FCSTD DOCUMENT  (FreeCAD 0.21R33771 (Git))
Label: pillerAssy5
License: All rights reserved
objects: Part::FeaturePython×74, Sketcher::SketchObject×61, Part::Extrusion×56, Part::Mirroring×33, App::Part×32, Part::Compound×27, Part::Cut×19, App::FeaturePython×17, Part::Feature×12, Spreadsheet::Sheet×9, Part::MultiFuse×9, Part::Revolution×7, Part::Cylinder×7, Part::Sweep×3, PartDesign::Pad×1, Part::Chamfer×1, Part::Loft×1
note: 297 computed .brp shape members not serialized (recipe doc carries the construction recipe); baked Part::Feature solids carry a one-line shape summary decoded from their .brp

FEATURE [Part::Feature] Part__Feature  label="終沈躯体右_1500 v16"
  shape: bbox 17720 x 9400 x 6410 mm, 67 faces (baked)
FEATURE [Part::Feature] Part__Feature001  label="終沈躯体右_1500 v017"
  shape: bbox 17720 x 8350 x 6410 mm, 38 faces (baked)
FEATURE [Part::Feature] Part__Feature004  label="Cut036"
  shape: bbox 1100 x 1100 x 50 mm, 4 faces (baked)
FEATURE [Part::Feature] Part__Feature005  label="water_level"
  shape: bbox 15500 x 7750 x 4910 mm, 13 faces (baked)
FEATURE [Part::FeaturePython] b_centerPost1_001_  label="5_centerPost1_001"  # a2plus imported part (geometry in sourceFile) (typed FeaturePython)
  a2p_Version = 0.4.60n
  fixedPosition = true
  objectType = a2pPart
  sourceFile = .\centerPost.step
  subassemblyImport = false
  timeLastImport = 1.70943e+09
  updateColors = true
FEATURE [Part::FeaturePython] b_inflowPipe1_001_  label="2_inflowPipe1_001"  # a2plus imported part (geometry in sourceFile) (typed FeaturePython)
  Placement = pos=(-2.02e-13,0,-4.896) rot=(0,0,1;0rad)
  a2p_Version = 0.4.60n
  fixedPosition = false
  objectType = a2pPart
  sourceFile = .\inflowPipe.step
  subassemblyImport = false
  timeLastImport = 1.70943e+09
  updateColors = true
FEATURE [Part::FeaturePython] Cut036_001  # a2plus imported part (geometry in sourceFile) (typed FeaturePython)
  a2p_Version = 0.4.60n
  fixedPosition = true
  localSourceObject = Part__Feature004
  objectType = a2pPart
  sourceFile = converted
  subassemblyImport = false
  timeLastImport = 1.70945e+09
  updateColors = true
FEATURE [Part::FeaturePython] b_sludgePipe1_001_  label="3_sludgePipe1_001"  # a2plus imported part (geometry in sourceFile) (typed FeaturePython)
  Placement = pos=(1.29983,0,7.73) rot=(0,0,1;3.14159rad)
  a2p_Version = 0.4.60n
  fixedPosition = false
  objectType = a2pPart
  sourceFile = .\sludgePipe.step
  subassemblyImport = false
  timeLastImport = 1.70943e+09
  updateColors = true
FEATURE [Part::FeaturePython] b_bufflePlate_001_  label="4_bufflePlate_001"  # a2plus imported part (geometry in sourceFile) (typed FeaturePython)
  Placement = pos=(0,0,4689.6) rot=(0,0,1;0rad)
  a2p_Version = 0.4.60n
  fixedPosition = false
  objectType = a2pPart
  sourceFile = .\bufflePlate.FCStd
  subassemblyImport = false
  timeLastImport = 1.70902e+09
  updateColors = true
FEATURE [Spreadsheet::Sheet] Spreadsheet
  cells = A2='cage width W0; B2(W0)=1800; A3='cageLength L0; B3(L0)=4500; A4='mainShape mShp; B4(mShp)='100x100x10; A5='mShp gage mg0; B5(mg0)=55; A6='mShp width mb0; B6(mb0)=100; A7='horizontalBeam hShp; B7(hShp)='150x75x9; A8='hShp gage hg; B8(hg)=75; A9='hb0; B9(hb0)=75; A10='lutticeBeam LShp; B10(LShp)='75x75x6; A11='luttice_widht Lb0; B11(Lb0)=75; A12='lutitice length ll; B12(ll)=2234.39029715043; A13='luttice angle sita; B13(sita)=40.6; A14='gusset Gta; B14(Gta)=300; A15='gussetThickness gt; B15(gt)=6; A16='lx; B16(lx)=-760.518050346879; A17='lz; B17(lz)=201.097312797114; A18='Divishon no; B18(n0)=3; A19='DivishonPitch p0; B19(p0)=1450; A20='rakeWidth  rw; B20(rw)=952; A22='Angle; D22='Channel; A23='40x40x5; B23=40; C23=17; D23='75x40x5; E23=75; F23=40; G23=17; A24='50x50x5; B24=50; C24=30; D24='100x50x5; E24=100; F24=50; G24=30; A25='65x65x6; B25=65; C25=35; D25='125x65x6; E25=125; F25=65; G25=35; A26='75x75x6; B26=75; C26=40; D26='150x75x9; E26=150; F26=75; G26=40; A27='90x90x7; B27=90; C27=50; D27='180x75x7; E27=180; F27=75; G27=40; A28='100x100x10; B28=100; C28=55; F28=75; G28=40; A29='130x130x12; B29=130
FEATURE [Part::FeaturePython] AngleSteel  label="mShp"  # WARN: FeaturePython — macro-defined, semantics opaque (R4)
  A = 100
  B = 100
  L = 4500
  Placement = pos=(-850,-850,0) rot=(0,0,1;1.5708rad)
  Solid = true
  g0 = 7.85
  mass = 67.1327
  size = 17
  standard = SS_Equal
  t = 7
  expr: .Placement.Base.x = -Spreadsheet.W0 / 2 + Spreadsheet.mb0 / 2
  expr: .Placement.Base.y = -Spreadsheet.W0 / 2 + Spreadsheet.mb0 / 2
  expr: L = Spreadsheet.L0
FEATURE [Part::FeaturePython] Array  # Draft array (typed FeaturePython)
  AlwaysSyncPlacement = false
  Angle = 360
  ArrayType = 1
  Axis = (0,0,1)
  Base = -> AngleSteel
  Center = (0,0,0)
  Count = 4
  ExpandArray = false
  Fuse = false
  IntervalAxis = (0,0,0)
  IntervalX = (50,0,0)
  IntervalY = (0,50,0)
  IntervalZ = (0,0,50)
  NumberCircles = 3
  NumberPolar = 4
  NumberX = 2
  NumberY = 2
  NumberZ = 1
  PlacementList = 4 placements: [(-850,-850,0),(850,-850,0),(850,850,0),(-850,850,0)]
  RadialDistance = 50
  ScaleList = (4) [(1,1,1),(1,1,1),(1,1,1),(1,1,1)]
  Symmetry = 1
  TangentialDistance = 25
FEATURE [Part::FeaturePython] ChannelSteel  label="hShp"  # WARN: FeaturePython — macro-defined, semantics opaque (R4)
  B = 75
  H = 150
  L = 1600
  Placement = pos=(-800,-862.5,75) rot=(0.57735,0.57735,0.57735;2.0944rad)
  Solid = true
  g0 = 7.85
  mass = 35.6065
  size = 4
  standard = SS
  t1 = 6
  t2 = 8
  expr: .Placement.Base.x = -Spreadsheet.W0 / 2 + Spreadsheet.mb0
  expr: .Placement.Base.y = -Spreadsheet.W0 / 2 + Spreadsheet.hb0 / 2
  expr: .Placement.Base.z = Spreadsheet.hg
  expr: L = Spreadsheet.W0 - Spreadsheet.mb0 * 2
FEATURE [Part::FeaturePython] Array001  label="hBeam"  # Draft array (typed FeaturePython)
  AlwaysSyncPlacement = false
  Angle = 360
  ArrayType = 0
  Axis = (0,0,1)
  Base = -> ChannelSteel
  Center = (0,0,0)
  Count = 4
  ExpandArray = false
  Fuse = false
  IntervalAxis = (0,0,0)
  IntervalX = (100,0,0)
  IntervalY = (0,100,0)
  IntervalZ = (0,0,1450)
  NumberCircles = 3
  NumberPolar = 5
  NumberX = 1
  NumberY = 1
  NumberZ = 4
  PlacementList = 4 placements: arithmetic series from (-800,-862.5,75) step (0,0,1450) to (-800,-862.5,4425)
  RadialDistance = 50
  ScaleList = (4) [(1,1,1),(1,1,1),(1,1,1),(1,1,1)]
  Symmetry = 1
  TangentialDistance = 25
  expr: .IntervalZ.z = Spreadsheet.p0
  expr: NumberZ = Spreadsheet.n0 + 1
FEATURE [Part::FeaturePython] AngleSteel001  label="LShp"  # WARN: FeaturePython — macro-defined, semantics opaque (R4)
  A = 75
  B = 75
  L = 1000
  Placement = pos=(0,0,0) rot=(-1,0,0;1.5708rad)
  Solid = false
  g0 = 7.85
  mass = 0
  size = 10
  standard = SS_Equal
  t = 6
FEATURE [Part::FeaturePython] ChannelSteel001  # WARN: FeaturePython — macro-defined, semantics opaque (R4)
  B = 75
  H = 150
  L = 680
  Placement = pos=(0,0,6e-15) rot=(0.57735,-0.57735,-0.57735;2.0944rad)
  Solid = true
  g0 = 7.85
  mass = 15.1328
  size = 4
  standard = SS
  t1 = 6
  t2 = 8
FEATURE [Sketcher::SketchObject] Sketch006
  ExternalGeometry = -> [ChannelSteel001]
  FullyConstrained = false
  MapMode = 5
  Placement = pos=(7.49e-14,-8.3e-15,75) rot=(0,0,1;1.5708rad)
  Support = -> [ChannelSteel001]
  sketch-geometry (3):
    g0: LineSegment StartX=37.5 StartY=0 StartZ=0 EndX=-38.6181 EndY=76.1181 EndZ=0
    g1: LineSegment StartX=-38.6181 StartY=0 StartZ=0 EndX=37.5 EndY=0 EndZ=0
    g2: LineSegment StartX=-38.6181 StartY=0 StartZ=0 EndX=-38.6181 EndY=76.1181 EndZ=0
  constraints (7):
    c: Coincident(g-3,g0)
    c: Coincident(g1,g0)
    c: Coincident(g2,g1)
    c: Coincident(g2,g0)
    c: Vertical(g2)
    c: Horizontal(g1)
    c: Angle(g0,g1) = 0.785398
FEATURE [Part::Extrusion] Extrude006
  Base = -> Sketch006
  Dir = (1e-15,-1e-16,1)
  DirMode = 2
  FaceMakerClass = Part::FaceMakerBullseye
  LengthFwd = 150
  LengthRev = 0
  Reversed = true
  Solid = true
  Symmetric = false
FEATURE [Part::Mirroring] Mirror005  label="Extrude006 (mirrored)"
  Base = (-500,32.5,62.5)
  Normal = (-1,9e-16,0)
  Placement = pos=(299.54,0,0) rot=(0,0,1;0rad)
  Source = -> Extrude006
FEATURE [Part::Compound] Compound003
  Links = -> [Mirror005,Extrude006]
FEATURE [Part::Cut] Cut
  Base = -> ChannelSteel001
  Placement = pos=(-363,-857,75) rot=(0,0,-1;0.785398rad)
  Tool = -> Compound003
  expr: .Placement.Base.x = -Spreadsheet.W0 / 2 + 537
  expr: .Placement.Base.y = -Spreadsheet.W0 / 2 + 43
FEATURE [Sketcher::SketchObject] Sketch007
  FullyConstrained = true
  MapMode = 5
  Placement = pos=(0,0,0) rot=(1,0,0;1.5708rad)
  expr: Constraints[10] = Spreadsheet.W0 / 2
  expr: Constraints[15] = Spreadsheet.hg
  expr: Constraints[9] = Spreadsheet.hg * 2
  sketch-geometry (7):
    g0: LineSegment StartX=900 StartY=1.42e-14 StartZ=0 EndX=900 EndY=150 EndZ=0
    g1: LineSegment StartX=900 StartY=150 StartZ=0 EndX=930 EndY=150 EndZ=0
    g2: LineSegment StartX=930 StartY=150 StartZ=0 EndX=999.298 EndY=104.199 EndZ=0
    g3: ArcOfCircle CenterX=980 CenterY=75 CenterZ=0 NormalX=0 NormalY=0 NormalZ=1 AngleXU=0 Radius=35 StartAngle=5.29641 EndAngle=7.26996
    g4: LineSegment StartX=999.298 StartY=45.8011 StartZ=0 EndX=930 EndY=1.42e-14 EndZ=0
    g5: LineSegment StartX=930 StartY=1.42e-14 StartZ=0 EndX=900 EndY=1.42e-14 EndZ=0
    g6: Circle CenterX=980 CenterY=75 CenterZ=0 NormalX=0 NormalY=0 NormalZ=1 AngleXU=0 Radius=15
  constraints (19):
    c: Vertical(g0)
    c: Coincident(g0,g1)
    c: Horizontal(g1)
    c: Coincident(g1,g2)
    c: Tangent(g2,g3) = 1.5708
    c: Coincident(g4,g5)
    c: Coincident(g5,g0)
    c: Horizontal(g5)
    c: Coincident(g6,g3)
    c: DistanceY(g0,g0) = 150
    c: DistanceX(g-1,g0) = 900
    c: PointOnObject(g0,g-1)
    c: Vertical(g4,g1)
    c: DistanceX(g0,g3) = 80
    c: Tangent(g3,g4) = 1.5708
    c: DistanceY(g3,g1) = 75
    c: Radius(g6) = 15
    c: Radius(g3) = 35
    c: DistanceX(g0,g4) = 30
FEATURE [PartDesign::Pad] Pad
  Direction = (0,-1,2e-16)
  Length = 48
  Length2 = 10
  Midplane = true
  Placement = pos=(0,0,0) rot=(1,0,0;1.5708rad)
  Profile = -> Sketch007
  ReferenceAxis = -> Sketch007 [N_Axis]
  Type = 0
FEATURE [Sketcher::SketchObject] Sketch008
  ExternalGeometry = -> [Pad]
  FullyConstrained = true
  MapMode = 5
  Placement = pos=(0,0,8.9e-14) rot=(1,0,0;3.14159rad)
  sketch-geometry (4):
    g0: LineSegment StartX=900 StartY=-8 StartZ=0 EndX=1050 EndY=-8 EndZ=0
    g1: LineSegment StartX=1050 StartY=-8 StartZ=0 EndX=1050 EndY=8 EndZ=0
    g2: LineSegment StartX=1050 StartY=8 StartZ=0 EndX=900 EndY=8 EndZ=0
    g3: LineSegment StartX=900 StartY=8 StartZ=0 EndX=900 EndY=-8 EndZ=0
  constraints (12):
    c: Coincident(g0,g1)
    c: Coincident(g1,g2)
    c: Coincident(g2,g3)
    c: Coincident(g3,g0)
    c: Horizontal(g0)
    c: Horizontal(g2)
    c: Vertical(g1)
    c: Vertical(g3)
    c: Distance(g1) = 16
    c: PointOnObject(g2,g-4)
    c: DistanceY(g2,g-4) = 16
    c: DistanceX(g2,g2) = 150
FEATURE [Part::Extrusion] Extrude007
  Base = -> Sketch008
  Dir = (0,0,-1)
  DirMode = 2
  FaceMakerClass = Part::FaceMakerBullseye
  LengthFwd = 150
  LengthRev = 0
  Reversed = true
  Solid = true
  Symmetric = false
FEATURE [Part::Cut] Cut001
  Base = -> Pad
  Placement = pos=(0,-492,0) rot=(0,0,1;0rad)
  Tool = -> Extrude007
  expr: .Placement.Base.y = -Spreadsheet.rw / 2 - 16
FEATURE [Part::Mirroring] Mirror006  label="Cut001 (mirrored)"
  Base = (0,0,400)
  Normal = (0,-1,0)
  Source = -> Cut001
FEATURE [Part::Compound] Compound004
  Links = -> [Mirror006,Cut001]
FEATURE [Part::FeaturePython] AngleSteel002  label="LShp001"  # WARN: FeaturePython — macro-defined, semantics opaque (R4)
  A = 75
  B = 75
  L = 2234.39
  Placement = pos=(-850,-932.5,1525) rot=(0,1,0;2.2794rad)
  Solid = true
  g0 = 7.85
  mass = 15.306
  size = 10
  standard = SS_Equal
  t = 6
  expr: .Placement.Base.x = -Spreadsheet.W0 / 2 + Spreadsheet.mb0 / 2
  expr: .Placement.Base.y = -Spreadsheet.W0 / 2 - 32.5
  expr: .Placement.Base.z = Spreadsheet.p0 + Spreadsheet.hg
  expr: .Placement.Rotation.Angle = Spreadsheet.sita + 90
  expr: L = Spreadsheet.ll
FEATURE [Part::FeaturePython] Array008  # Draft array (typed FeaturePython)
  AlwaysSyncPlacement = false
  Angle = 360
  ArrayType = 0
  Axis = (0,0,1)
  Base = -> AngleSteel002
  Center = (0,0,0)
  Count = 3
  ExpandArray = false
  Fuse = false
  IntervalAxis = (0,0,0)
  IntervalX = (100,0,0)
  IntervalY = (0,100,0)
  IntervalZ = (0,0,1450)
  NumberCircles = 3
  NumberPolar = 5
  NumberX = 1
  NumberY = 1
  NumberZ = 3
  PlacementList = 3 placements: arithmetic series from (-850,-932.5,1525) step (0,0,1450) to (-850,-932.5,4425)
  RadialDistance = 50
  ScaleList = (3) [(1,1,1),(1,1,1),(1,1,1)]
  Symmetry = 1
  TangentialDistance = 25
  expr: .IntervalZ.z = Spreadsheet.p0
  expr: NumberZ = Spreadsheet.n0
FEATURE [Sketcher::SketchObject] Sketch009
  ExternalGeometry = -> [Compound004]
  FullyConstrained = true
  Placement = pos=(0,0,0) rot=(1,0,0;1.5708rad)
  expr: Constraints[17] = Spreadsheet.p0
  sketch-geometry (7):
    g0: LineSegment StartX=900 StartY=1462.5 StartZ=0 EndX=900 EndY=1587.5 EndZ=0
    g1: LineSegment StartX=900 StartY=1587.5 StartZ=0 EndX=930 EndY=1587.5 EndZ=0
    g2: LineSegment StartX=930 StartY=1587.5 StartZ=0 EndX=995.018 EndY=1556.61 EndZ=0
    g3: ArcOfCircle CenterX=980 CenterY=1525 CenterZ=0 NormalX=0 NormalY=0 NormalZ=1 AngleXU=0 Radius=35 StartAngle=5.15587 EndAngle=7.41051
    g4: LineSegment StartX=995.018 StartY=1493.39 StartZ=0 EndX=930 EndY=1462.5 EndZ=0
    g5: LineSegment StartX=930 StartY=1462.5 StartZ=0 EndX=900 EndY=1462.5 EndZ=0
    g6: Circle CenterX=980 CenterY=1525 CenterZ=0 NormalX=0 NormalY=0 NormalZ=1 AngleXU=0 Radius=15
  constraints (19):
    c: Vertical(g0)
    c: Coincident(g0,g1)
    c: Horizontal(g1)
    c: Coincident(g1,g2)
    c: Tangent(g2,g3) = 1.5708
    c: Coincident(g4,g5)
    c: Coincident(g5,g0)
    c: Horizontal(g5)
    c: Coincident(g6,g3)
    c: Radius(g6) = 15
    c: Radius(g3) = 35
    c: DistanceX(g1,g1) = 30
    c: Distance(g3,g0) = 80
    c: Tangent(g3,g4) = 1.5708
    c: Equal(g5,g1)
    c: Equal(g4,g2)
    c: Distance(g0) = 125
    c: DistanceY(g-3,g3) = 1450
    c: Vertical(g-3,g3)
FEATURE [Part::Extrusion] Extrude
  Base = -> Sketch009
  Dir = (0,-1,2e-16)
  DirMode = 2
  FaceMakerClass = Part::FaceMakerBullseye
  LengthFwd = 16
  LengthRev = 0
  Placement = pos=(0,-492,0) rot=(0,0,1;0rad)
  Solid = true
  Symmetric = true
  expr: .Placement.Base.y = -Spreadsheet.rw / 2 - 16
FEATURE [Part::Mirroring] Mirror  label="Extrude (mirrored)"
  Base = (0,0,1500)
  Normal = (0,1,0)
  Source = -> Extrude
FEATURE [Part::Compound] Compound005
  Links = -> [Mirror,Extrude]
FEATURE [Part::Compound] Compound006
  Links = -> [Compound005,Compound004]
FEATURE [Part::Mirroring] Mirror007  label="Compound006 (mirrored)"
  Base = (0,0,-1000)
  Normal = (1,0,0)
  Source = -> Compound006
FEATURE [Part::FeaturePython] ChannelSteel002  # WARN: FeaturePython — macro-defined, semantics opaque (R4)
  B = 75
  H = 150
  L = 1200
  Placement = pos=(500,0,4350) rot=(0,0,1;0rad)
  Solid = false
  g0 = 7.85
  mass = 0
  size = 4
  standard = SS
  t1 = 9
  t2 = 12.5
  expr: .Placement.Base.z = Spreadsheet.L0 - 150
FEATURE [Part::Extrusion] Extrude008
  Base = -> ChannelSteel002
  Dir = (0,1,0)
  DirMode = 2
  FaceMakerClass = Part::FaceMakerBullseye
  LengthFwd = 1334
  LengthRev = 0
  Solid = false
  Symmetric = true
FEATURE [Sketcher::SketchObject] Sketch010
  ExternalGeometry = -> [Extrude008]
  FullyConstrained = true
  MapMode = 5
  Placement = pos=(0,0,4500) rot=(0,0,1;0rad)
  Support = -> [Extrude008]
  sketch-geometry (3):
    g0: LineSegment StartX=500 StartY=667 StartZ=0 EndX=575 EndY=592 EndZ=0
    g1: LineSegment StartX=575 StartY=592 StartZ=0 EndX=575 EndY=667 EndZ=0
    g2: LineSegment StartX=575 StartY=667 StartZ=0 EndX=500 EndY=667 EndZ=0
  constraints (7):
    c: Coincident(g0,g1)
    c: Coincident(g1,g2)
    c: Coincident(g2,g0)
    c: Coincident(g1,g-3)
    c: PointOnObject(g0,g-4)
    c: Coincident(g0,g-3)
    c: Angle(g1,g0) = 0.785398
FEATURE [Part::Extrusion] Extrude009
  Base = -> Sketch010
  Dir = (0,0,1)
  DirMode = 2
  FaceMakerClass = Part::FaceMakerBullseye
  LengthFwd = 150
  LengthRev = 0
  Reversed = true
  Solid = true
  Symmetric = false
FEATURE [Part::Mirroring] Mirror008  label="Extrude009 (mirrored)"
  Base = (300,0,0)
  Normal = (0,1,0)
  Source = -> Extrude009
FEATURE [Part::Compound] Compound008
  Links = -> [Mirror008,Extrude009]
FEATURE [Part::Cut] Cut002
  Base = -> Extrude008
  Tool = -> Compound008
FEATURE [Part::FeaturePython] Array010  # Draft array (typed FeaturePython)
  AlwaysSyncPlacement = false
  Angle = 360
  ArrayType = 1
  Axis = (0,0,1)
  Base = -> Cut
  Center = (0,0,0)
  Count = 4
  ExpandArray = false
  Fuse = false
  IntervalAxis = (0,0,0)
  IntervalX = (50,0,0)
  IntervalY = (0,50,0)
  IntervalZ = (0,0,50)
  NumberCircles = 3
  NumberPolar = 4
  NumberX = 2
  NumberY = 2
  NumberZ = 1
  PlacementList = 4 placements: [(-363,-857,75),(857,-363,75),(363,857,75),(-857,363,75)]
  RadialDistance = 50
  ScaleList = (4) [(1,1,1),(1,1,1),(1,1,1),(1,1,1)]
  Symmetry = 1
  TangentialDistance = 25
FEATURE [Part::Mirroring] Mirror009  label="Cut002 (mirrored)"
  Base = (0,-600,0)
  Normal = (1,0,0)
  Source = -> Cut002
FEATURE [Part::FeaturePython] ChannelSteel003  # WARN: FeaturePython — macro-defined, semantics opaque (R4)
  B = 75
  H = 150
  L = 1000
  Placement = pos=(-500,538,4425) rot=(0.57735,0.57735,0.57735;2.0944rad)
  Solid = true
  g0 = 7.85
  mass = 22.2541
  size = 4
  standard = SS
  t1 = 9
  t2 = 12.5
FEATURE [Part::FeaturePython] Array011  # Draft array (typed FeaturePython)
  AlwaysSyncPlacement = false
  Angle = 360
  ArrayType = 0
  Axis = (0,0,1)
  Base = -> Array010
  Center = (0,0,0)
  Count = 4
  ExpandArray = false
  Fuse = false
  IntervalAxis = (0,0,0)
  IntervalX = (100,0,0)
  IntervalY = (0,100,0)
  IntervalZ = (0,0,1450)
  NumberCircles = 3
  NumberPolar = 5
  NumberX = 1
  NumberY = 1
  NumberZ = 4
  PlacementList = 4 placements: arithmetic series from (0,0,0) step (0,0,1450) to (0,0,4350)
  RadialDistance = 50
  ScaleList = (4) [(1,1,1),(1,1,1),(1,1,1),(1,1,1)]
  Symmetry = 1
  TangentialDistance = 25
  expr: .IntervalZ.z = Spreadsheet.p0
FEATURE [Part::Mirroring] Mirror010  label="ChannelSteel003 (mirrored)"
  Base = (-300,0,0)
  Normal = (0,-1,0)
  Source = -> ChannelSteel003
FEATURE [Part::Feature] Part__Feature006  label="reducer"
  Placement = pos=(0,0,4357.64) rot=(0,0,1;0rad)
  shape: bbox 1029 x 1029 x 150 mm, 111 faces (baked)
FEATURE [Part::Feature] Part__Feature008  label="Compound017"
  shape: bbox 785.2 x 75 x 709.2 mm, 36 faces (baked)
FEATURE [Part::Feature] Part__Feature009  label="Compound018"
  shape: bbox 75 x 75 x 380 mm, 11 faces (baked)
FEATURE [App::Part] Compound017  label="brade"
  Group = -> [Part__Feature008,Part__Feature009]
  Origin = -> Origin005
  Placement = pos=(23,0,-1177.59) rot=(0,0,1;0rad)
FEATURE [Part::FeaturePython] Array012  # Draft array (typed FeaturePython)
  AlwaysSyncPlacement = false
  Angle = 360
  ArrayType = 1
  Axis = (0,0,1)
  Base = -> Compound017
  Center = (0,0,0)
  Count = 2
  ExpandArray = false
  Fuse = false
  IntervalAxis = (0,0,0)
  IntervalX = (50,0,0)
  IntervalY = (0,50,0)
  IntervalZ = (0,0,50)
  NumberCircles = 3
  NumberPolar = 2
  NumberX = 2
  NumberY = 2
  NumberZ = 1
  Placement = pos=(0,0,50) rot=(0,0,1;0rad)
  PlacementList = 2 placements: [(23,0,-1177.59),(-23,2.81669e-15,-1177.59)]
  RadialDistance = 50
  ScaleList = (2) [(1,1,1),(1,1,1)]
  Symmetry = 1
  TangentialDistance = 25
FEATURE [Part::Compound] Compound
  Links = -> [Array008,Array001]
FEATURE [Part::FeaturePython] Array013  # Draft array (typed FeaturePython)
  AlwaysSyncPlacement = false
  Angle = 360
  ArrayType = 1
  Axis = (0,0,1)
  Base = -> Compound
  Center = (0,0,0)
  Count = 4
  ExpandArray = false
  Fuse = false
  IntervalAxis = (0,0,0)
  IntervalX = (50,0,0)
  IntervalY = (0,50,0)
  IntervalZ = (0,0,50)
  NumberCircles = 3
  NumberPolar = 4
  NumberX = 2
  NumberY = 2
  NumberZ = 1
  PlacementList = 4 placements: [(0,0,0),(0,0,0),(0,0,0),(0,0,0)]
  RadialDistance = 50
  ScaleList = (4) [(1,1,1),(1,1,1),(1,1,1),(1,1,1)]
  Symmetry = 1
  TangentialDistance = 25
FEATURE [Part::FeaturePython] b_trunBackle_001_  label="trunBackle_001"  # a2plus imported part (geometry in sourceFile) (typed FeaturePython)
  Placement = pos=(980,492.973,2505.44) rot=(0,1,0;3.33869rad)
  a2p_Version = 0.4.60n
  fixedPosition = false
  objectType = a2pPart
  sourceFile = .\trunBackle.FCStd
  subassemblyImport = false
  timeLastImport = 1.70945e+09
  updateColors = true
FEATURE [Part::Compound] Compound019  label="Compound020"
  Links = -> [Mirror007,Compound006]
FEATURE [App::Part] Part  label="centerCage"
  Group = -> [Spreadsheet,ChannelSteel,Array001,AngleSteel,Array,AngleSteel001,ChannelSteel001,Compound003,Sketch006,Mirror005,Extrude006,Cut,Sketch007,Pad,Sketch008,Extrude007,Cut001,Mirror006,Compound004,AngleSteel002,Array008,Sketch009,Extrude,Mirror,Compound005,Compound006,Mirror007,Compound008,Extrude008,Extrude009,ChannelSteel002,Mirror008,Sketch010,Cut002,Mirror009,ChannelSteel003,Array010,Array011,+7 more]
  Origin = -> Origin002
FEATURE [Part::Compound] Compound018  label="centerCage002"
  Links = -> [Part]
FEATURE [App::Part] Part002  label="centerCage003"
  Group = -> [Part,Compound018]
  Origin = -> Origin007
FEATURE [Part::FeaturePython] b_RakeArm_001_  label="RakeArm_001"  # a2plus imported part (geometry in sourceFile) (typed FeaturePython)
  Placement = pos=(980,-493.6,1055.44) rot=(0,0,1;0rad)
  a2p_Version = 0.4.60n
  fixedPosition = false
  objectType = a2pPart
  sourceFile = .\RakeArm.FCStd
  subassemblyImport = false
  timeLastImport = 1.70944e+09
  updateColors = true
FEATURE [Part::FeaturePython] centerCage002_001  # a2plus imported part (geometry in sourceFile) (typed FeaturePython)
  Placement = pos=(0,0,980.44) rot=(0,0,1;0rad)
  a2p_Version = 0.4.60n
  fixedPosition = true
  localSourceObject = Compound018
  objectType = a2pPart
  sourceFile = converted
  subassemblyImport = false
  timeLastImport = 1.70945e+09
  updateColors = true
FEATURE [Part::FeaturePython] b_brade_001_  label="brade_001"  # a2plus imported part (geometry in sourceFile) (typed FeaturePython)
  Placement = pos=(3000,-0.310648,1746.81) rot=(0,0,-1;0.785398rad)
  a2p_Version = 0.4.60n
  fixedPosition = false
  objectType = a2pPart
  sourceFile = .\brade.FCStd
  subassemblyImport = false
  timeLastImport = 1.70876e+09
  updateColors = true
FEATURE [App::Part] Part003  label="rake"
  Origin = -> Origin008
  Placement = pos=(0,-6,0) rot=(0,1,0;-0.099484rad)
FEATURE [Part::FeaturePython] Array014  # Draft array (typed FeaturePython)
  AlwaysSyncPlacement = false
  Angle = 360
  ArrayType = 0
  Axis = (0,0,1)
  Base = -> b_brade_001_
  Center = (0,0,0)
  Count = 6
  ExpandArray = false
  Fuse = false
  IntervalAxis = (0,0,0)
  IntervalX = (1020,0,0)
  IntervalY = (0,100,0)
  IntervalZ = (0,0,100)
  NumberCircles = 3
  NumberPolar = 5
  NumberX = 6
  NumberY = 1
  NumberZ = 1
  Placement = pos=(-1000,0.000107765,-790) rot=(0,0,1;0rad)
  PlacementList = 6 placements: arithmetic series from (3000,-0.310648,1746.81) step (1020,0,0) to (8100,-0.310648,1746.81)
  RadialDistance = 50
  ScaleList = (6) [(1,1,1),(1,1,1),(1,1,1),(1,1,1),(1,1,1),(1,1,1)]
  Symmetry = 1
  TangentialDistance = 25
FEATURE [Part::Compound] Compound020  label="rake001"
  Links = -> [Part003]
  Placement = pos=(113.646,-0.25,-95.1183) rot=(-1e-06,1,-2e-06;0.099484rad)
FEATURE [Part::FeaturePython] Clone  label="trunBackle_002"  # Draft clone (typed FeaturePython)
  AttacherType = Attacher::AttachEngine3D
  Fuse = false
  Objects = -> [b_trunBackle_001_]
  Placement = pos=(980,-492.16,2505.44) rot=(0,1,0;3.33869rad)
  Scale = (1,1,1)
FEATURE [Part::Compound] Compound022  label="rake002"
  Links = -> [b_RakeArm_001_,Array014]
  Placement = pos=(113.646,-6.52,-95.1183) rot=(0,-1,0;0.102943rad)
FEATURE [App::FeaturePython] axisCoincident_001  label="axisCoincident_001__Compound022"  # a2plus constraint (typed FeaturePython)
  Object1 = centerCage002_001
  Object2 = Compound022
  SubElement1 = Edge54
  SubElement2 = Edge93
  Suppressed = false
  Type = axial
  directionConstraint = 0
  lockRotation = false
FEATURE [App::FeaturePython] axisCoincident_002  label="axisCoincident_002__Compound022"  # a2plus constraint (typed FeaturePython)
  Object1 = b_trunBackle_001_
  Object2 = Compound022
  SubElement1 = Face69
  SubElement2 = Face1
  Suppressed = false
  Type = axial
  directionConstraint = 0
  lockRotation = false
FEATURE [App::FeaturePython] axisCoincident_003  label="axisCoincident_003__centerCage002_001"  # a2plus constraint (typed FeaturePython)
  Object1 = b_trunBackle_001_
  Object2 = centerCage002_001
  ParentTreeObject = -> b_trunBackle_001_
  SubElement1 = Edge101
  SubElement2 = Edge2376
  Suppressed = false
  Type = axial
  directionConstraint = 0
  lockRotation = false
FEATURE [App::FeaturePython] axisCoincident_003_mirror  label="axisCoincident_003__trunBackle_001"  # a2plus constraint (typed FeaturePython)
  Object1 = b_trunBackle_001_
  Object2 = centerCage002_001
  ParentTreeObject = -> centerCage002_001
  SubElement1 = Edge101
  SubElement2 = Edge2376
  Suppressed = false
  Type = axial
  directionConstraint = 0
  lockRotation = false
FEATURE [Part::Compound] Compound023  label="rake003"
  Links = -> [b_trunBackle_001_,Clone,Compound022]
FEATURE [Part::FeaturePython] Array015  # Draft array (typed FeaturePython)
  AlwaysSyncPlacement = false
  Angle = 360
  ArrayType = 1
  Axis = (0,0,1)
  Base = -> Compound023
  Center = (0,0,980.44)
  Count = 2
  ExpandArray = false
  Fuse = false
  IntervalAxis = (0,0,0)
  IntervalX = (50,0,0)
  IntervalY = (0,50,0)
  IntervalZ = (0,0,50)
  NumberCircles = 3
  NumberPolar = 2
  NumberX = 2
  NumberY = 2
  NumberZ = 1
  PlacementList = 2 placements: [(0,0,0),(0,0,0)]
  RadialDistance = 50
  ScaleList = (2) [(1,1,1),(1,1,1)]
  Symmetry = 1
  TangentialDistance = 25
FEATURE [Sketcher::SketchObject] Sketch
  FullyConstrained = true
  Placement = pos=(0,0,0) rot=(1,0,0;1.5708rad)
  expr: Constraints[11] = Spreadsheet001.dia / 2
  expr: Constraints[9] = Spreadsheet001.h0
  sketch-geometry (4):
    g0: LineSegment StartX=1545 StartY=0 StartZ=0 EndX=1550 EndY=0 EndZ=0
    g1: LineSegment StartX=1550 StartY=0 StartZ=0 EndX=1550 EndY=2100 EndZ=0
    g2: LineSegment StartX=1550 StartY=2100 StartZ=0 EndX=1545 EndY=2100 EndZ=0
    g3: LineSegment StartX=1545 StartY=2100 StartZ=0 EndX=1545 EndY=0 EndZ=0
  constraints (12):
    c: Coincident(g0,g1)
    c: Coincident(g1,g2)
    c: Coincident(g2,g3)
    c: Coincident(g3,g0)
    c: Horizontal(g0)
    c: Horizontal(g2)
    c: Vertical(g1)
    c: Vertical(g3)
    c: DistanceX(g2,g2) = 5
    c: DistanceY(g1,g1) = 2100
    c: PointOnObject(g0,g-1)
    c: DistanceX(g-1,g0) = 1550
FEATURE [Part::Revolution] Revolve
  Angle = 360
  Axis = (0,0,1)
  Base = (0,0,0)
  FaceMakerClass = Part::FaceMakerBullseye
  Solid = true
  Source = -> Sketch
  Symmetric = false
FEATURE [Part::FeaturePython] AngleSteel003  label="AngleSteel"  # WARN: FeaturePython — macro-defined, semantics opaque (R4)
  A = 75
  B = 75
  L = 1000
  Placement = pos=(1550,0,0) rot=(0,0,1;0rad)
  Solid = false
  g0 = 7.85
  mass = 0
  size = 10
  standard = SS_Equal
  t = 6
  expr: .Placement.Base.x = Spreadsheet001.dia / 2
FEATURE [Part::Revolution] Revolve001
  Angle = 360
  Axis = (0,0,1)
  Base = (0,0,0)
  FaceMakerClass = Part::FaceMakerBullseye
  Solid = false
  Source = -> AngleSteel003
  Symmetric = false
FEATURE [Part::FeaturePython] AngleSteel004  label="AngleSteel001"  # WARN: FeaturePython — macro-defined, semantics opaque (R4)
  A = 75
  B = 75
  L = 1000
  Placement = pos=(1550,0,2100) rot=(0,1,0;1.5708rad)
  Solid = false
  g0 = 7.85
  mass = 0
  size = 10
  standard = SS_Equal
  t = 6
  expr: .Placement.Base.x = Spreadsheet001.dia / 2
  expr: .Placement.Base.z = Spreadsheet001.h0
FEATURE [Part::Revolution] Revolve002
  Angle = 360
  Axis = (0,0,1)
  Base = (0,0,0)
  FaceMakerClass = Part::FaceMakerBullseye
  Solid = false
  Source = -> AngleSteel004
  Symmetric = false
FEATURE [Sketcher::SketchObject] Sketch001
  ExternalGeometry = -> [Revolve002]
  FullyConstrained = true
  Placement = pos=(0,0,0) rot=(1,0,0;1.5708rad)
  sketch-geometry (4):
    g0: LineSegment StartX=-275 StartY=1580 StartZ=0 EndX=275 EndY=1580 EndZ=0
    g1: LineSegment StartX=275 StartY=1580 StartZ=0 EndX=275 EndY=2100 EndZ=0
    g2: LineSegment StartX=275 StartY=2100 StartZ=0 EndX=-275 EndY=2100 EndZ=0
    g3: LineSegment StartX=-275 StartY=2100 StartZ=0 EndX=-275 EndY=1580 EndZ=0
  constraints (12):
    c: Coincident(g0,g1)
    c: Coincident(g1,g2)
    c: Coincident(g2,g3)
    c: Coincident(g3,g0)
    c: Horizontal(g0)
    c: Horizontal(g2)
    c: Vertical(g1)
    c: Vertical(g3)
    c: DistanceX(g0,g0) = 550
    c: DistanceY(g1,g1) = 520
    c: PointOnObject(g1,g-3)
    c: DistanceX(g-1,g0) = 275
FEATURE [Part::Extrusion] Extrude010
  Base = -> Sketch001
  Dir = (0,-1,2e-16)
  DirMode = 2
  FaceMakerClass = Part::FaceMakerBullseye
  LengthFwd = 1700
  LengthRev = 0
  Solid = true
  Symmetric = false
FEATURE [Part::MultiFuse] Fusion
  Shapes = -> [Revolve,Revolve001,Revolve002]
FEATURE [Part::Cut] Cut003
  Base = -> Fusion
  Tool = -> Extrude010
FEATURE [Sketcher::SketchObject] Sketch002
  ExternalGeometry = -> [Cut003]
  FullyConstrained = false
  MapMode = 5
  Placement = pos=(0,3.476e-13,1580) rot=(0,0,1;0rad)
  Support = -> [Cut003]
  sketch-geometry (4):
    g0: LineSegment StartX=-275 StartY=-1515.41 StartZ=0 EndX=-275 EndY=-1545.41 EndZ=0
    g1: LineSegment StartX=-275 StartY=-1515.41 StartZ=0 EndX=275 EndY=-1515.41 EndZ=0
    g2: LineSegment StartX=275 StartY=-1515.41 StartZ=0 EndX=275 EndY=-1545.41 EndZ=0
    g3: ArcOfCircle CenterX=3.103e-13 CenterY=-44.7314 CenterZ=0 NormalX=0 NormalY=0 NormalZ=1 AngleXU=0 Radius=1525.67 StartAngle=4.53115 EndAngle=4.89363
  constraints (12):
    c: Vertical(g0)
    c: Coincident(g0,g1)
    c: Horizontal(g1)
    c: Coincident(g1,g2)
    c: Vertical(g2)
    c: Coincident(g3,g0)
    c: Coincident(g3,g2)
    c: PointOnObject(g-3,g0)
    c: PointOnObject(g-4,g2)
    c: DistanceY(g-3,g0) = 10
    c: DistanceY(g0,g0) = 30
    c: Equal(g0,g2)
FEATURE [Part::Extrusion] Extrude001
  Base = -> Sketch002
  Dir = (0,2e-16,1)
  DirMode = 2
  FaceMakerClass = Part::FaceMakerBullseye
  LengthFwd = 5
  LengthRev = 0
  Solid = true
  Symmetric = false
FEATURE [Sketcher::SketchObject] Sketch003
  ExternalGeometry = -> [Extrude001]
  FullyConstrained = true
  MapMode = 5
  Placement = pos=(0,7.3227e-12,1585) rot=(0,0,1;0rad)
  Support = -> [Extrude001]
  sketch-geometry (4):
    g0: LineSegment StartX=-275 StartY=-1530.41 StartZ=0 EndX=275 EndY=-1530.41 EndZ=0
    g1: LineSegment StartX=275 StartY=-1530.41 StartZ=0 EndX=275 EndY=-1520.41 EndZ=0
    g2: LineSegment StartX=275 StartY=-1520.41 StartZ=0 EndX=-275 EndY=-1520.41 EndZ=0
    g3: LineSegment StartX=-275 StartY=-1520.41 StartZ=0 EndX=-275 EndY=-1530.41 EndZ=0
  constraints (12):
    c: Coincident(g0,g1)
    c: Coincident(g1,g2)
    c: Coincident(g2,g3)
    c: Coincident(g3,g0)
    c: Horizontal(g0)
    c: Horizontal(g2)
    c: Vertical(g1)
    c: Vertical(g3)
    c: DistanceY(g1,g-3) = 5
    c: DistanceY(g1,g1) = 10
    c: PointOnObject(g1,g-4)
    c: PointOnObject(g2,g-5)
FEATURE [Part::Extrusion] Extrude002
  Base = -> Sketch003
  Dir = (0,4.6e-15,1)
  DirMode = 2
  FaceMakerClass = Part::FaceMakerBullseye
  LengthFwd = 515
  LengthRev = 0
  Solid = true
  Symmetric = false
FEATURE [Sketcher::SketchObject] Sketch004
  ExternalGeometry = -> [Extrude002]
  FullyConstrained = true
  MapMode = 5
  Placement = pos=(0,-1530.41,7.0705e-12) rot=(1,0,0;1.5708rad)
  Support = -> [Extrude002]
  sketch-geometry (4):
    g0: LineSegment StartX=-170 StartY=2100 StartZ=0 EndX=-170 EndY=1860 EndZ=0
    g1: ArcOfCircle CenterX=0 CenterY=1860 CenterZ=0 NormalX=0 NormalY=0 NormalZ=1 AngleXU=0 Radius=170 StartAngle=3.14159 EndAngle=6.28319
    g2: LineSegment StartX=170 StartY=1860 StartZ=0 EndX=170 EndY=2100 EndZ=0
    g3: LineSegment StartX=170 StartY=2100 StartZ=0 EndX=-170 EndY=2100 EndZ=0
  constraints (12):
    c: Vertical(g0)
    c: Tangent(g0,g1) = -1.5708
    c: Coincident(g1,g2)
    c: Vertical(g2)
    c: Coincident(g2,g3)
    c: Coincident(g3,g0)
    c: Horizontal(g3)
    c: Radius(g1) = 170
    c: DistanceX(g-2,g1) = 170
    c: PointOnObject(g2,g-3)
    c: Distance(g1,g3) = 240
    c: PointOnObject(g1,g-2)
FEATURE [Part::Extrusion] Extrude003
  Base = -> Sketch004
  Dir = (0,-1,4.5e-15)
  DirMode = 2
  FaceMakerClass = Part::FaceMakerBullseye
  LengthFwd = 10
  LengthRev = 0
  Reversed = true
  Solid = true
  Symmetric = false
FEATURE [Part::Cut] Cut004
  Base = -> Extrude002
  Tool = -> Extrude003
FEATURE [Sketcher::SketchObject] Sketch005
  ExternalGeometry = -> [Cut004,Cut003]
  FullyConstrained = false
  MapMode = 5
  Placement = pos=(0,-1530.41,7.0705e-12) rot=(1,0,0;1.5708rad)
  Support = -> [Cut004]
  sketch-geometry (11):
    g0: Circle CenterX=-200 CenterY=1910 CenterZ=0 NormalX=0 NormalY=0 NormalZ=1 AngleXU=0 Radius=6
    g1: Circle CenterX=-200 CenterY=2050 CenterZ=0 NormalX=0 NormalY=0 NormalZ=1 AngleXU=0 Radius=6
    g2: Circle CenterX=200 CenterY=2050.06 CenterZ=0 NormalX=0 NormalY=0 NormalZ=1 AngleXU=0 Radius=6
    g3: Circle CenterX=200 CenterY=1910.17 CenterZ=0 NormalX=0 NormalY=0 NormalZ=1 AngleXU=0 Radius=6
    g4: LineSegment StartX=-200 StartY=2050 StartZ=0 EndX=200 EndY=2050.06 EndZ=0
    g5: Circle CenterX=-200 CenterY=1810 CenterZ=0 NormalX=0 NormalY=0 NormalZ=1 AngleXU=0 Radius=6
    g6: Circle CenterX=-200 CenterY=1640 CenterZ=0 NormalX=0 NormalY=0 NormalZ=1 AngleXU=0 Radius=6
    g7: Circle CenterX=200 CenterY=1809.81 CenterZ=0 NormalX=0 NormalY=0 NormalZ=1 AngleXU=0 Radius=6
    g8: Circle CenterX=200 CenterY=1639.81 CenterZ=0 NormalX=0 NormalY=0 NormalZ=1 AngleXU=0 Radius=6
    g9: LineSegment StartX=-200 StartY=1810 StartZ=0 EndX=200 EndY=1809.81 EndZ=0
    g10: Circle CenterX=0 CenterY=1640 CenterZ=0 NormalX=0 NormalY=0 NormalZ=1 AngleXU=0 Radius=6
  constraints (30):
    c: Radius(g0) = 6
    c: DistanceY(g-3,g0) = 50
    c: DistanceX(g0,g-3) = 200
    c: Radius(g1) = 6
    c: Vertical(g0,g1)
    c: Distance(g1,g-4) = 50
    c: Equal(g0,g3) = 6
    c: Equal(g1,g2) = 6
    c: Vertical(g3,g2)
    c: Coincident(g1,g4)
    c: Coincident(g2,g4)
    c: Distance(g4) = 400
    c: Angle(g4) = 0.000157168
    c: Radius(g5) = 6
    c: Equal(g5,g6) = 6
    c: DistanceY(g6,g5) = 170
    c: Vertical(g6,g5)
    c: Equal(g5,g7) = 6
    c: Equal(g7,g8) = 6
    c: DistanceY(g8,g7) = 170
    c: Vertical(g8,g7)
    c: Coincident(g5,g9)
    c: Coincident(g7,g9)
    c: Distance(g9) = 400
    c: Angle(g9) = -0.000466913
    c: DistanceX(g5,g-3) = 200
    c: PointOnObject(g10,g-2)
    c: Radius(g10) = 6
    c: Horizontal(g10,g6)
    c: DistanceY(g5,g-3) = 50
FEATURE [Part::Extrusion] Extrude004
  Base = -> Sketch005
  Dir = (0,-1,4.5e-15)
  DirMode = 2
  FaceMakerClass = Part::FaceMakerBullseye
  LengthFwd = 10
  LengthRev = 0
  Reversed = true
  Solid = true
  Symmetric = false
FEATURE [Part::Cut] Cut005
  Base = -> Cut004
  Tool = -> Extrude004
FEATURE [Spreadsheet::Sheet] Spreadsheet001  label="Spreadsheet_feedWell"
  cells = A2='tankDia   D0; B2(D0)=15500; A3='depth of water  hw; B3(hw)=3500; A4='feedWell dia  dia; B4(dia)==D0 * 0.2; A5='feedWell hight  h0; B5(h0)==hw * 0.6; A6='bracket hight h1; B6(h1)=1200
FEATURE [Sketcher::SketchObject] Sketch011
  FullyConstrained = false
  Placement = pos=(0,0,0) rot=(1,0,0;1.5708rad)
  sketch-geometry (23):
    g0: LineSegment StartX=-235 StartY=2.04e-14 StartZ=0 EndX=-166.5 EndY=2.04e-14 EndZ=0
    g1: LineSegment StartX=235 StartY=0 StartZ=0 EndX=235 EndY=240 EndZ=0
    g2: LineSegment StartX=235 StartY=240 StartZ=0 EndX=-235 EndY=240 EndZ=0
    g3: LineSegment StartX=-235 StartY=240 StartZ=0 EndX=-235 EndY=2.84e-14 EndZ=0
    g4: ArcOfCircle CenterX=0 CenterY=0 CenterZ=0 NormalX=0 NormalY=0 NormalZ=1 AngleXU=0 Radius=166.5 StartAngle=0 EndAngle=3.14159
    g5: ArcOfCircle CenterX=200 CenterY=200 CenterZ=0 NormalX=0 NormalY=0 NormalZ=1 AngleXU=0 Radius=7 StartAngle=-9e-16 EndAngle=3.14159
    g6: ArcOfCircle CenterX=200 CenterY=180 CenterZ=0 NormalX=0 NormalY=0 NormalZ=1 AngleXU=0 Radius=7 StartAngle=3.14159 EndAngle=6.28319
    g7: LineSegment StartX=193 StartY=200 StartZ=0 EndX=193 EndY=180 EndZ=0
    g8: LineSegment StartX=207 StartY=180 StartZ=0 EndX=207 EndY=200 EndZ=0
    g9: ArcOfCircle CenterX=200 CenterY=60 CenterZ=0 NormalX=0 NormalY=0 NormalZ=1 AngleXU=0 Radius=7 StartAngle=0 EndAngle=3.14159
    g10: ArcOfCircle CenterX=200 CenterY=40 CenterZ=0 NormalX=0 NormalY=0 NormalZ=1 AngleXU=0 Radius=7 StartAngle=3.14159 EndAngle=6.28319
    g11: LineSegment StartX=193 StartY=60 StartZ=0 EndX=193 EndY=40 EndZ=0
    g12: LineSegment StartX=207 StartY=40 StartZ=0 EndX=207 EndY=60 EndZ=0
    g13: ArcOfCircle CenterX=-200 CenterY=200.393 CenterZ=0 NormalX=0 NormalY=0 NormalZ=1 AngleXU=0 Radius=7 StartAngle=3e-16 EndAngle=3.14159
    g14: ArcOfCircle CenterX=-200 CenterY=180.393 CenterZ=0 NormalX=0 NormalY=0 NormalZ=1 AngleXU=0 Radius=7 StartAngle=3.14159 EndAngle=6.28319
    g15: LineSegment StartX=-207 StartY=200.393 StartZ=0 EndX=-207 EndY=180.393 EndZ=0
    g16: LineSegment StartX=-193 StartY=180.393 StartZ=0 EndX=-193 EndY=200.393 EndZ=0
    g17: ArcOfCircle CenterX=-200 CenterY=60.3929 CenterZ=0 NormalX=0 NormalY=0 NormalZ=1 AngleXU=0 Radius=7 StartAngle=0 EndAngle=3.14159
    g18: ArcOfCircle CenterX=-200 CenterY=40.3929 CenterZ=0 NormalX=0 NormalY=0 NormalZ=1 AngleXU=0 Radius=7 StartAngle=3.14159 EndAngle=6.28319
    g19: LineSegment StartX=-207 StartY=60.3929 StartZ=0 EndX=-207 EndY=40.3929 EndZ=0
    g20: LineSegment StartX=-193 StartY=40.3929 StartZ=0 EndX=-193 EndY=60.3929 EndZ=0
    g21: LineSegment StartX=207.004 StartY=200.734 StartZ=0 EndX=-193 EndY=200.393 EndZ=0
    g22: LineSegment StartX=166.5 StartY=0 StartZ=0 EndX=235 EndY=0 EndZ=0
  constraints (58):
    c: Coincident(g22,g1)
    c: Coincident(g1,g2)
    c: Coincident(g2,g3)
    c: Coincident(g3,g0)
    c: Horizontal(g0)
    c: Vertical(g1)
    c: Vertical(g3)
    c: PointOnObject(g0,g-1)
    c: Coincident(g4,g-1)
    c: Radius(g4) = 166.5
    c: DistanceX(g2,g2) = 470
    c: Symmetric(g1,g2,g-2)
    c: DistanceY(g1,g1) = 240
    c: DistanceX(g5,g5) = 14
    c: DistanceY(g7,g7) = 20
    c: DistanceY(g5,g1) = 40
    c: DistanceX(g4,g5) = 200
    c: Tangent(g9,g11) = -1.5708
    c: Tangent(g11,g10) = -1.5708
    c: Tangent(g10,g12) = -1.5708
    c: Tangent(g12,g9) = -1.5708
    c: Equal(g9,g10)
    c: Vertical(g11)
    c: Equal(g5,g9) = 14
    c: Equal(g7,g11) = 20
    c: Vertical(g9,g6)
    c: DistanceY(g9,g5) = 140
    c: Equal(g5,g13) = 14
    c: Equal(g7,g15) = 20
    c: Tangent(g17,g19) = -1.5708
    c: Tangent(g19,g18) = -1.5708
    c: Tangent(g18,g20) = -1.5708
    c: Tangent(g20,g17) = -1.5708
    c: Equal(g17,g18)
    c: Vertical(g19)
    c: Equal(g13,g17) = 14
    c: Equal(g15,g19) = 20
    c: Vertical(g17,g14)
    c: DistanceY(g17,g13) = 140
    c: Angle(g21) = -3.14074
    c: Coincident(g0,g4)
    c: Coincident(g22,g4)
    c: Horizontal(g22)
    c: PointOnObject(g1,g-1)
    c: Vertical(g16)
    c: Vertical(g15)
    c: Coincident(g13,g21)
    c: Tangent(g5,g8) = -1.5708
    c: Tangent(g16,g13) = -1.5708
    c: Tangent(g15,g14) = -1.5708
    c: Tangent(g16,g14) = -1.5708
    c: Tangent(g15,g13) = -1.5708
    c: DistanceX(g13,g4) = 200
    c: Vertical(g8)
    c: Vertical(g7)
    c: Tangent(g5,g7) = -1.5708
    c: Tangent(g7,g6) = -1.5708
    c: Tangent(g8,g6) = -1.5708
FEATURE [Part::Extrusion] Extrude005
  Base = -> Sketch011
  Dir = (0,-1,2e-16)
  DirMode = 2
  FaceMakerClass = Part::FaceMakerBullseye
  LengthFwd = 10
  LengthRev = 0
  Solid = true
  Symmetric = false
FEATURE [Sketcher::SketchObject] Sketch012
  ExternalGeometry = -> [Extrude005]
  FullyConstrained = false
  Placement = pos=(0,0,0) rot=(1,0,0;1.5708rad)
  sketch-geometry (26):
    g0: LineSegment StartX=-235 StartY=0 StartZ=0 EndX=-166.5 EndY=-4.08e-14 EndZ=0
    g1: LineSegment StartX=235 StartY=0 StartZ=0 EndX=235 EndY=-267.623 EndZ=0
    g2: LineSegment StartX=235 StartY=-267.623 StartZ=0 EndX=-235 EndY=-267.623 EndZ=0
    g3: LineSegment StartX=-235 StartY=-267.623 StartZ=0 EndX=-235 EndY=0 EndZ=0
    g4: ArcOfCircle CenterX=0 CenterY=-4.08e-14 CenterZ=0 NormalX=0 NormalY=0 NormalZ=1 AngleXU=0 Radius=166.5 StartAngle=3.14159 EndAngle=6.28319
    g5: ArcOfCircle CenterX=200 CenterY=-40 CenterZ=0 NormalX=0 NormalY=0 NormalZ=1 AngleXU=0 Radius=7 StartAngle=3e-16 EndAngle=3.14159
    g6: ArcOfCircle CenterX=200 CenterY=-60 CenterZ=0 NormalX=0 NormalY=0 NormalZ=1 AngleXU=0 Radius=7 StartAngle=3.14159 EndAngle=6.28319
    g7: LineSegment StartX=193 StartY=-40 StartZ=0 EndX=193 EndY=-60 EndZ=0
    g8: LineSegment StartX=207 StartY=-60 StartZ=0 EndX=207 EndY=-40 EndZ=0
    g9: ArcOfCircle CenterX=200 CenterY=-210 CenterZ=0 NormalX=0 NormalY=0 NormalZ=1 AngleXU=0 Radius=7 StartAngle=0 EndAngle=3.14159
    g10: ArcOfCircle CenterX=200 CenterY=-230 CenterZ=0 NormalX=0 NormalY=0 NormalZ=1 AngleXU=0 Radius=7 StartAngle=3.14159 EndAngle=6.28319
    g11: LineSegment StartX=193 StartY=-210 StartZ=0 EndX=193 EndY=-230 EndZ=0
    g12: LineSegment StartX=207 StartY=-230 StartZ=0 EndX=207 EndY=-210 EndZ=0
    g13: ArcOfCircle CenterX=-200 CenterY=-40 CenterZ=0 NormalX=0 NormalY=0 NormalZ=1 AngleXU=0 Radius=7 StartAngle=0 EndAngle=3.14159
    g14: ArcOfCircle CenterX=-200 CenterY=-60 CenterZ=0 NormalX=0 NormalY=0 NormalZ=1 AngleXU=0 Radius=7 StartAngle=3.14159 EndAngle=6.28319
    g15: LineSegment StartX=-207 StartY=-40 StartZ=0 EndX=-207 EndY=-60 EndZ=0
    g16: LineSegment StartX=-193 StartY=-60 StartZ=0 EndX=-193 EndY=-40 EndZ=0
    g17: ArcOfCircle CenterX=-200 CenterY=-210 CenterZ=0 NormalX=0 NormalY=0 NormalZ=1 AngleXU=0 Radius=7 StartAngle=1.4e-15 EndAngle=3.14159
    g18: ArcOfCircle CenterX=-200 CenterY=-230 CenterZ=0 NormalX=0 NormalY=0 NormalZ=1 AngleXU=0 Radius=7 StartAngle=3.14159 EndAngle=6.28319
    g19: LineSegment StartX=-207 StartY=-210 StartZ=0 EndX=-207 EndY=-230 EndZ=0
    g20: LineSegment StartX=-193 StartY=-230 StartZ=0 EndX=-193 EndY=-210 EndZ=0
    g21: LineSegment StartX=166.5 StartY=-4.08e-14 StartZ=0 EndX=235 EndY=0 EndZ=0
    g22: ArcOfCircle CenterX=0 CenterY=-210 CenterZ=0 NormalX=0 NormalY=0 NormalZ=1 AngleXU=0 Radius=7 StartAngle=-9e-16 EndAngle=3.14159
    g23: ArcOfCircle CenterX=0 CenterY=-230 CenterZ=0 NormalX=0 NormalY=0 NormalZ=1 AngleXU=0 Radius=7 StartAngle=3.14159 EndAngle=6.28319
    g24: LineSegment StartX=-7 StartY=-210 StartZ=0 EndX=-7 EndY=-230 EndZ=0
    g25: LineSegment StartX=7 StartY=-230 StartZ=0 EndX=7 EndY=-210 EndZ=0
  constraints (65):
    c: Coincident(g21,g1)
    c: Coincident(g1,g2)
    c: Coincident(g2,g3)
    c: Coincident(g3,g0)
    c: Horizontal(g2)
    c: Vertical(g1)
    c: Vertical(g3)
    c: Coincident(g21,g-3)
    c: Coincident(g0,g-4)
    c: Coincident(g4,g-1)
    c: Horizontal(g4,g4)
    c: Horizontal(g4,g4)
    c: Tangent(g5,g7) = -1.5708
    c: Tangent(g7,g6) = -1.5708
    c: Tangent(g6,g8) = -1.5708
    c: Tangent(g8,g5) = -1.5708
    c: Equal(g5,g6)
    c: Vertical(g7)
    c: DistanceY(g8,g8) = 20
    c: DistanceX(g5,g5) = 14
    c: Vertical(g5,g-5)
    c: DistanceY(g5,g4) = 40
    c: Tangent(g9,g11) = -1.5708
    c: Tangent(g11,g10) = -1.5708
    c: Tangent(g10,g12) = -1.5708
    c: Tangent(g12,g9) = -1.5708
    c: Equal(g9,g10)
    c: Vertical(g11)
    c: Equal(g8,g12) = 20
    c: Equal(g5,g9) = 14
    c: Vertical(g6,g9)
    c: Tangent(g13,g15) = -1.5708
    c: Tangent(g15,g14) = -1.5708
    c: Tangent(g14,g16) = -1.5708
    c: Tangent(g16,g13) = -1.5708
    c: Equal(g13,g14)
    c: Vertical(g15)
    c: Equal(g8,g16) = 20
    c: Equal(g5,g13) = 14
    c: Tangent(g17,g19) = -1.5708
    c: Tangent(g19,g18) = -1.5708
    c: Tangent(g18,g20) = -1.5708
    c: Tangent(g20,g17) = -1.5708
    c: Equal(g17,g18)
    c: Vertical(g19)
    c: Equal(g16,g20) = 20
    c: Equal(g13,g17) = 14
    c: Vertical(g14,g17)
    c: Tangent(g22,g24) = -1.5708
    c: Tangent(g24,g23) = -1.5708
    c: Tangent(g23,g25) = -1.5708
    c: Tangent(g25,g22) = -1.5708
    c: Equal(g22,g23)
    c: Vertical(g24)
    c: DistanceX(g22,g22) = 14
    c: DistanceY(g24,g24) = 20
    c: PointOnObject(g22,g-2)
    c: Horizontal(g9,g22)
    c: DistanceY(g9,g5) = 170
    c: DistanceY(g17,g13) = 170
    c: DistanceX(g14,g6) = 400
    c: DistanceY(g13,g0) = 40
    c: Coincident(g0,g4)
    c: Coincident(g4,g21)
    c: Radius(g4) = 166.5
FEATURE [Part::Extrusion] Extrude011
  Base = -> Sketch012
  Dir = (0,-1,2e-16)
  DirMode = 2
  FaceMakerClass = Part::FaceMakerBullseye
  LengthFwd = 10
  LengthRev = 0
  Solid = true
  Symmetric = false
FEATURE [App::Part] Part004  label="pipeBrg"
  Group = -> [Sketch011,Sketch012,Extrude005,Extrude011]
  Origin = -> Origin009
  Placement = pos=(0,-1538.75,1787.43) rot=(0,0,1;0rad)
FEATURE [Part::Compound] Compound024  label="Brg"
  Links = -> [Part004]
  Placement = pos=(-8.34222,5.69e-13,72.567) rot=(0,0,1;1.5708rad)
FEATURE [Part::Compound] Compound001  label="centerWell"
  Links = -> [Cut003,Extrude001,Cut005]
FEATURE [Sketcher::SketchObject] Sketch013
  ExternalGeometry = -> [Compound001]
  FullyConstrained = false
  sketch-geometry (4):
    g0: LineSegment StartX=1549.19 StartY=50 StartZ=0 EndX=1757.19 EndY=50 EndZ=0
    g1: LineSegment StartX=1757.19 StartY=50 StartZ=0 EndX=1757.19 EndY=-50 EndZ=0
    g2: LineSegment StartX=1757.19 StartY=-50 StartZ=0 EndX=1549.19 EndY=-50 EndZ=0
    g3: ArcOfCircle CenterX=-0.000694137 CenterY=-2.8392e-12 CenterZ=0 NormalX=0 NormalY=0 NormalZ=1 AngleXU=0 Radius=1550 StartAngle=6.25092 EndAngle=6.31545
  constraints (12):
    c: Horizontal(g0)
    c: Coincident(g0,g1)
    c: Vertical(g1)
    c: Coincident(g1,g2)
    c: Horizontal(g2)
    c: DistanceY(g-1,g0) = 50
    c: DistanceY(g1,g1) = 100
    c: Coincident(g3,g2)
    c: Coincident(g3,g0)
    c: PointOnObject(g0,g-5)
    c: PointOnObject(g2,g-6)
    c: DistanceX(g0,g0) = 208
FEATURE [Part::Extrusion] Extrude012
  Base = -> Sketch013
  Dir = (0,0,1)
  DirMode = 2
  FaceMakerClass = Part::FaceMakerBullseye
  LengthFwd = 10
  LengthRev = 0
  Solid = true
  Symmetric = false
FEATURE [Sketcher::SketchObject] Sketch014
  ExternalGeometry = -> [Extrude012,Compound001]
  FullyConstrained = true
  MapMode = 5
  Placement = pos=(0,0,10) rot=(0,0,1;0rad)
  Support = -> [Extrude012]
  sketch-geometry (8):
    g0: LineSegment StartX=1549.19 StartY=50 StartZ=0 EndX=1757.19 EndY=50 EndZ=0
    g1: LineSegment StartX=1757.19 StartY=50 StartZ=0 EndX=1757.19 EndY=45 EndZ=0
    g2: LineSegment StartX=1757.19 StartY=45 StartZ=0 EndX=1549.19 EndY=45 EndZ=0
    g3: LineSegment StartX=1549.19 StartY=45 StartZ=0 EndX=1549.19 EndY=50 EndZ=0
    g4: LineSegment StartX=1549.19 StartY=-50 StartZ=0 EndX=1757.19 EndY=-50 EndZ=0
    g5: LineSegment StartX=1757.19 StartY=-50 StartZ=0 EndX=1757.19 EndY=-45 EndZ=0
    g6: LineSegment StartX=1757.19 StartY=-45 StartZ=0 EndX=1549.19 EndY=-45 EndZ=0
    g7: LineSegment StartX=1549.19 StartY=-45 StartZ=0 EndX=1549.19 EndY=-50 EndZ=0
  constraints (22):
    c: Coincident(g0,g1)
    c: Coincident(g1,g2)
    c: Coincident(g2,g3)
    c: Coincident(g3,g0)
    c: Horizontal(g0)
    c: Horizontal(g2)
    c: Vertical(g1)
    c: Vertical(g3)
    c: Coincident(g4,g5)
    c: Coincident(g5,g6)
    c: Coincident(g6,g7)
    c: Coincident(g7,g4)
    c: Horizontal(g4)
    c: Horizontal(g6)
    c: Vertical(g5)
    c: Vertical(g7)
    c: Coincident(g0,g-3)
    c: DistanceY(g1,g1) = 5
    c: DistanceY(g5,g5) = 5
    c: Coincident(g4,g-3)
    c: Vertical(g2,g6)
    c: PointOnObject(g4,g-4)
FEATURE [Part::Extrusion] Extrude013
  Base = -> Sketch014
  Dir = (0,0,1)
  DirMode = 2
  FaceMakerClass = Part::FaceMakerBullseye
  LengthFwd = 200
  LengthRev = 0
  Solid = true
  Symmetric = false
FEATURE [Part::Chamfer] Chamfer
  Base = -> Extrude013
  Edges = 2 edges: [Edge7 r1=130 r2=70,Edge19 r1=130 r2=70]
FEATURE [Part::Compound] Compound002  label="gusset"
  Links = -> [Extrude012,Chamfer]
FEATURE [Sketcher::SketchObject] Sketch015
  ExternalGeometry = -> [Compound002]
  FullyConstrained = true
  MapMode = 5
  Placement = pos=(0,0,10) rot=(0,0,1;0rad)
  Support = -> [Compound002]
  sketch-geometry (1):
    g0: Circle CenterX=1732.19 CenterY=0 CenterZ=0 NormalX=0 NormalY=0 NormalZ=1 AngleXU=0 Radius=7
  constraints (3):
    c: Diameter(g0) = 14
    c: PointOnObject(g0,g-1)
    c: Distance(g0,g-3) = 25
FEATURE [Part::Extrusion] Extrude014
  Base = -> Sketch015
  Dir = (0,0,1)
  DirMode = 2
  FaceMakerClass = Part::FaceMakerBullseye
  LengthFwd = 10
  LengthRev = 0
  Reversed = true
  Solid = true
  Symmetric = false
FEATURE [Part::Cut] Cut006
  Base = -> Compound002
  Placement = pos=(0,0,1200) rot=(0,0,1;0rad)
  Tool = -> Extrude014
  expr: .Placement.Base.z = Spreadsheet001.h1
FEATURE [Spreadsheet::Sheet] Spreadsheet002  label="Spreadsheet_support"
  cells = A1='tankDia   D; B1(D0)=15500; A2='梁成H0; B2(H0)=600; A3='梁長L0; B3(L0)==D0 - 500; A4='玄材shp; B4(shp)='50x50x6; A5='玄材ゲージラインGL0; B5(GL0)=30; A6='ラチス材Lshp; B6(Lshp)='6x38; A7='ラチス材幅Lb0; B7(Lb0)=38; A8='ラチス材厚Lt0; B8(Gt0)=6; A9='ガセットプレート幅Gb0; B9(Gb0)=120; A10='ラチスピッチrp0; B10(rp0)==(L0 - 2 * Gb0) / rn0; A11='ラチス配列数rn0; B11(rn0)==D0 / H0; B16='t; C16='A; D16='GLine; A17='40x40x3; B17=3; C17=40; D17=22; A18='40x40x5; B18=5; C18=40; D18=22; A19='50x50x4; B19=4; C19=50; D19=30; A20='50x50x6; B20=6; C20=50; D20=30; A21='65x65x6; B21=6; C21=65; D21=35; A22='65x65x8; B22=8; C22=65; D22=35; A23='75x75x6; B23=6; C23=75; D23=40; A24='75x75x9; B24=9; C24=75; D24=40; A25='75x75x12; B25=12; C25=75; D25=40; A26='90x90x7; B26=7; C26=90; D26=50; A27='90x90x10; B27=10; C27=90; D27=50; A28='90x90x13; B28=13; C28=90; D28=50; A29='100x100x7; B29=7; C29=100; D29=55; A30='100x100x10; B30=10; C30=100; D30=55; A31='100x100x13; B31=13; C31=100; D31=55; A34='6x38; B34=6; C34=38; A35='9x38; B35=9; C35=38; A36='6x44; B36=6; C36=44; A37='9x44; B37=9; C37=44; A38='4.5x50; B38=4.5; C38=50; A39='6x50; B39=6; C39=50; A40='9x50; B40=9; C40=50; A41='6x65; B41=6; C41=65; A42='9x65; B42=9; C42=65; A43='6x75; B43=6; C43=75; A44='9x75; B44=9; C44=75; A45='6x90; B45=6; C45=90; A46='9x90; B46=9; C46=90
FEATURE [Part::FeaturePython] AngleSteel005  label="AngleSteel002"  # WARN: FeaturePython — macro-defined, semantics opaque (R4)
  A = 50
  B = 50
  L = 1000
  Placement = pos=(0,28.8,14.4) rot=(0,0,1;1.5708rad)
  Solid = false
  g0 = 7.85
  mass = 0
  size = 7
  standard = SS_Equal
  t = 8
FEATURE [Part::Mirroring] Mirror011  label="AngleSteel (mirrored)"
  Base = (-2.54e-14,114.396,14.3963)
  Normal = (0,0,-1)
  Placement = pos=(0,0,600) rot=(0,0,1;0rad)
  Source = -> AngleSteel005
  expr: .Placement.Base.z = Spreadsheet002.H0
FEATURE [Part::Extrusion] Extrude017
  Base = -> AngleSteel005
  Dir = (-1,2e-16,0)
  DirMode = 2
  FaceMakerClass = Part::FaceMakerBullseye
  LengthFwd = 15000
  LengthRev = 0
  Reversed = true
  Solid = false
  Symmetric = false
  expr: LengthFwd = Spreadsheet002.L0
FEATURE [Part::Extrusion] Extrude018
  Base = -> Mirror011
  Dir = (-1,2e-16,0)
  DirMode = 2
  FaceMakerClass = Part::FaceMakerBullseye
  LengthFwd = 15000
  LengthRev = 0
  Reversed = true
  Solid = false
  Symmetric = false
  expr: LengthFwd = Spreadsheet002.L0
FEATURE [Sketcher::SketchObject] Sketch016
  ExternalGeometry = -> [Extrude018,Extrude017]
  FullyConstrained = false
  Placement = pos=(0,0,0) rot=(1,0,0;1.5708rad)
  expr: Constraints[2] = Spreadsheet002.Gb0
  expr: Constraints[5] = Spreadsheet002.rp0
  expr: Constraints[8] = Spreadsheet002.H0 - 60
  sketch-geometry (3):
    g0: LineSegment StartX=120 StartY=44.4 StartZ=0 EndX=405.677 EndY=584.4 EndZ=0
    g1: LineSegment StartX=405.677 StartY=584.4 StartZ=0 EndX=691.355 EndY=44.4 EndZ=0
    g2: LineSegment StartX=405.677 StartY=584.4 StartZ=0 EndX=405.677 EndY=511.834 EndZ=0
  constraints (9):
    c: Coincident(g0,g1)
    c: Horizontal(g0,g1)
    c: DistanceX(g-1,g0) = 120
    c: Coincident(g2,g0)
    c: Symmetric(g1,g0,g2)
    c: DistanceX(g0,g1) = 571.355
    c: DistanceY(g-1,g-4) = 14.4
    c: DistanceY(g-4,g0) = 30
    c: DistanceY(g0,g0) = 540
FEATURE [Sketcher::SketchObject] Sketch017
  ExternalGeometry = -> [Sketch016,Extrude017]
  FullyConstrained = true
  Placement = pos=(0,0,14.4) rot=(1,0,0;1.5708rad)
  expr: Constraints[23] = Spreadsheet002.Lb0
  expr: Constraints[24] = Spreadsheet002.H0 - 20
  expr: Constraints[25] = Spreadsheet002.Lb0 / 2
  sketch-geometry (9):
    g0: LineSegment StartX=120 StartY=70.6308 StartZ=0 EndX=394.763 EndY=590 EndZ=0
    g1: LineSegment StartX=405.677 StartY=529.369 StartZ=0 EndX=130.914 EndY=10 EndZ=0
    g2: LineSegment StartX=405.677 StartY=529.369 StartZ=0 EndX=680.44 EndY=10 EndZ=0
    g3: LineSegment StartX=691.355 StartY=70.6308 StartZ=0 EndX=416.592 EndY=590 EndZ=0
    g4: LineSegment StartX=394.763 StartY=590 StartZ=0 EndX=416.592 EndY=590 EndZ=0
    g5: LineSegment StartX=680.44 StartY=10 StartZ=0 EndX=691.355 EndY=10 EndZ=0
    g6: LineSegment StartX=691.355 StartY=10 StartZ=0 EndX=691.355 EndY=70.6308 EndZ=0
    g7: LineSegment StartX=130.914 StartY=10 StartZ=0 EndX=120 EndY=10 EndZ=0
    g8: LineSegment StartX=120 StartY=10 StartZ=0 EndX=120 EndY=70.6308 EndZ=0
  constraints (27):
    c: Coincident(g7,g8)
    c: Coincident(g0,g8)
    c: Coincident(g1,g7)
    c: Coincident(g0,g4)
    c: Coincident(g1,g2)
    c: Coincident(g3,g4)
    c: Coincident(g2,g5)
    c: Coincident(g5,g6)
    c: Coincident(g3,g6)
    c: Horizontal(g7)
    c: Horizontal(g4)
    c: Vertical(g8)
    c: Vertical(g7,g-4)
    c: Horizontal(g0,g3)
    c: Horizontal(g5)
    c: Horizontal(g1,g2)
    c: Vertical(g6)
    c: PointOnObject(g-3,g6)
    c: Parallel(g1,g-4)
    c: Parallel(g1,g0)
    c: Parallel(g2,g-3)
    c: Parallel(g-3,g3)
    c: Vertical(g1,g-4)
    c: Distance(g1,g0) = 38
    c: DistanceY(g2,g3) = 580
    c: Distance(g1,g-4) = 19
    c: DistanceY(g-5,g7) = 10
FEATURE [Part::Extrusion] Extrude015
  Base = -> Sketch017
  Dir = (0,-1,2e-16)
  DirMode = 2
  FaceMakerClass = Part::FaceMakerBullseye
  LengthFwd = 6
  LengthRev = 0
  Placement = pos=(0,28.8,0) rot=(0,0,1;0rad)
  Solid = true
  Symmetric = false
FEATURE [Part::FeaturePython] Array016  label="Array001"  # Draft array (typed FeaturePython)
  AlwaysSyncPlacement = false
  Angle = 360
  ArrayType = 0
  Axis = (0,0,1)
  Base = -> Extrude015
  Center = (0,0,0)
  Count = 26
  ExpandArray = false
  Fuse = false
  IntervalAxis = (0,0,0)
  IntervalX = (571.355,0,0)
  IntervalY = (0,100,0)
  IntervalZ = (0,0,100)
  NumberCircles = 3
  NumberPolar = 5
  NumberX = 26
  NumberY = 1
  NumberZ = 1
  PlacementList = 26 placements: arithmetic series from (0,28.8,0) step (571.355,0,0) to (14283.9,28.8,0)
  RadialDistance = 50
  ScaleList = (26) [(1,1,1),(1,1,1),(1,1,1),(1,1,1),(1,1,1),(1,1,1),(1,1,1),(1,1,1),(1,1,1),(1,1,1),(1,1,1),(1,1,1),(1,1,1),(1,1,1),(1,1,1),(1,1,1),(1,1,1),(1,1,1),+8 more]
  Symmetry = 1
  TangentialDistance = 25
  expr: .IntervalX.x = Spreadsheet002.rp0
  expr: NumberX = Spreadsheet002.rn0
FEATURE [Sketcher::SketchObject] Sketch018
  ExternalGeometry = -> [Extrude015]
  FullyConstrained = true
  Placement = pos=(0,0,14.4) rot=(1,0,0;1.5708rad)
  expr: Constraints[22] = Spreadsheet002.L0
  sketch-geometry (8):
    g0: LineSegment StartX=0 StartY=10 StartZ=0 EndX=120 EndY=10 EndZ=0
    g1: LineSegment StartX=120 StartY=10 StartZ=0 EndX=120 EndY=590 EndZ=0
    g2: LineSegment StartX=120 StartY=590 StartZ=0 EndX=0 EndY=590 EndZ=0
    g3: LineSegment StartX=0 StartY=590 StartZ=0 EndX=0 EndY=10 EndZ=0
    g4: LineSegment StartX=15000 StartY=590 StartZ=0 EndX=14880 EndY=590 EndZ=0
    g5: LineSegment StartX=14880 StartY=590 StartZ=0 EndX=14880 EndY=10 EndZ=0
    g6: LineSegment StartX=14880 StartY=10 StartZ=0 EndX=15000 EndY=10 EndZ=0
    g7: LineSegment StartX=15000 StartY=10 StartZ=0 EndX=15000 EndY=590 EndZ=0
  constraints (23):
    c: Coincident(g0,g1)
    c: Coincident(g1,g2)
    c: Coincident(g2,g3)
    c: Coincident(g3,g0)
    c: Horizontal(g0)
    c: Horizontal(g2)
    c: Vertical(g1)
    c: Vertical(g3)
    c: Vertical(g-1,g0)
    c: Coincident(g0,g-3)
    c: Horizontal(g1,g-4)
    c: Coincident(g4,g5)
    c: Coincident(g5,g6)
    c: Coincident(g6,g7)
    c: Coincident(g7,g4)
    c: Horizontal(g4)
    c: Horizontal(g6)
    c: Vertical(g5)
    c: Vertical(g7)
    c: Equal(g0,g6)
    c: Horizontal(g6,g0)
    c: Horizontal(g1,g4)
    c: DistanceX(g0,g6) = 15000
FEATURE [Part::Extrusion] Extrude016
  Base = -> Sketch018
  Dir = (0,-1,2e-16)
  DirMode = 2
  FaceMakerClass = Part::FaceMakerBullseye
  LengthFwd = 6
  LengthRev = 0
  Placement = pos=(0,28.8,0) rot=(0,0,1;0rad)
  Solid = true
  Symmetric = false
  expr: LengthFwd = Spreadsheet002.Gt0
FEATURE [Part::MultiFuse] Fusion001
  Shapes = -> [Extrude018,Extrude017]
FEATURE [Part::Mirroring] Mirror001  label="Fusion (mirrored)"
  Base = (-3.2e-15,28.7963,514.396)
  Normal = (0,-1,0)
  Placement = pos=(0,-6,0) rot=(0,0,1;0rad)
  Source = -> Fusion001
  expr: .Placement.Base.y = -Spreadsheet002.Gt0
FEATURE [Sketcher::SketchObject] Sketch019
  FullyConstrained = true
  Placement = pos=(0,0,0) rot=(1,0,0;1.5708rad)
  sketch-geometry (4):
    g0: LineSegment StartX=0 StartY=0 StartZ=0 EndX=150 EndY=0 EndZ=0
    g1: LineSegment StartX=150 StartY=0 StartZ=0 EndX=150 EndY=300 EndZ=0
    g2: LineSegment StartX=150 StartY=300 StartZ=0 EndX=0 EndY=300 EndZ=0
    g3: LineSegment StartX=0 StartY=300 StartZ=0 EndX=0 EndY=0 EndZ=0
  constraints (11):
    c: Coincident(g0,g1)
    c: Coincident(g1,g2)
    c: Coincident(g2,g3)
    c: Coincident(g3,g0)
    c: Horizontal(g0)
    c: Horizontal(g2)
    c: Vertical(g1)
    c: Vertical(g3)
    c: Coincident(g0,g-1)
    c: DistanceX(g2,g2) = 150
    c: DistanceY(g1,g1) = 300
FEATURE [Part::Extrusion] Extrude019
  Base = -> Sketch019
  Dir = (0,-1,-3e-16)
  DirMode = 2
  FaceMakerClass = Part::FaceMakerBullseye
  LengthFwd = 6
  LengthRev = 0
  Solid = true
  Symmetric = true
FEATURE [Part::FeaturePython] AngleSteel006  label="AngleSteel003"  # WARN: FeaturePython — macro-defined, semantics opaque (R4)
  A = 75
  B = 75
  L = 300
  Placement = pos=(117.5,40.5,0) rot=(0,0,1;3.14159rad)
  Solid = true
  g0 = 7.85
  mass = 2.05506
  size = 10
  standard = SS_Equal
  t = 6
FEATURE [Part::Mirroring] Mirror004  label="AngleSteel003 (mirrored)"
  Base = (200,0,0)
  Normal = (0,1,0)
  Source = -> AngleSteel006
FEATURE [Part::Compound] Compound025  label="gusset001"
  Links = -> [Extrude019,Mirror004,AngleSteel006]
  Placement = pos=(7450,-1710,750) rot=(0,0,1;0rad)
  expr: .Placement.Base.x = Spreadsheet001.D0 / 2 - 300
  expr: .Placement.Base.y = -<<Spreadsheet_feedWell>>.dia / 2 - 160
  expr: .Placement.Base.z = Spreadsheet001.h1 - 450
FEATURE [Part::Compound] Compound026
  Links = -> [Mirror001,Fusion001]
FEATURE [App::Part] Part007  label="latticeBeam"
  Group = -> [Sketch016,Sketch018,Sketch017,Fusion001,Mirror011,Mirror001,Extrude015,Extrude016,Extrude018,Extrude017,Array016,AngleSteel005,Compound026]
  Origin = -> Origin003
  Placement = pos=(-7500,-1730,785) rot=(0,0,1;0rad)
  expr: .Placement.Base.x = -Spreadsheet002.L0 / 2
  expr: .Placement.Base.y = -Spreadsheet001.dia / 2 - 180
  expr: .Placement.Base.z = Spreadsheet001.h1 - 415
FEATURE [Part::Mirroring] Mirror012  label="latticeBeam (mirrored)"
  Base = (-1000,0,0)
  Normal = (0,1,0)
  Source = -> Part007
FEATURE [App::Part] Part006  label="support"
  Group = -> [Part007,Mirror012]
  Origin = -> Origin011
  Placement = pos=(0,0,-200) rot=(0,0,1;0rad)
FEATURE [Part::FeaturePython] Array017  # Draft array (typed FeaturePython)
  AlwaysSyncPlacement = false
  Angle = 360
  ArrayType = 1
  Axis = (0,0,1)
  Base = -> Cut006
  Center = (0,0,0)
  Count = 4
  ExpandArray = false
  Fuse = false
  IntervalAxis = (0,0,0)
  IntervalX = (50,0,0)
  IntervalY = (0,50,0)
  IntervalZ = (0,0,50)
  NumberCircles = 3
  NumberPolar = 4
  NumberX = 2
  NumberY = 2
  NumberZ = 1
  PlacementList = 4 placements: [(0,0,1200),(0,0,1200),(0,0,1200),(0,0,1200)]
  RadialDistance = 50
  ScaleList = (4) [(1,1,1),(1,1,1),(1,1,1),(1,1,1)]
  Symmetry = 1
  TangentialDistance = 25
FEATURE [App::Part] Part005  label="centerWell001"
  Group = -> [Chamfer,Sketch005,Sketch015,Sketch014,Sketch013,Compound001,Compound002,Revolve,Revolve001,Revolve002,Extrude001,Extrude013,Extrude004,Extrude003,Extrude010,Extrude002,Extrude012,Extrude014,Sketch001,Sketch003,Sketch,Sketch002,Sketch004,AngleSteel003,AngleSteel004,Cut006,Fusion,Cut004,Cut003,Cut005,Array017]
  Origin = -> Origin010
  Placement = pos=(0,0,0) rot=(0,0,1;1.5708rad)
FEATURE [Part::Mirroring] Mirror013  label="gusset001 (mirrored)"
  Base = (0,0,0)
  Normal = (1,0,0)
  Source = -> Compound025
FEATURE [Part::Mirroring] Mirror014  label="gusset001 (mirrored) (mirrored)"
  Base = (0,0,0)
  Normal = (0,1,0)
  Source = -> Mirror013
FEATURE [Part::Mirroring] Mirror015  label="gusset001 (mirrored)001"
  Base = (0,0,0)
  Normal = (0,1,0)
  Source = -> Compound025
FEATURE [Part::FeaturePython] ChannelSteel004  label="ChannelSteel"  # WARN: FeaturePython — macro-defined, semantics opaque (R4)
  B = 65
  H = 125
  L = 3400
  Placement = pos=(1720,-1701.5,3.61e-13) rot=(-1,0,0;1.5708rad)
  Solid = true
  g0 = 7.85
  mass = 41.0702
  size = 2
  standard = SS
  t1 = 6
  t2 = 8
  expr: .Placement.Base.x = Spreadsheet001.dia / 2 + 170
  expr: .Placement.Base.y = -Spreadsheet001.dia / 2 - 101.5 - 50
  expr: L = Spreadsheet001.dia + 300
FEATURE [Part::FeaturePython] Array002  # Draft array (typed FeaturePython)
  AlwaysSyncPlacement = false
  Angle = 360
  ArrayType = 0
  Axis = (0,0,1)
  Base = -> ChannelSteel004
  Center = (0,0,0)
  Count = 2
  ExpandArray = false
  Fuse = false
  IntervalAxis = (0,0,0)
  IntervalX = (2975,0,0)
  IntervalY = (0,100,0)
  IntervalZ = (0,0,100)
  NumberCircles = 3
  NumberPolar = 5
  NumberX = 2
  NumberY = 1
  NumberZ = 1
  Placement = pos=(0,-0.000129987,1135.41) rot=(0,0,1;0rad)
  PlacementList = 2 placements: [(1720,-1701.5,3.61e-13),(4695,-1701.5,3.61e-13)]
  RadialDistance = 50
  ScaleList = (2) [(1,1,1),(1,1,1)]
  Symmetry = 1
  TangentialDistance = 25
  expr: .IntervalX.x = (<<Spreadsheet_support>>.L0 / 2 - <<Spreadsheet_feedWell>>.dia / 2) / 2
FEATURE [Part::Mirroring] Mirror016  label="Array002 (mirrored)"
  Base = (0,0,0)
  Normal = (1,0,0)
  Source = -> Array002
FEATURE [Sketcher::SketchObject] Sketch020
  FullyConstrained = true
  expr: Constraints[10] = Spreadsheet003.l0
  expr: Constraints[9] = Spreadsheet003.w0
  sketch-geometry (5):
    g0: LineSegment StartX=0 StartY=0 StartZ=0 EndX=2870 EndY=0 EndZ=0
    g1: LineSegment StartX=2870 StartY=0 StartZ=0 EndX=2870 EndY=3350 EndZ=0
    g2: LineSegment StartX=2870 StartY=3350 StartZ=0 EndX=0 EndY=3350 EndZ=0
    g3: LineSegment StartX=0 StartY=3350 StartZ=0 EndX=0 EndY=0 EndZ=0
    g4: LineSegment StartX=0 StartY=0 StartZ=0 EndX=2870 EndY=3350 EndZ=0
  constraints (14):
    c: Coincident(g0,g1)
    c: Coincident(g1,g2)
    c: Coincident(g2,g3)
    c: Coincident(g3,g0)
    c: Horizontal(g0)
    c: Horizontal(g2)
    c: Vertical(g1)
    c: Vertical(g3)
    c: Coincident(g0,g-1)
    c: Distance(g2) = 2870
    c: Distance(g1) = 3350
    c: Coincident(g4,g0)
    c: Coincident(g4,g1)
    c: Angle(g0,g4) = 0.862416
FEATURE [Spreadsheet::Sheet] Spreadsheet003  label="Spreadsheet001"
  cells = A2='rodDia dia; B2(dia)=12; C2='thickness; D2(t0)=6; E2='w0; F2(w0)=2870; G2='sita; H2(sita)==atan(l0 / w0); A3='length L0; B3(L0)==(w0 ^ 2 + l0 ^ 2) ^ 0.5; C3='l1; D3(l1)==L0 - (dia * 5 + 500); E3='l0; F3(l0)=3350; B4='l; C4='l1; D4='a; E4='b; F4='c; G4='e; H4='f; I4='g; J4='h; K4='i; L4='r; A5='forkEndR; B5=80; D5=25; E5=10; F5=14; G5=16; H5=13; I5=40; J5=5; K5=13; L5=15; A6='turnBackle; B6=100; C6=20; D6=30; E6=16; F6=22; A7='forkEndL; B7=60; D7=25; E7=10; F7=13; G7=16; H7=13; I7=20; L7=15; A8=1; B8=2; C8=3; D8=4; E8=5; F8=6; G8=7; H8=8; I8=9; J8=10; K8=11; L8=12; A9='turnBackle; A10='d; B10='l; C10='l1; D10='a; E10='b; F10='c; G10='t0; A11=10; B11=75; C11=15; D11=24; E11=13; F11=17; G11=6; A12=12; B12=100; C12=20; D12=30; E12=16; F12=22; G12=6; A13=16; B13=125; C13=24; D13=36; E13=20; F13=27; G13=9; A14=20; B14=150; C14=28; D14=42; E14=23; F14=33; G14=9; A15=22; B15=175; C15=33; D15=48; E15=27; F15=37; G15=9; A16=24; B16=200; C16=38; D16=54; E16=30; F16=42; G16=12; A17=30; B17=250; C17=47; D17=66; E17=37; F17=52; G17=12; A18='forkEnd_L; A19='d; B19='l; C19='a; D19='b; E19='c; F19='e; G19='f; H19='g; I19='r; A20=10; B20=50; C20=20; D20=7; E20=10; F20=12; G20=10; H20=15; I20=12; A21=12; B21=60; C21=25; D21=10; E21=13; F21=16; G21=13; H21=20; I21=15; A22=16; B22=75; C22=30; D22=13; E22=16; F22=20; G22=16; H22=25; I22=19; A23=20; B23=90; C23=40; D23=16; E23=20; F23=24; G23=20; H23=30; I23=23; A24=22; B24=100; C24=45; D24=20; E24=23; F24=28; G24=23; H24=35; I24=27; A25=24; B25=115; C25=50; D25=23; E25=26; F25=32; G25=26; H25=40; I25=30; A26=30; B26=140; C26=65; D26=30; E26=33; F26=40; G26=33; H26=50; I26=38; A27='forkEnd_R; A28='d; B28='l; C28='a; D28='b; E28='c; F28='r; +82 more cells
FEATURE [Sketcher::SketchObject] Sketch021
  FullyConstrained = true
  Placement = pos=(0,0,0) rot=(1,0,0;1.5708rad)
  expr: Constraints[11] = Spreadsheet003.I5 + Spreadsheet003.dia * 2
  expr: Constraints[1] = Spreadsheet003.F5 / 2
  expr: Constraints[3] = Spreadsheet003.L5
  sketch-geometry (5):
    g0: Circle CenterX=0 CenterY=0 CenterZ=0 NormalX=0 NormalY=0 NormalZ=1 AngleXU=0 Radius=7
    g1: ArcOfCircle CenterX=0 CenterY=0 CenterZ=0 NormalX=0 NormalY=0 NormalZ=1 AngleXU=0 Radius=15 StartAngle=4.71239 EndAngle=7.85398
    g2: LineSegment StartX=-4.87e-14 StartY=15 StartZ=0 EndX=-64 EndY=15 EndZ=0
    g3: LineSegment StartX=-64 StartY=15 StartZ=0 EndX=-64 EndY=-15 EndZ=0
    g4: LineSegment StartX=-64 StartY=-15 StartZ=0 EndX=0 EndY=-15 EndZ=0
  constraints (12):
    c: Coincident(g0,g-1)
    c: Radius(g0) = 7
    c: Coincident(g1,g0)
    c: Radius(g1) = 15
    c: Horizontal(g2)
    c: Coincident(g2,g3)
    c: Vertical(g3)
    c: Coincident(g3,g4)
    c: Horizontal(g4)
    c: Tangent(g1,g2) = -1.5708
    c: Tangent(g1,g4) = -1.5708
    c: Distance(g2) = 64
FEATURE [Part::Cylinder] Cylinder002  label="円柱001"
  Angle = 360
  AttacherType = Attacher::AttachEngine3D
  FirstAngle = 0
  Height = 500
  Placement = pos=(-24,0,0) rot=(0,-1,0;1.5708rad)
  Radius = 6
  SecondAngle = 0
  expr: .Placement.Base.x = -Spreadsheet003.dia * 2
  expr: Radius = Spreadsheet003.dia / 2
FEATURE [Sketcher::SketchObject] Sketch022
  FullyConstrained = true
  Placement = pos=(0,0,0) rot=(1,0,0;1.5708rad)
  expr: Constraints[10] = Spreadsheet003.C6
  expr: Constraints[11] = Spreadsheet003.B6
  expr: Constraints[12] = Spreadsheet003.D6 / 2
  expr: Constraints[13] = Spreadsheet003.F6 / 2
  expr: Constraints[14] = Spreadsheet003.B6 / 2
  expr: Constraints[17] = Spreadsheet003.C6
  sketch-geometry (6):
    g0: LineSegment StartX=-50 StartY=0 StartZ=0 EndX=-50 EndY=11 EndZ=0
    g1: LineSegment StartX=-50 StartY=11 StartZ=0 EndX=-30 EndY=15 EndZ=0
    g2: LineSegment StartX=-30 StartY=15 StartZ=0 EndX=30 EndY=15 EndZ=0
    g3: LineSegment StartX=30 StartY=15 StartZ=0 EndX=50 EndY=11 EndZ=0
    g4: LineSegment StartX=50 StartY=11 StartZ=0 EndX=50 EndY=0 EndZ=0
    g5: LineSegment StartX=50 StartY=0 StartZ=0 EndX=-50 EndY=0 EndZ=0
  constraints (18):
    c: PointOnObject(g0,g-1)
    c: Vertical(g0)
    c: Coincident(g0,g1)
    c: Coincident(g1,g2)
    c: Horizontal(g2)
    c: Coincident(g2,g3)
    c: Coincident(g3,g4)
    c: PointOnObject(g4,g-1)
    c: Vertical(g4)
    c: Coincident(g4,g5)
    c: DistanceX(g2,g3) = 20
    c: DistanceX(g0,g3) = 100
    c: Distance(g1,g5) = 15
    c: Distance(g4) = 11
    c: DistanceX(g-1,g4) = 50
    c: Horizontal(g0,g3)
    c: Coincident(g5,g0)
    c: DistanceX(g0,g1) = 20
FEATURE [Part::Revolution] Revolve003
  Angle = 360
  Axis = (-1,0,0)
  AxisLink = -> Sketch022 [Edge6]
  Base = (-50,0,0)
  FaceMakerClass = Part::FaceMakerBullseye
  Solid = true
  Source = -> Sketch022
  Symmetric = false
FEATURE [Sketcher::SketchObject] Sketch023
  FullyConstrained = false
  Placement = pos=(0,0,0) rot=(0.57735,0.57735,0.57735;2.0944rad)
  expr: Constraints[16] = Spreadsheet003.F6
  expr: Constraints[17] = Spreadsheet003.F6 / 2
  sketch-geometry (8):
    g0: LineSegment StartX=-11 StartY=39.685 StartZ=0 EndX=-26 EndY=39.685 EndZ=0
    g1: LineSegment StartX=-26 StartY=39.685 StartZ=0 EndX=-26 EndY=-39.3666 EndZ=0
    g2: LineSegment StartX=-26 StartY=-39.3666 StartZ=0 EndX=-11 EndY=-39.3666 EndZ=0
    g3: LineSegment StartX=-11 StartY=-39.3666 StartZ=0 EndX=-11 EndY=39.685 EndZ=0
    g4: LineSegment StartX=11 StartY=39.685 StartZ=0 EndX=26 EndY=39.685 EndZ=0
    g5: LineSegment StartX=26 StartY=39.685 StartZ=0 EndX=26 EndY=-40.315 EndZ=0
    g6: LineSegment StartX=26 StartY=-40.315 StartZ=0 EndX=11 EndY=-40.315 EndZ=0
    g7: LineSegment StartX=11 StartY=-40.315 StartZ=0 EndX=11 EndY=39.685 EndZ=0
  constraints (22):
    c: Coincident(g0,g1)
    c: Coincident(g1,g2)
    c: Coincident(g2,g3)
    c: Coincident(g3,g0)
    c: Horizontal(g0)
    c: Horizontal(g2)
    c: Vertical(g1)
    c: Vertical(g3)
    c: Coincident(g4,g5)
    c: Coincident(g5,g6)
    c: Coincident(g6,g7)
    c: Coincident(g7,g4)
    c: Horizontal(g4)
    c: Horizontal(g6)
    c: Vertical(g5)
    c: Vertical(g7)
    c: DistanceX(g0,g4) = 22
    c: Distance(g-1,g7) = 11
    c: Distance(g5) = 80
    c: Distance(g4) = 15
    c: Distance(g0) = 15
    c: Horizontal(g0,g4)
FEATURE [Part::Extrusion] Extrude020
  Base = -> Sketch023
  Dir = (1,0,0)
  DirMode = 2
  FaceMakerClass = Part::FaceMakerBullseye
  LengthFwd = 300
  LengthRev = 0
  Solid = true
  Symmetric = true
FEATURE [Part::Cut] Cut009
  Base = -> Revolve003
  Tool = -> Extrude020
FEATURE [Sketcher::SketchObject] Sketch024
  FullyConstrained = true
  Placement = pos=(0,0,0) rot=(1,0,0;1.5708rad)
  expr: Constraints[17] = Spreadsheet003.E6
  expr: Constraints[18] = Spreadsheet003.B6 - 2 * Spreadsheet003.C6
  expr: Constraints[19] = (Spreadsheet003.B6 - 2 * Spreadsheet003.C6) / 2
  expr: Constraints[20] = Spreadsheet003.E6 / 2
  sketch-geometry (9):
    g0: LineSegment StartX=30 StartY=3 StartZ=0 EndX=30 EndY=-3 EndZ=0
    g1: LineSegment StartX=25 StartY=-8 StartZ=0 EndX=-25 EndY=-8 EndZ=0
    g2: LineSegment StartX=-30 StartY=-3 StartZ=0 EndX=-30 EndY=3 EndZ=0
    g3: LineSegment StartX=-25 StartY=8 StartZ=0 EndX=25 EndY=8 EndZ=0
    g4: GeomPoint X=0 Y=0 Z=0
    g5: ArcOfCircle CenterX=-25 CenterY=3 CenterZ=0 NormalX=0 NormalY=0 NormalZ=1 AngleXU=0 Radius=5 StartAngle=1.5708 EndAngle=3.14159
    g6: ArcOfCircle CenterX=-25 CenterY=-3 CenterZ=0 NormalX=0 NormalY=0 NormalZ=1 AngleXU=0 Radius=5 StartAngle=3.14159 EndAngle=4.71239
    g7: ArcOfCircle CenterX=25 CenterY=-3 CenterZ=0 NormalX=0 NormalY=0 NormalZ=1 AngleXU=0 Radius=5 StartAngle=4.71239 EndAngle=6.28319
    g8: ArcOfCircle CenterX=25 CenterY=3 CenterZ=0 NormalX=0 NormalY=0 NormalZ=1 AngleXU=0 Radius=5 StartAngle=-4.09e-14 EndAngle=1.5708
  constraints (21):
    c: Horizontal(g1)
    c: Horizontal(g3)
    c: Vertical(g0)
    c: Vertical(g2)
    c: Coincident(g4,g-1)
    c: Tangent(g3,g5) = 1.5708
    c: Tangent(g2,g5) = 1.5708
    c: Tangent(g1,g6) = 1.5708
    c: Tangent(g2,g6) = 1.5708
    c: Tangent(g1,g7) = 1.5708
    c: Tangent(g0,g7) = 1.5708
    c: Tangent(g0,g8) = 1.5708
    c: Tangent(g3,g8) = 1.5708
    c: Radius(g8) = 5
    c: Equal(g8,g7)
    c: Equal(g7,g6)
    c: Equal(g6,g5)
    c: DistanceY(g1,g3) = 16
    c: DistanceX(g2,g0) = 60
    c: Distance(g4,g2) = 30
    c: Distance(g4,g1) = 8
FEATURE [Part::Extrusion] Extrude021
  Base = -> Sketch024
  Dir = (0,-1,2e-16)
  DirMode = 2
  FaceMakerClass = Part::FaceMakerBullseye
  LengthFwd = 60
  LengthRev = 0
  Solid = true
  Symmetric = true
FEATURE [Part::Cut] Cut010
  Base = -> Cut009
  Tool = -> Extrude021
FEATURE [Sketcher::SketchObject] Sketch025
  FullyConstrained = true
  Placement = pos=(0,0,0) rot=(0.57735,0.57735,0.57735;2.0944rad)
  expr: Constraints[1] = Spreadsheet003.dia / 2
  sketch-geometry (1):
    g0: Circle CenterX=0 CenterY=0 CenterZ=0 NormalX=0 NormalY=0 NormalZ=1 AngleXU=0 Radius=6
  constraints (2):
    c: Coincident(g0,g-1)
    c: Radius(g0) = 6
FEATURE [Part::Extrusion] Extrude022
  Base = -> Sketch025
  Dir = (1,0,0)
  DirMode = 2
  FaceMakerClass = Part::FaceMakerBullseye
  LengthFwd = 300
  LengthRev = 0
  Solid = true
  Symmetric = true
FEATURE [Part::Cut] Cut011  label="turnBackle001"
  Base = -> Cut010
  Placement = pos=(-530,0,0) rot=(0,0,1;0rad)
  Tool = -> Extrude022
  expr: .Placement.Base.x = -(Spreadsheet003.dia * 2.5 + 500)
FEATURE [Part::Cylinder] Cylinder003  label="rod001"
  Angle = 360
  AttacherType = Attacher::AttachEngine3D
  FirstAngle = 0
  Height = 3851.28
  Placement = pos=(-536,0,-1.37e-13) rot=(0,-1,0;1.5708rad)
  Radius = 6
  SecondAngle = 0
  expr: .Placement.Base.x = -(Spreadsheet003.dia * 3 + 500)
  expr: Height = Spreadsheet003.l1
  expr: Radius = Spreadsheet003.dia / 2
FEATURE [Part::Extrusion] Extrude023
  Base = -> Sketch021
  Dir = (0,-1,2e-16)
  DirMode = 2
  FaceMakerClass = Part::FaceMakerBullseye
  LengthFwd = 6
  LengthRev = 0
  Placement = pos=(0,9,0) rot=(0,0,1;0rad)
  Solid = true
  Symmetric = true
  expr: .Placement.Base.y = Spreadsheet003.dia / 2 + Spreadsheet003.t0 / 2
  expr: LengthFwd = Spreadsheet003.t0
FEATURE [Part::FeaturePython] Clone001  label="Extrude024"  # Draft clone (typed FeaturePython)
  AttacherType = Attacher::AttachEngine3D
  Fuse = false
  Objects = -> [Extrude023]
  Placement = pos=(-4411.28,9,0) rot=(0,1,0;3.14159rad)
  Scale = (1,1,1)
  expr: .Placement.Base.x = -Spreadsheet003.L0
  expr: .Placement.Base.y = Spreadsheet003.t0 / 2 + Spreadsheet003.dia / 2
FEATURE [Part::Compound] Compound027
  Links = -> [Cylinder002,Extrude023,Cut011,Cylinder003,Clone001]
  Placement = pos=(0,0,0) rot=(1,0,0;1.5708rad)
FEATURE [App::Part] Part010  label="Part"
  Group = -> [Extrude020,Extrude021,Clone001,Cylinder002,Revolve003,Sketch021,Sketch022,Sketch023,Cut010,Cut011,Cut009,Sketch024,Sketch025,Extrude022,Extrude023,Cylinder003,Compound027]
  Origin = -> Origin013
  Placement = pos=(0,0,0) rot=(0,0,1;4.00401rad)
  expr: .Placement.Rotation.Angle = 180 ° + Spreadsheet003.sita
FEATURE [Part::Mirroring] Mirror017  label="Part (mirrored)"
  Base = (-100,0,0)
  Normal = (0,0,1)
  Placement = pos=(0,3350,30) rot=(0,0,-1;1.72483rad)
  Source = -> Part010
  expr: .Placement.Base.y = Spreadsheet003.l0
  expr: .Placement.Base.z = Spreadsheet003.t0 * 2 + Spreadsheet003.dia + 6
  expr: .Placement.Rotation.Angle = Spreadsheet003.sita * 2
FEATURE [Sketcher::SketchObject] Sketch026
  FullyConstrained = true
  expr: Constraints[10] = Spreadsheet004.l0
  expr: Constraints[9] = Spreadsheet004.w0
  sketch-geometry (5):
    g0: LineSegment StartX=0 StartY=0 StartZ=0 EndX=2600 EndY=0 EndZ=0
    g1: LineSegment StartX=2600 StartY=0 StartZ=0 EndX=2600 EndY=3350 EndZ=0
    g2: LineSegment StartX=2600 StartY=3350 StartZ=0 EndX=0 EndY=3350 EndZ=0
    g3: LineSegment StartX=0 StartY=3350 StartZ=0 EndX=0 EndY=0 EndZ=0
    g4: LineSegment StartX=0 StartY=0 StartZ=0 EndX=2600 EndY=3350 EndZ=0
  constraints (14):
    c: Coincident(g0,g1)
    c: Coincident(g1,g2)
    c: Coincident(g2,g3)
    c: Coincident(g3,g0)
    c: Horizontal(g0)
    c: Horizontal(g2)
    c: Vertical(g1)
    c: Vertical(g3)
    c: Coincident(g0,g-1)
    c: Distance(g2) = 2600
    c: Distance(g1) = 3350
    c: Coincident(g4,g0)
    c: Coincident(g4,g1)
    c: Angle(g0,g4) = 0.910787
FEATURE [Spreadsheet::Sheet] Spreadsheet004  label="Spreadsheet003"
  cells = A2='rodDia dia; B2(dia)=12; C2='thickness; D2(t0)=6; E2='w0; F2(w0)=2600; G2='sita; H2(sita)==atan(l0 / w0); A3='length L0; B3(L0)==(w0 ^ 2 + l0 ^ 2) ^ 0.5; C3='l1; D3(l1)==L0 - (dia * 5 + 500); E3='l0; F3(l0)=3350; B4='l; C4='l1; D4='a; E4='b; F4='c; G4='e; H4='f; I4='g; J4='h; K4='i; L4='r; A5='forkEndR; B5=80; D5=25; E5=10; F5=14; G5=16; H5=13; I5=40; J5=5; K5=13; L5=15; A6='turnBackle; B6=100; C6=20; D6=30; E6=16; F6=22; A7='forkEndL; B7=60; D7=25; E7=10; F7=13; G7=16; H7=13; I7=20; L7=15; A8=1; B8=2; C8=3; D8=4; E8=5; F8=6; G8=7; H8=8; I8=9; J8=10; K8=11; L8=12; A9='turnBackle; A10='d; B10='l; C10='l1; D10='a; E10='b; F10='c; G10='t0; A11=10; B11=75; C11=15; D11=24; E11=13; F11=17; G11=6; A12=12; B12=100; C12=20; D12=30; E12=16; F12=22; G12=6; A13=16; B13=125; C13=24; D13=36; E13=20; F13=27; G13=9; A14=20; B14=150; C14=28; D14=42; E14=23; F14=33; G14=9; A15=22; B15=175; C15=33; D15=48; E15=27; F15=37; G15=9; A16=24; B16=200; C16=38; D16=54; E16=30; F16=42; G16=12; A17=30; B17=250; C17=47; D17=66; E17=37; F17=52; G17=12; A18='forkEnd_L; A19='d; B19='l; C19='a; D19='b; E19='c; F19='e; G19='f; H19='g; I19='r; A20=10; B20=50; C20=20; D20=7; E20=10; F20=12; G20=10; H20=15; I20=12; A21=12; B21=60; C21=25; D21=10; E21=13; F21=16; G21=13; H21=20; I21=15; A22=16; B22=75; C22=30; D22=13; E22=16; F22=20; G22=16; H22=25; I22=19; A23=20; B23=90; C23=40; D23=16; E23=20; F23=24; G23=20; H23=30; I23=23; A24=22; B24=100; C24=45; D24=20; E24=23; F24=28; G24=23; H24=35; I24=27; A25=24; B25=115; C25=50; D25=23; E25=26; F25=32; G25=26; H25=40; I25=30; A26=30; B26=140; C26=65; D26=30; E26=33; F26=40; G26=33; H26=50; I26=38; A27='forkEnd_R; A28='d; B28='l; C28='a; D28='b; E28='c; F28='r; +82 more cells
FEATURE [Sketcher::SketchObject] Sketch027
  FullyConstrained = true
  Placement = pos=(0,0,0) rot=(1,0,0;1.5708rad)
  expr: Constraints[11] = Spreadsheet004.I5 + Spreadsheet004.dia * 2
  expr: Constraints[1] = Spreadsheet004.F5 / 2
  expr: Constraints[3] = Spreadsheet004.L5
  sketch-geometry (5):
    g0: Circle CenterX=0 CenterY=0 CenterZ=0 NormalX=0 NormalY=0 NormalZ=1 AngleXU=0 Radius=7
    g1: ArcOfCircle CenterX=0 CenterY=0 CenterZ=0 NormalX=0 NormalY=0 NormalZ=1 AngleXU=0 Radius=15 StartAngle=4.71239 EndAngle=7.85398
    g2: LineSegment StartX=-4.87e-14 StartY=15 StartZ=0 EndX=-64 EndY=15 EndZ=0
    g3: LineSegment StartX=-64 StartY=15 StartZ=0 EndX=-64 EndY=-15 EndZ=0
    g4: LineSegment StartX=-64 StartY=-15 StartZ=0 EndX=0 EndY=-15 EndZ=0
  constraints (12):
    c: Coincident(g0,g-1)
    c: Radius(g0) = 7
    c: Coincident(g1,g0)
    c: Radius(g1) = 15
    c: Horizontal(g2)
    c: Coincident(g2,g3)
    c: Vertical(g3)
    c: Coincident(g3,g4)
    c: Horizontal(g4)
    c: Tangent(g1,g2) = -1.5708
    c: Tangent(g1,g4) = -1.5708
    c: Distance(g2) = 64
FEATURE [Part::Cylinder] Cylinder004  label="円柱002"
  Angle = 360
  AttacherType = Attacher::AttachEngine3D
  FirstAngle = 0
  Height = 500
  Placement = pos=(-24,0,0) rot=(0,-1,0;1.5708rad)
  Radius = 6
  SecondAngle = 0
  expr: .Placement.Base.x = -Spreadsheet004.dia * 2
  expr: Radius = Spreadsheet004.dia / 2
FEATURE [Sketcher::SketchObject] Sketch028
  FullyConstrained = true
  Placement = pos=(0,0,0) rot=(1,0,0;1.5708rad)
  expr: Constraints[10] = Spreadsheet004.C6
  expr: Constraints[11] = Spreadsheet004.B6
  expr: Constraints[12] = Spreadsheet004.D6 / 2
  expr: Constraints[13] = Spreadsheet004.F6 / 2
  expr: Constraints[14] = Spreadsheet004.B6 / 2
  expr: Constraints[17] = Spreadsheet004.C6
  sketch-geometry (6):
    g0: LineSegment StartX=-50 StartY=0 StartZ=0 EndX=-50 EndY=11 EndZ=0
    g1: LineSegment StartX=-50 StartY=11 StartZ=0 EndX=-30 EndY=15 EndZ=0
    g2: LineSegment StartX=-30 StartY=15 StartZ=0 EndX=30 EndY=15 EndZ=0
    g3: LineSegment StartX=30 StartY=15 StartZ=0 EndX=50 EndY=11 EndZ=0
    g4: LineSegment StartX=50 StartY=11 StartZ=0 EndX=50 EndY=0 EndZ=0
    g5: LineSegment StartX=50 StartY=0 StartZ=0 EndX=-50 EndY=0 EndZ=0
  constraints (18):
    c: PointOnObject(g0,g-1)
    c: Vertical(g0)
    c: Coincident(g0,g1)
    c: Coincident(g1,g2)
    c: Horizontal(g2)
    c: Coincident(g2,g3)
    c: Coincident(g3,g4)
    c: PointOnObject(g4,g-1)
    c: Vertical(g4)
    c: Coincident(g4,g5)
    c: DistanceX(g2,g3) = 20
    c: DistanceX(g0,g3) = 100
    c: Distance(g1,g5) = 15
    c: Distance(g4) = 11
    c: DistanceX(g-1,g4) = 50
    c: Horizontal(g0,g3)
    c: Coincident(g5,g0)
    c: DistanceX(g0,g1) = 20
FEATURE [Part::Revolution] Revolve004
  Angle = 360
  Axis = (-1,0,0)
  AxisLink = -> Sketch028 [Edge6]
  Base = (-50,0,0)
  FaceMakerClass = Part::FaceMakerBullseye
  Solid = true
  Source = -> Sketch028
  Symmetric = false
FEATURE [Sketcher::SketchObject] Sketch029
  FullyConstrained = false
  Placement = pos=(0,0,0) rot=(0.57735,0.57735,0.57735;2.0944rad)
  expr: Constraints[16] = Spreadsheet004.F6
  expr: Constraints[17] = Spreadsheet004.F6 / 2
  sketch-geometry (8):
    g0: LineSegment StartX=-11 StartY=39.685 StartZ=0 EndX=-26 EndY=39.685 EndZ=0
    g1: LineSegment StartX=-26 StartY=39.685 StartZ=0 EndX=-26 EndY=-39.3666 EndZ=0
    g2: LineSegment StartX=-26 StartY=-39.3666 StartZ=0 EndX=-11 EndY=-39.3666 EndZ=0
    g3: LineSegment StartX=-11 StartY=-39.3666 StartZ=0 EndX=-11 EndY=39.685 EndZ=0
    g4: LineSegment StartX=11 StartY=39.685 StartZ=0 EndX=26 EndY=39.685 EndZ=0
    g5: LineSegment StartX=26 StartY=39.685 StartZ=0 EndX=26 EndY=-40.315 EndZ=0
    g6: LineSegment StartX=26 StartY=-40.315 StartZ=0 EndX=11 EndY=-40.315 EndZ=0
    g7: LineSegment StartX=11 StartY=-40.315 StartZ=0 EndX=11 EndY=39.685 EndZ=0
  constraints (22):
    c: Coincident(g0,g1)
    c: Coincident(g1,g2)
    c: Coincident(g2,g3)
    c: Coincident(g3,g0)
    c: Horizontal(g0)
    c: Horizontal(g2)
    c: Vertical(g1)
    c: Vertical(g3)
    c: Coincident(g4,g5)
    c: Coincident(g5,g6)
    c: Coincident(g6,g7)
    c: Coincident(g7,g4)
    c: Horizontal(g4)
    c: Horizontal(g6)
    c: Vertical(g5)
    c: Vertical(g7)
    c: DistanceX(g0,g4) = 22
    c: Distance(g-1,g7) = 11
    c: Distance(g5) = 80
    c: Distance(g4) = 15
    c: Distance(g0) = 15
    c: Horizontal(g0,g4)
FEATURE [Part::Extrusion] Extrude024  label="Extrude025"
  Base = -> Sketch029
  Dir = (1,0,0)
  DirMode = 2
  FaceMakerClass = Part::FaceMakerBullseye
  LengthFwd = 300
  LengthRev = 0
  Solid = true
  Symmetric = true
FEATURE [Part::Cut] Cut012
  Base = -> Revolve004
  Tool = -> Extrude024
FEATURE [Sketcher::SketchObject] Sketch030
  FullyConstrained = true
  Placement = pos=(0,0,0) rot=(1,0,0;1.5708rad)
  expr: Constraints[17] = Spreadsheet004.E6
  expr: Constraints[18] = Spreadsheet004.B6 - 2 * Spreadsheet004.C6
  expr: Constraints[19] = (Spreadsheet004.B6 - 2 * Spreadsheet004.C6) / 2
  expr: Constraints[20] = Spreadsheet004.E6 / 2
  sketch-geometry (9):
    g0: LineSegment StartX=30 StartY=3 StartZ=0 EndX=30 EndY=-3 EndZ=0
    g1: LineSegment StartX=25 StartY=-8 StartZ=0 EndX=-25 EndY=-8 EndZ=0
    g2: LineSegment StartX=-30 StartY=-3 StartZ=0 EndX=-30 EndY=3 EndZ=0
    g3: LineSegment StartX=-25 StartY=8 StartZ=0 EndX=25 EndY=8 EndZ=0
    g4: GeomPoint X=0 Y=0 Z=0
    g5: ArcOfCircle CenterX=-25 CenterY=3 CenterZ=0 NormalX=0 NormalY=0 NormalZ=1 AngleXU=0 Radius=5 StartAngle=1.5708 EndAngle=3.14159
    g6: ArcOfCircle CenterX=-25 CenterY=-3 CenterZ=0 NormalX=0 NormalY=0 NormalZ=1 AngleXU=0 Radius=5 StartAngle=3.14159 EndAngle=4.71239
    g7: ArcOfCircle CenterX=25 CenterY=-3 CenterZ=0 NormalX=0 NormalY=0 NormalZ=1 AngleXU=0 Radius=5 StartAngle=4.71239 EndAngle=6.28319
    g8: ArcOfCircle CenterX=25 CenterY=3 CenterZ=0 NormalX=0 NormalY=0 NormalZ=1 AngleXU=0 Radius=5 StartAngle=-4.09e-14 EndAngle=1.5708
  constraints (21):
    c: Horizontal(g1)
    c: Horizontal(g3)
    c: Vertical(g0)
    c: Vertical(g2)
    c: Coincident(g4,g-1)
    c: Tangent(g3,g5) = 1.5708
    c: Tangent(g2,g5) = 1.5708
    c: Tangent(g1,g6) = 1.5708
    c: Tangent(g2,g6) = 1.5708
    c: Tangent(g1,g7) = 1.5708
    c: Tangent(g0,g7) = 1.5708
    c: Tangent(g0,g8) = 1.5708
    c: Tangent(g3,g8) = 1.5708
    c: Radius(g8) = 5
    c: Equal(g8,g7)
    c: Equal(g7,g6)
    c: Equal(g6,g5)
    c: DistanceY(g1,g3) = 16
    c: DistanceX(g2,g0) = 60
    c: Distance(g4,g2) = 30
    c: Distance(g4,g1) = 8
FEATURE [Part::Extrusion] Extrude025  label="Extrude026"
  Base = -> Sketch030
  Dir = (0,-1,2e-16)
  DirMode = 2
  FaceMakerClass = Part::FaceMakerBullseye
  LengthFwd = 60
  LengthRev = 0
  Solid = true
  Symmetric = true
FEATURE [Part::Cut] Cut013
  Base = -> Cut012
  Tool = -> Extrude025
FEATURE [Sketcher::SketchObject] Sketch031
  FullyConstrained = true
  Placement = pos=(0,0,0) rot=(0.57735,0.57735,0.57735;2.0944rad)
  expr: Constraints[1] = Spreadsheet004.dia / 2
  sketch-geometry (1):
    g0: Circle CenterX=0 CenterY=0 CenterZ=0 NormalX=0 NormalY=0 NormalZ=1 AngleXU=0 Radius=6
  constraints (2):
    c: Coincident(g0,g-1)
    c: Radius(g0) = 6
FEATURE [Part::Extrusion] Extrude026  label="Extrude027"
  Base = -> Sketch031
  Dir = (1,0,0)
  DirMode = 2
  FaceMakerClass = Part::FaceMakerBullseye
  LengthFwd = 300
  LengthRev = 0
  Solid = true
  Symmetric = true
FEATURE [Part::Cut] Cut014  label="turnBackle002"
  Base = -> Cut013
  Placement = pos=(-530,0,0) rot=(0,0,1;0rad)
  Tool = -> Extrude026
  expr: .Placement.Base.x = -(Spreadsheet004.dia * 2.5 + 500)
FEATURE [Part::Cylinder] Cylinder005  label="rod002"
  Angle = 360
  AttacherType = Attacher::AttachEngine3D
  FirstAngle = 0
  Height = 3680.58
  Placement = pos=(-536,0,-1.37e-13) rot=(0,-1,0;1.5708rad)
  Radius = 6
  SecondAngle = 0
  expr: .Placement.Base.x = -(Spreadsheet004.dia * 3 + 500)
  expr: Height = Spreadsheet004.l1
  expr: Radius = Spreadsheet004.dia / 2
FEATURE [Part::Extrusion] Extrude027  label="Extrude028"
  Base = -> Sketch027
  Dir = (0,-1,2e-16)
  DirMode = 2
  FaceMakerClass = Part::FaceMakerBullseye
  LengthFwd = 6
  LengthRev = 0
  Placement = pos=(0,9,0) rot=(0,0,1;0rad)
  Solid = true
  Symmetric = true
  expr: .Placement.Base.y = Spreadsheet004.dia / 2 + Spreadsheet004.t0 / 2
  expr: LengthFwd = Spreadsheet004.t0
FEATURE [Part::FeaturePython] Clone002  label="Extrude029"  # Draft clone (typed FeaturePython)
  AttacherType = Attacher::AttachEngine3D
  Fuse = false
  Objects = -> [Extrude027]
  Placement = pos=(-4240.58,9,0) rot=(0,1,0;3.14159rad)
  Scale = (1,1,1)
  expr: .Placement.Base.x = -Spreadsheet004.L0
  expr: .Placement.Base.y = Spreadsheet004.t0 / 2 + Spreadsheet004.dia / 2
FEATURE [Part::Compound] Compound009
  Links = -> [Cylinder004,Extrude027,Cut014,Cylinder005,Clone002]
  Placement = pos=(0,0,0) rot=(1,0,0;1.5708rad)
FEATURE [App::Part] Part012  label="Part008"
  Group = -> [Extrude024,Extrude025,Clone002,Cylinder004,Revolve004,Sketch027,Sketch028,Sketch029,Cut013,Cut014,Cut012,Sketch030,Sketch031,Extrude026,Extrude027,Cylinder005,Compound009]
  Origin = -> Origin015
  Placement = pos=(0,0,0) rot=(0,0,1;4.05238rad)
  expr: .Placement.Rotation.Angle = 180 ° + Spreadsheet004.sita
FEATURE [Part::Mirroring] Mirror018  label="Part (mirrored)001"
  Base = (-100,0,0)
  Normal = (0,0,1)
  Placement = pos=(0,3350,30) rot=(0,0,-1;1.82157rad)
  Source = -> Part012
  expr: .Placement.Base.y = Spreadsheet004.l0
  expr: .Placement.Base.z = Spreadsheet004.t0 * 2 + Spreadsheet004.dia + 6
  expr: .Placement.Rotation.Angle = Spreadsheet004.sita * 2
FEATURE [Part::Compound] Compound010
  Links = -> [Mirror017,Part010]
FEATURE [App::Part] Part009  label="TurnBackleC"
  Group = -> [Spreadsheet003,Sketch020,Part010,Mirror017,Compound010]
  Origin = -> Origin012
  Placement = pos=(1768.77,-1672.49,1181.14) rot=(0,0,1;0rad)
FEATURE [Part::Compound] Compound011
  Links = -> [Mirror018,Part012]
FEATURE [App::Part] Part011  label="TurnBackleC001"
  Group = -> [Spreadsheet004,Sketch026,Part012,Mirror018,Compound011]
  Origin = -> Origin014
  Placement = pos=(4756.67,-1672.28,1180.95) rot=(0,0,1;0rad)
FEATURE [Part::Mirroring] Mirror019  label="TurnBackleC (mirrored)"
  Base = (0,0,0)
  Normal = (1,0,0)
  Source = -> Part009
FEATURE [Part::Mirroring] Mirror020  label="TurnBackleC001 (mirrored)"
  Base = (0,0,0)
  Normal = (1,0,0)
  Source = -> Part011
FEATURE [Part::FeaturePython] Flange  # WARN: FeaturePython — macro-defined, semantics opaque (R4)
  Placement = pos=(7820.41,7.94e-13,1860) rot=(0.57735,0.57735,0.57735;2.0944rad)
  dia = 6
  fittings = 00_Flange
  material = 0
  standard = 1
FEATURE [Part::FeaturePython] Ring  # WARN: FeaturePython — macro-defined, semantics opaque (R4)
  D = 360
  Placement = pos=(0,0,0) rot=(0,1,0;1.5708rad)
  d = 315
  sface = 0
FEATURE [Part::Extrusion] Extrude028  label="Extrude030"
  Base = -> Ring
  Dir = (1,0,2e-16)
  DirMode = 2
  FaceMakerClass = Part::FaceMakerBullseye
  LengthFwd = 400
  LengthRev = 0
  Placement = pos=(7830.41,7.94e-13,1860) rot=(0,0,1;0rad)
  Reversed = true
  Solid = true
  Symmetric = false
FEATURE [App::Part] Part013  label="brg01"
  Origin = -> Origin016
  Placement = pos=(6100,-1.1983e-12,0) rot=(0,0,1;0rad)
  expr: .Placement.Base.x = Spreadsheet005.L0 - Spreadsheet005.l1
FEATURE [Part::FeaturePython] Straight_tube  # WARN: FeaturePython — macro-defined, semantics opaque (R4)
  L = 6280
  Placement = pos=(-180,0,0) rot=(0,0,1;0rad)
  dia = 16
  fittings = 05_Straight pipe
  material = 1
  standard = 1
  expr: .Placement.Base.x = -Spreadsheet005.l1
  expr: L = Spreadsheet005.L0
FEATURE [Sketcher::SketchObject] Sketch032
  FullyConstrained = true
  Placement = pos=(0,0,0) rot=(1,0,0;1.5708rad)
  sketch-geometry (12):
    g0: LineSegment StartX=5580 StartY=159.25 StartZ=0 EndX=5600 EndY=159.25 EndZ=0
    g1: LineSegment StartX=5600 StartY=159.25 StartZ=0 EndX=5600 EndY=164.25 EndZ=0
    g2: LineSegment StartX=5600 StartY=164.25 StartZ=0 EndX=5580 EndY=164.25 EndZ=0
    g3: LineSegment StartX=5580 StartY=164.25 StartZ=0 EndX=5580 EndY=159.25 EndZ=0
    g4: LineSegment StartX=0 StartY=159.25 StartZ=0 EndX=0 EndY=169.25 EndZ=0
    g5: LineSegment StartX=0 StartY=169.25 StartZ=0 EndX=19 EndY=169.25 EndZ=0
    g6: LineSegment StartX=19 StartY=169.25 StartZ=0 EndX=19 EndY=164.25 EndZ=0
    g7: LineSegment StartX=19 StartY=164.25 StartZ=0 EndX=31 EndY=164.25 EndZ=0
    g8: LineSegment StartX=31 StartY=164.25 StartZ=0 EndX=31 EndY=169.25 EndZ=0
    g9: LineSegment StartX=31 StartY=169.25 StartZ=0 EndX=50 EndY=169.25 EndZ=0
    g10: LineSegment StartX=50 StartY=169.25 StartZ=0 EndX=50 EndY=159.25 EndZ=0
    g11: LineSegment StartX=50 StartY=159.25 StartZ=0 EndX=0 EndY=159.25 EndZ=0
  constraints (36):
    c: Coincident(g0,g1)
    c: Coincident(g1,g2)
    c: Coincident(g2,g3)
    c: Coincident(g3,g0)
    c: Horizontal(g0)
    c: Horizontal(g2)
    c: Vertical(g1)
    c: Vertical(g3)
    c: DistanceY(g-1,g0) = 159.25
    c: DistanceY(g1,g1) = 5
    c: DistanceX(g2,g2) = 20
    c: Vertical(g4)
    c: Coincident(g4,g5)
    c: Horizontal(g5)
    c: Coincident(g5,g6)
    c: Vertical(g6)
    c: Coincident(g6,g7)
    c: Coincident(g7,g8)
    c: Coincident(g8,g9)
    c: Coincident(g9,g10)
    c: Coincident(g10,g11)
    c: Coincident(g11,g4)
    c: Horizontal(g11)
    c: Vertical(g10)
    c: Horizontal(g7)
    c: Horizontal(g9)
    c: Vertical(g8)
    c: DistanceY(g10,g10) = 10
    c: DistanceY(g7,g8) = 5
    c: Horizontal(g8,g5)
    c: DistanceX(g11,g11) = 50
    c: DistanceX(g7,g7) = 12
    c: DistanceX(g5,g5) = 19
    c: DistanceY(g-1,g4) = 159.25
    c: Vertical(g-1,g4)
    c: DistanceX(g-1,g0) = 5600
FEATURE [Part::Revolution] Revolve005
  Angle = 360
  Axis = (1,0,0)
  Base = (0,0,0)
  FaceMakerClass = Part::FaceMakerBullseye
  Placement = pos=(88,0,0) rot=(0,0,1;0rad)
  Solid = true
  Source = -> Sketch032
  Symmetric = false
FEATURE [Spreadsheet::Sheet] Spreadsheet005  label="Spreadsheet_pipeSkimmer"
  cells = A2='tankDia  D0; B2(D0)=15500; A3='fullLength L0; B3(L0)=6280; A4='length       l1; B4(l1)=180; A5='n0; B5(n0)=5; A6='l3; B6(l3)=1134; A7='開閉台  h2; B7(h2)=1500
FEATURE [App::Part] Part015  label="pipeSkimmer"
  Group = -> [Part013,Spreadsheet005]
  Origin = -> Origin018
  Placement = pos=(2172.35,0,0) rot=(0,0,1;0rad)
FEATURE [Sketcher::SketchObject] Sketch033
  FullyConstrained = false
  Placement = pos=(0,0,0) rot=(0.57735,0.57735,0.57735;2.0944rad)
  sketch-geometry (3):
    g0: LineSegment StartX=0 StartY=0 StartZ=0 EndX=114.659 EndY=220.257 EndZ=0
    g1: LineSegment StartX=0 StartY=0 StartZ=0 EndX=-114.659 EndY=220.257 EndZ=0
    g2: ArcOfCircle CenterX=0 CenterY=0 CenterZ=0 NormalX=0 NormalY=0 NormalZ=1 AngleXU=0 Radius=248.314 StartAngle=1.09083 EndAngle=2.05076
  constraints (7):
    c: Coincident(g-1,g0)
    c: Coincident(g1,g0)
    c: Coincident(g2,g0)
    c: Coincident(g2,g1)
    c: Coincident(g2,g0)
    c: Angle(g0,g-2) = 0.479966
    c: Angle(g0,g1) = 0.959931
FEATURE [Part::Extrusion] Extrude029  label="Extrude031"
  Base = -> Sketch033
  Dir = (1,0,0)
  DirMode = 2
  FaceMakerClass = Part::FaceMakerBullseye
  LengthFwd = 1000
  LengthRev = 0
  Placement = pos=(100,0,0) rot=(0,0,1;0rad)
  Solid = true
  Symmetric = false
FEATURE [Part::FeaturePython] Array003  # Draft array (typed FeaturePython)
  AlwaysSyncPlacement = false
  Angle = 360
  ArrayType = 0
  Axis = (0,0,1)
  Base = -> Extrude029
  Center = (0,0,0)
  Count = 5
  ExpandArray = false
  Fuse = false
  IntervalAxis = (0,0,0)
  IntervalX = (1100,0,0)
  IntervalY = (0,100,0)
  IntervalZ = (0,0,100)
  NumberCircles = 3
  NumberPolar = 5
  NumberX = 5
  NumberY = 1
  NumberZ = 1
  PlacementList = 5 placements: arithmetic series from (100,0,0) step (1100,0,0) to (4500,0,0)
  RadialDistance = 50
  ScaleList = (5) [(1,1,1),(1,1,1),(1,1,1),(1,1,1),(1,1,1)]
  Symmetry = 1
  TangentialDistance = 25
FEATURE [Part::Cut] Cut015
  Base = -> Straight_tube
  Tool = -> Array003
FEATURE [Sketcher::SketchObject] Sketch034
  FullyConstrained = false
  Placement = pos=(0,0,0) rot=(0.57735,0.57735,0.57735;2.0944rad)
  sketch-geometry (3):
    g0: LineSegment StartX=0 StartY=0 StartZ=0 EndX=-124.513 EndY=239.188 EndZ=0
    g1: LineSegment StartX=0 StartY=0 StartZ=0 EndX=124.513 EndY=239.188 EndZ=0
    g2: ArcOfCircle CenterX=0 CenterY=0 CenterZ=0 NormalX=0 NormalY=0 NormalZ=1 AngleXU=0 Radius=269.656 StartAngle=1.09083 EndAngle=2.05076
  constraints (7):
    c: Coincident(g0,g-1)
    c: Coincident(g1,g0)
    c: Coincident(g2,g1)
    c: Coincident(g2,g0)
    c: Coincident(g2,g0)
    c: Angle(g1,g0) = 0.959931
    c: Angle(g1,g-2) = 0.479966
FEATURE [Part::Extrusion] Extrude030  label="Extrude032"
  Base = -> Sketch034
  Dir = (1,0,0)
  DirMode = 2
  FaceMakerClass = Part::FaceMakerBullseye
  LengthFwd = 130
  LengthRev = 0
  Placement = pos=(-25,0,0) rot=(0,0,1;0rad)
  Reversed = true
  Solid = true
  Symmetric = false
  expr: LengthFwd = Spreadsheet005.l1 - 50
FEATURE [Part::Cut] Cut016
  Base = -> Cut015
  Tool = -> Extrude030
FEATURE [Sketcher::SketchObject] Sketch035
  FullyConstrained = true
  Placement = pos=(0,0,0) rot=(0.57735,0.57735,0.57735;2.0944rad)
  sketch-geometry (6):
    g0: LineSegment StartX=0 StartY=0 StartZ=0 EndX=247.487 EndY=247.487 EndZ=0
    g1: Circle CenterX=247.487 CenterY=247.487 CenterZ=0 NormalX=0 NormalY=0 NormalZ=1 AngleXU=0 Radius=7.5
    g2: ArcOfCircle CenterX=247.487 CenterY=247.487 CenterZ=0 NormalX=0 NormalY=0 NormalZ=1 AngleXU=0 Radius=20 StartAngle=5.62869 EndAngle=8.50848
    g3: LineSegment StartX=235.312 StartY=263.354 StartZ=0 EndX=74.8903 EndY=140.258 EndZ=0
    g4: LineSegment StartX=263.354 StartY=235.312 StartZ=0 EndX=140.258 EndY=74.8903 EndZ=0
    g5: ArcOfCircle CenterX=0 CenterY=0 CenterZ=0 NormalX=0 NormalY=0 NormalZ=1 AngleXU=0 Radius=159 StartAngle=0.490434 EndAngle=1.08036
  constraints (15):
    c: Coincident(g0,g-1)
    c: Angle(g-1,g0) = 0.785398
    c: Coincident(g1,g0)
    c: Radius(g1) = 7.5
    c: Coincident(g2,g1)
    c: Coincident(g5,g3)
    c: Coincident(g5,g4)
    c: Coincident(g5,g0)
    c: Tangent(g2,g3) = -1.5708
    c: Tangent(g2,g4) = 1.5708
    c: Equal(g4,g3)
    c: Radius(g5) = 159
    c: Angle(g3,g4) = 0.261799
    c: Distance(g5,g1) = 350
    c: Radius(g2) = 20
FEATURE [Part::Extrusion] Extrude031  label="Extrude033"
  Base = -> Sketch035
  Dir = (1,0,0)
  DirMode = 2
  FaceMakerClass = Part::FaceMakerBullseye
  LengthFwd = 6
  LengthRev = 0
  Placement = pos=(-150,0,0) rot=(0,0,1;0rad)
  Solid = true
  Symmetric = true
FEATURE [App::Part] Part016  label="arm"
  Group = -> [Sketch035,Extrude031]
  Origin = -> Origin019
  Placement = pos=(5780,0,0) rot=(1,0,0;1.8326rad)
  expr: .Placement.Base.x = Spreadsheet005.L0 - 500
FEATURE [Sketcher::SketchObject] Sketch036
  ExternalGeometry = -> [Cut016]
  FullyConstrained = false
  MapMode = 5
  Placement = pos=(-180,0,0) rot=(0.57735,-0.57735,-0.57735;2.0944rad)
  Support = -> [Cut016]
  sketch-geometry (1):
    g0: Circle CenterX=0 CenterY=0 CenterZ=0 NormalX=0 NormalY=0 NormalZ=1 AngleXU=0 Radius=159.25
  constraints (1):
    c: Coincident(g0,g-1)
FEATURE [Part::Extrusion] Extrude032  label="Extrude034"
  Base = -> Sketch036
  Dir = (-1,0,0)
  DirMode = 2
  FaceMakerClass = Part::FaceMakerBullseye
  LengthFwd = 6
  LengthRev = 0
  Solid = true
  Symmetric = false
FEATURE [Part::Feature] Part__Feature010  label="電動トップハンドル_LTKD-01 v5"
  Placement = pos=(0,-389.711,-5.7e-14) rot=(1,0,0;1.5708rad)
  shape: bbox 555.2 x 557.2 x 1150 mm, 73 faces (baked)
FEATURE [App::Part] Part017  label="開閉台"
  Group = -> [Part__Feature010]
  Origin = -> Origin020
  Placement = pos=(0,-400,1500) rot=(0,0,1;3.14159rad)
FEATURE [Sketcher::SketchObject] Sketch037
  FullyConstrained = false
  Placement = pos=(0,0,0) rot=(0.57735,0.57735,0.57735;2.0944rad)
  sketch-geometry (5):
    g0: Circle CenterX=0 CenterY=0 CenterZ=0 NormalX=0 NormalY=0 NormalZ=1 AngleXU=0 Radius=7.5
    g1: ArcOfCircle CenterX=0 CenterY=0 CenterZ=0 NormalX=0 NormalY=0 NormalZ=1 AngleXU=0 Radius=20 StartAngle=3.14159 EndAngle=6.28319
    g2: LineSegment StartX=-20 StartY=9.32106e-06 StartZ=0 EndX=-20 EndY=80 EndZ=0
    g3: LineSegment StartX=-20 StartY=80 StartZ=0 EndX=20 EndY=80 EndZ=0
    g4: LineSegment StartX=20 StartY=80 StartZ=0 EndX=20 EndY=3.56439e-05 EndZ=0
  constraints (13):
    c: Coincident(g0,g-1)
    c: Coincident(g1,g0)
    c: Radius(g1) = 20
    c: Radius(g0) = 7.5
    c: Vertical(g2)
    c: Coincident(g2,g3)
    c: Horizontal(g3)
    c: Coincident(g3,g4)
    c: Vertical(g4)
    c: Coincident(g1,g4)
    c: Coincident(g1,g2)
    c: DistanceY(g-1,g3) = 80
    c: DistanceX(g3,g3) = 40
FEATURE [Part::Extrusion] Extrude033  label="Extrude035"
  Base = -> Sketch037
  Dir = (1,0,0)
  DirMode = 2
  FaceMakerClass = Part::FaceMakerBullseye
  LengthFwd = 40
  LengthRev = 0
  Solid = true
  Symmetric = true
FEATURE [Sketcher::SketchObject] Sketch038
  ExternalGeometry = -> [Extrude033]
  FullyConstrained = false
  MapMode = 5
  Placement = pos=(0,-20,0) rot=(1,0,0;1.5708rad)
  Support = -> [Extrude033]
  sketch-geometry (4):
    g0: LineSegment StartX=-5 StartY=-25.0355 StartZ=0 EndX=5 EndY=-25.0355 EndZ=0
    g1: LineSegment StartX=5 StartY=-25.0355 StartZ=0 EndX=5 EndY=60 EndZ=0
    g2: LineSegment StartX=5 StartY=60 StartZ=0 EndX=-5 EndY=60 EndZ=0
    g3: LineSegment StartX=-5 StartY=60 StartZ=0 EndX=-5 EndY=-25.0355 EndZ=0
  constraints (11):
    c: Coincident(g0,g1)
    c: Coincident(g1,g2)
    c: Coincident(g2,g3)
    c: Coincident(g3,g0)
    c: Horizontal(g0)
    c: Horizontal(g2)
    c: Vertical(g1)
    c: Vertical(g3)
    c: Distance(g1,g-3) = 20
    c: DistanceX(g0,g0) = 10
    c: DistanceX(g0,g-1) = 5
FEATURE [Part::Extrusion] Extrude034  label="Extrude036"
  Base = -> Sketch038
  Dir = (0,-1,2e-16)
  DirMode = 2
  FaceMakerClass = Part::FaceMakerBullseye
  LengthFwd = 50
  LengthRev = 0
  Reversed = true
  Solid = true
  Symmetric = false
FEATURE [Part::Cut] Cut017
  Base = -> Extrude033
  Tool = -> Extrude034
FEATURE [Sketcher::SketchObject] Sketch039
  FullyConstrained = true
  MapMode = 5
  Placement = pos=(0,0,80) rot=(0,0,1;0rad)
  Support = -> [Cut017]
  sketch-geometry (1):
    g0: Circle CenterX=0 CenterY=0 CenterZ=0 NormalX=0 NormalY=0 NormalZ=1 AngleXU=0 Radius=15
  constraints (2):
    c: Coincident(g0,g-1)
    c: Radius(g0) = 15
FEATURE [Part::Extrusion] Extrude035  label="Extrude037"
  Base = -> Sketch039
  Dir = (0,0,1)
  DirMode = 2
  FaceMakerClass = Part::FaceMakerBullseye
  LengthFwd = 400
  LengthRev = 0
  Solid = true
  Symmetric = false
FEATURE [Part::FeaturePython] Clone003  label="Cut018"  # Draft clone (typed FeaturePython)
  AttacherType = Attacher::AttachEngine3D
  Fuse = false
  Objects = -> [Cut017]
  Placement = pos=(-1.83e-13,0,560) rot=(0,1,0;3.14159rad)
  Scale = (1,1,1)
FEATURE [App::Part] Part018  label="rod"
  Group = -> [Cut017,Clone003,Sketch038,Sketch037,Sketch039,Extrude033,Extrude034,Extrude035]
  Origin = -> Origin021
  Placement = pos=(7140.01,-302.95,2038.03) rot=(0,0,1;0rad)
FEATURE [Sketcher::SketchObject] Sketch040
  FullyConstrained = false
  Placement = pos=(0,0,0) rot=(0.57735,0.57735,0.57735;2.0944rad)
  sketch-geometry (5):
    g0: Circle CenterX=0 CenterY=0 CenterZ=0 NormalX=0 NormalY=0 NormalZ=1 AngleXU=0 Radius=7.5
    g1: ArcOfCircle CenterX=0 CenterY=0 CenterZ=0 NormalX=0 NormalY=0 NormalZ=1 AngleXU=0 Radius=20 StartAngle=3.14864 EndAngle=6.2925
    g2: LineSegment StartX=-19.9995 StartY=-0.141043 StartZ=0 EndX=-19.9995 EndY=80 EndZ=0
    g3: LineSegment StartX=-19.9995 StartY=80 StartZ=0 EndX=19.9991 EndY=80 EndZ=0
    g4: LineSegment StartX=19.9991 StartY=80 StartZ=0 EndX=19.9991 EndY=0.186233 EndZ=0
  constraints (12):
    c: Coincident(g0,g-1)
    c: Coincident(g1,g0)
    c: Vertical(g2)
    c: Coincident(g2,g3)
    c: Horizontal(g3)
    c: Coincident(g3,g4)
    c: Vertical(g4)
    c: Coincident(g1,g4)
    c: Coincident(g1,g2)
    c: Radius(g0) = 7.5
    c: Radius(g1) = 20
    c: DistanceY(g-1,g3) = 80
FEATURE [Part::Extrusion] Extrude036  label="Extrude038"
  Base = -> Sketch040
  Dir = (1,0,0)
  DirMode = 2
  FaceMakerClass = Part::FaceMakerBullseye
  LengthFwd = 9
  LengthRev = 0
  Solid = true
  Symmetric = true
FEATURE [Part::Cylinder] Cylinder  label="円柱"
  Angle = 360
  AttacherType = Attacher::AttachEngine3D
  FirstAngle = 0
  Height = 1000
  Placement = pos=(0,0,30) rot=(0,0,1;0rad)
  Radius = 15
  SecondAngle = 0
FEATURE [App::Part] Part019  label="rod003"
  Group = -> [Sketch040,Cylinder,Extrude036]
  Origin = -> Origin022
FEATURE [Part::Compound] Compound013  label="rod004"
  Links = -> [Part019]
  Placement = pos=(7140,-303.29,2598.57) rot=(0.999848,0.015695,0.007617;2e-06rad)
FEATURE [Part::Compound] Compound028  label="開閉台001"
  Links = -> [Part017]
  Placement = pos=(7139.5,-295.998,1288.27) rot=(0.999877,0.015695,0;2e-06rad)
FEATURE [Part::FeaturePython] Brg_001  # a2plus imported part (geometry in sourceFile) (typed FeaturePython)
  Placement = pos=(0,5.69e-13,0) rot=(0,0,1;0rad)
  a2p_Version = 0.4.60n
  fixedPosition = true
  localSourceObject = Compound
  objectType = a2pPart
  sourceFile = converted
  subassemblyImport = false
  timeLastImport = 1.70945e+09
  updateColors = true
FEATURE [App::FeaturePython] circularEdge_001_mirror001  label="circularEdge_001__pipe001"  # a2plus constraint (typed FeaturePython)
  Object1 = Compound012
  Object2 = Brg_001
  ParentTreeObject = -> Brg_001
  SubElement1 = Edge107
  SubElement2 = Edge17
  Suppressed = false
  Type = circularEdge
  directionConstraint = 0
  lockRotation = false
  offset = 0
FEATURE [App::FeaturePython] axisCoincident_001_mirror001  label="axisCoincident_001__Compound014"  # a2plus constraint (typed FeaturePython)
  Object1 = Compound014
  Object2 = Compound012
  SubElement1 = Edge29
  SubElement2 = Edge150
  Suppressed = false
  Type = axial
  directionConstraint = 0
  lockRotation = false
FEATURE [App::FeaturePython] circularEdge_005  label="circularEdge_004__Compound014"  # a2plus constraint (typed FeaturePython)
  Object1 = Compound013
  Object2 = Compound014
  ParentTreeObject = -> Compound013
  SubElement1 = Edge18
  SubElement2 = Edge56
  Suppressed = false
  Type = circularEdge
  directionConstraint = 0
  lockRotation = false
  offset = 0
FEATURE [App::FeaturePython] circularEdge_004_mirror  label="circularEdge_004__rod004"  # a2plus constraint (typed FeaturePython)
  Object1 = Compound013
  Object2 = Compound014
  SubElement1 = Edge18
  SubElement2 = Edge56
  Suppressed = false
  Type = circularEdge
  directionConstraint = 0
  lockRotation = false
  offset = 0
FEATURE [App::FeaturePython] axisCoincident_002_mirror001  label="axisCoincident_002__開閉台001"  # a2plus constraint (typed FeaturePython)
  Object1 = Compound003
  Object2 = Compound013
  ParentTreeObject = -> Compound013
  SubElement1 = Face69
  SubElement2 = Face1
  Suppressed = false
  Type = axial
  directionConstraint = 0
  lockRotation = false
FEATURE [Part::Compound] Compound029  label="brg"
  Links = -> [Extrude028,Flange]
  Placement = pos=(-1741.5,0,-1859.57) rot=(0,0,1;0rad)
FEATURE [App::Part] Part014  label="pipe"
  Group = -> [Sketch032,Revolve005,Cut015,Cut016,Sketch034,Sketch033,Straight_tube,Array003,Extrude030,Extrude029,Sketch036,Extrude032,Part016,Extrude028,Flange,Ring,Compound029]
  Origin = -> Origin017
  Placement = pos=(1510.09,0,1862.5) rot=(0,0,1;0rad)
FEATURE [App::Part] Part008  label="feedWell"
  Group = -> [Part006,Part005,Part004,Compound024,Spreadsheet001,Spreadsheet002,Mirror013,Mirror004,Mirror015,AngleSteel006,Compound025,Extrude019,Sketch019,Mirror014,ChannelSteel004,Array002,Mirror016,Part009,Part011,Mirror019,Mirror020,Part015,Brg_001,Part014,Part018,axisCoincident_001_mirror001,Part019,Compound013,circularEdge_005,circularEdge_004_mirror,Compound028,Part017,axisCoincident_002_mirror001]
  Origin = -> Origin004
  Placement = pos=(0,0,2972) rot=(0,0,1;0rad)
FEATURE [Part::FeaturePython] Single_Flange_Length_Tube  # WARN: FeaturePython — macro-defined, semantics opaque (R4)
  Fittings = 01_Single Flange Length Tube
  L0 = 550
  Placement = pos=(7610.16,0.06,4833.69) rot=(0,0,1;0rad)
  dia = 5
  mass = 62.1325
FEATURE [App::Part] body_15_5m  label="1_body_15.5m"
  Group = -> [Part__Feature,Part__Feature001,Part__Feature004,Part__Feature005,Single_Flange_Length_Tube]
  Origin = -> Origin001
FEATURE [Sketcher::SketchObject] Sketch041
  FullyConstrained = true
  sketch-geometry (5):
    g0: LineSegment StartX=-680 StartY=-750 StartZ=0 EndX=-680 EndY=750 EndZ=0
    g1: LineSegment StartX=-680 StartY=750 StartZ=0 EndX=680 EndY=750 EndZ=0
    g2: LineSegment StartX=680 StartY=750 StartZ=0 EndX=680 EndY=-750 EndZ=0
    g3: LineSegment StartX=680 StartY=-750 StartZ=0 EndX=-680 EndY=-750 EndZ=0
    g4: GeomPoint X=0 Y=0 Z=0
  constraints (12):
    c: Coincident(g0,g1)
    c: Coincident(g1,g2)
    c: Coincident(g2,g3)
    c: Coincident(g3,g0)
    c: Horizontal(g1)
    c: Horizontal(g3)
    c: Vertical(g0)
    c: Vertical(g2)
    c: Symmetric(g1,g0,g4)
    c: Coincident(g4,g-1)
    c: DistanceY(g2,g2) = 1500
    c: DistanceX(g1,g1) = 1360
FEATURE [Part::FeaturePython] HShapeSteel  # WARN: FeaturePython — macro-defined, semantics opaque (R4)
  B = 150
  H = 150
  L = 1000
  Placement = pos=(530,0,-150) rot=(0,0,1;0rad)
  Solid = false
  g0 = 7.85
  mass = 0
  size = 2
  standard = SS_Wide
  t1 = 7
  t2 = 10
FEATURE [Part::Sweep] Sweep
  Frenet = true
  Sections = -> [HShapeSteel]
  Solid = true
  Spine = -> Sketch041 [Edge3,Edge2,Edge1,Edge4]
  Transition = 1
FEATURE [Part::FeaturePython] HShapeSteel001  # WARN: FeaturePython — macro-defined, semantics opaque (R4)
  B = 150
  H = 150
  L = 1000
  Placement = pos=(607.98,425,-75) rot=(0.57735,0.57735,0.57735;2.0944rad)
  Solid = true
  g0 = 7.85
  mass = 31.5089
  size = 2
  standard = SS_Wide
  t1 = 7
  t2 = 10
FEATURE [Part::FeaturePython] Clone004  label="HShapeSteel002"  # Draft clone (typed FeaturePython)
  AttacherType = Attacher::AttachEngine3D
  Fuse = false
  Objects = -> [HShapeSteel001]
  Placement = pos=(607.98,-425,-75) rot=(0.57735,0.57735,0.57735;2.0944rad)
  Scale = (1,1,1)
FEATURE [Part::FeaturePython] HShapeSteel002  label="HShapeSteel003"  # WARN: FeaturePython — macro-defined, semantics opaque (R4)
  B = 150
  H = 150
  L = 1000
  Placement = pos=(1607.98,-500,-150) rot=(0,0,1;1.5708rad)
  Solid = false
  g0 = 7.85
  mass = 0
  size = 2
  standard = SS_Wide
  t1 = 7
  t2 = 10
FEATURE [Part::FeaturePython] HShapeSteel003  label="HShapeSteel004"  # WARN: FeaturePython — macro-defined, semantics opaque (R4)
  B = 150
  H = 194
  L = 1000
  Placement = pos=(1900,-500,-194) rot=(0,0,1;1.5708rad)
  Solid = false
  g0 = 7.85
  mass = 0
  size = 1
  standard = SS_Medium
  t1 = 6
  t2 = 9
FEATURE [Part::Loft] Loft
  Closed = false
  MaxDegree = 5
  Ruled = false
  Sections = -> [HShapeSteel002,HShapeSteel003]
  Solid = true
FEATURE [Part::Extrusion] Extrude037  label="Extrude039"
  Base = -> HShapeSteel003
  Dir = (-1,-2e-16,0)
  DirMode = 2
  FaceMakerClass = Part::FaceMakerBullseye
  LengthFwd = 6250
  LengthRev = 0
  Reversed = true
  Solid = true
  Symmetric = false
  expr: LengthFwd = Spreadsheet006.L0
FEATURE [Part::MultiFuse] Fusion002
  Shapes = -> [HShapeSteel001,Clone004]
FEATURE [Part::MultiFuse] Fusion003
  Shapes = -> [Extrude037,Loft]
FEATURE [Part::FeaturePython] Clone005  label="Fusion004"  # Draft clone (typed FeaturePython)
  AttacherType = Attacher::AttachEngine3D
  Fuse = false
  Objects = -> [Fusion003]
  Placement = pos=(-9.09e-13,850,6.6e-14) rot=(0,0,1;0rad)
  Scale = (1,1,1)
FEATURE [Part::Mirroring] Mirror021  label="Fusion (mirrored)001"
  Base = (0,0,0)
  Normal = (1,0,0)
  Source = -> Fusion002
FEATURE [Part::MultiFuse] Fusion004  label="Fusion005"
  Refine = true
  Shapes = -> [Sweep,Fusion002,Mirror021]
FEATURE [Spreadsheet::Sheet] Spreadsheet006
  cells = A2='tankdia   dia; B2(dia)=15500; A3='L0; B3(L0)==dia / 2 + 400 - 1900; A4='n; B4(n)==L0 / 700
FEATURE [Sketcher::SketchObject] Sketch042
  ExternalGeometry = -> [Fusion004]
  FullyConstrained = true
  sketch-geometry (4):
    g0: LineSegment StartX=-1150 StartY=-1150 StartZ=0 EndX=-1150 EndY=1150 EndZ=0
    g1: LineSegment StartX=-1150 StartY=1150 StartZ=0 EndX=1150 EndY=1150 EndZ=0
    g2: LineSegment StartX=1150 StartY=1150 StartZ=0 EndX=1150 EndY=-1150 EndZ=0
    g3: LineSegment StartX=-1150 StartY=-1150 StartZ=0 EndX=1150 EndY=-1150 EndZ=0
  constraints (12):
    c: Vertical(g0)
    c: Coincident(g0,g1)
    c: Horizontal(g1)
    c: Coincident(g1,g2)
    c: Vertical(g2)
    c: DistanceX(g1,g1) = 2300
    c: DistanceX(g-2,g1) = 1150
    c: Coincident(g3,g0)
    c: Coincident(g3,g2)
    c: Horizontal(g3)
    c: DistanceY(g2,g2) = 2300
    c: DistanceY(g-1,g1) = 1150
FEATURE [Part::FeaturePython] ChannelSteel005  # WARN: FeaturePython — macro-defined, semantics opaque (R4)
  B = 75
  H = 150
  L = 1000
  Placement = pos=(-1150,855.871,-150) rot=(0,0,1;0rad)
  Solid = false
  g0 = 7.85
  mass = 0
  size = 3
  standard = SS
  t1 = 6.5
  t2 = 10
FEATURE [Part::Sweep] Sweep001
  Frenet = true
  Sections = -> [ChannelSteel005]
  Solid = true
  Spine = -> Sketch042 [Edge2,Edge3,Edge4,Edge1]
  Transition = 1
FEATURE [Part::MultiFuse] Fusion005  label="Fusion006"
  Refine = true
  Shapes = -> [Fusion004,Sweep001]
FEATURE [Part::FeaturePython] AngleSteel007  # WARN: FeaturePython — macro-defined, semantics opaque (R4)
  A = 75
  B = 75
  L = 700
  Placement = pos=(1800,350,-37.5) rot=(1,0,0;1.5708rad)
  Solid = true
  g0 = 7.85
  mass = 4.79514
  size = 10
  standard = SS_Equal
  t = 6
FEATURE [Part::FeaturePython] Array018  # Draft array (typed FeaturePython)
  AlwaysSyncPlacement = false
  Angle = 360
  ArrayType = 0
  Axis = (0,0,1)
  Base = -> AngleSteel007
  Center = (0,0,0)
  Count = 9
  ExpandArray = false
  Fuse = false
  IntervalAxis = (0,0,0)
  IntervalX = (700,0,0)
  IntervalY = (0,100,0)
  IntervalZ = (0,0,100)
  NumberCircles = 3
  NumberPolar = 5
  NumberX = 9
  NumberY = 1
  NumberZ = 1
  PlacementList = 9 placements: arithmetic series from (1800,350,-37.5) step (700,0,0) to (7400,350,-37.5)
  RadialDistance = 50
  ScaleList = (9) [(1,1,1),(1,1,1),(1,1,1),(1,1,1),(1,1,1),(1,1,1),(1,1,1),(1,1,1),(1,1,1)]
  Symmetry = 1
  TangentialDistance = 25
  expr: NumberX = Spreadsheet006.n
FEATURE [Part::Compound] Compound030
  Links = -> [Fusion003,Clone005]
FEATURE [Part::Compound] Compound031  label="Compound001"
  Links = -> [Compound030,Array018]
FEATURE [Part::FeaturePython] AngleSteel008  # WARN: FeaturePython — macro-defined, semantics opaque (R4)
  A = 75
  B = 75
  L = 325
  Placement = pos=(-642.5,-750,-37.5) rot=(1,0,0;1.5708rad)
  Solid = true
  g0 = 7.85
  mass = 2.22632
  size = 10
  standard = SS_Equal
  t = 6
FEATURE [Part::Mirroring] Mirror022  label="AngleSteel001 (mirrored)"
  Base = (0,0,0)
  Normal = (-1,0,0)
  Source = -> AngleSteel008
FEATURE [Part::Mirroring] Mirror002  label="AngleSteel001 (mirrored)001"
  Base = (0,0,0)
  Normal = (0,1,0)
  Source = -> AngleSteel008
FEATURE [Part::Mirroring] Mirror003  label="AngleSteel001 (mirrored) (mirrored)"
  Base = (0,0,0)
  Normal = (0,1,0)
  Source = -> Mirror022
FEATURE [Part::FeaturePython] HShapeSteel004  label="HShapeSteel005"  # WARN: FeaturePython — macro-defined, semantics opaque (R4)
  B = 150
  H = 194
  L = 850
  Placement = pos=(8075,425,-97) rot=(1,0,0;1.5708rad)
  Solid = true
  g0 = 7.85
  mass = 26.0299
  size = 1
  standard = SS_Medium
  t1 = 6
  t2 = 9
FEATURE [Part::MultiFuse] Fusion006  label="Fusion007"
  Shapes = -> [Compound031]
FEATURE [Part::MultiFuse] Fusion007  label="Fusion008"
  Refine = true
  Shapes = -> [Fusion006,HShapeSteel004]
FEATURE [Part::Mirroring] Mirror023  label="Fusion007 (mirrored)"
  Base = (0,-500,0)
  Normal = (1,0,0)
  Source = -> Fusion007
FEATURE [Sketcher::SketchObject] Sketch043
  ExternalGeometry = -> [Sketch042,Fusion007,Fusion005]
  FullyConstrained = true
  MapMode = 5
  Placement = pos=(0,0,1.92e-13) rot=(0,0,1;0rad)
  Support = -> [Mirror023]
  sketch-geometry (12):
    g0: LineSegment StartX=0 StartY=1150 StartZ=0 EndX=1150 EndY=1150 EndZ=0
    g1: LineSegment StartX=1150 StartY=1150 StartZ=0 EndX=1150 EndY=500 EndZ=0
    g2: LineSegment StartX=1150 StartY=500 StartZ=0 EndX=8150 EndY=500 EndZ=0
    g3: LineSegment StartX=8150 StartY=500 StartZ=0 EndX=8150 EndY=-500 EndZ=0
    g4: LineSegment StartX=8150 StartY=-500 StartZ=0 EndX=1150 EndY=-500 EndZ=0
    g5: LineSegment StartX=1150 StartY=-500 StartZ=0 EndX=1150 EndY=-1150 EndZ=0
    g6: LineSegment StartX=1150 StartY=-1150 StartZ=0 EndX=0 EndY=-1150 EndZ=0
    g7: LineSegment StartX=0 StartY=-1150 StartZ=0 EndX=0 EndY=-675 EndZ=0
    g8: LineSegment StartX=0 StartY=675 StartZ=0 EndX=605 EndY=675 EndZ=0
    g9: LineSegment StartX=605 StartY=675 StartZ=0 EndX=605 EndY=-675 EndZ=0
    g10: LineSegment StartX=605 StartY=-675 StartZ=0 EndX=0 EndY=-675 EndZ=0
    g11: LineSegment StartX=0 StartY=675 StartZ=0 EndX=0 EndY=1150 EndZ=0
  constraints (32):
    c: Horizontal(g0)
    c: Coincident(g0,g1)
    c: Vertical(g1)
    c: Coincident(g1,g2)
    c: Horizontal(g2)
    c: Coincident(g2,g3)
    c: Coincident(g3,g4)
    c: Horizontal(g4)
    c: Coincident(g4,g5)
    c: Coincident(g5,g6)
    c: PointOnObject(g6,g-2)
    c: Horizontal(g6)
    c: Coincident(g6,g7)
    c: Coincident(g11,g0)
    c: Vertical(g7)
    c: Coincident(g-3,g0)
    c: Coincident(g5,g-3)
    c: Coincident(g3,g-4)
    c: Coincident(g2,g-4)
    c: Vertical(g5)
    c: Horizontal(g8)
    c: Coincident(g8,g9)
    c: Vertical(g9)
    c: Coincident(g9,g10)
    c: Horizontal(g10)
    c: Coincident(g7,g10)
    c: Coincident(g11,g8)
    c: Distance(g8,g-5) = 75
    c: Distance(g7,g-6) = 75
    c: DistanceX(g-6,g9) = 75
    c: PointOnObject(g8,g-2)
    c: Vertical(g11)
FEATURE [Part::Extrusion] Extrude038  label="Extrude040"
  Base = -> Sketch043
  Dir = (0,-1e-16,1)
  DirMode = 2
  FaceMakerClass = Part::FaceMakerBullseye
  LengthFwd = 4.5
  LengthRev = 0
  Solid = true
  Symmetric = false
FEATURE [Part::Mirroring] Mirror024  label="Extrude001 (mirrored)"
  Base = (0,2000,0)
  Normal = (1,0,0)
  Source = -> Extrude038
FEATURE [Part::FeaturePython] Channel  label="handrail"  # WARN: FeaturePython — macro-defined, semantics opaque (R4)
  Placement = pos=(0,-1124.19,0) rot=(0,0,1;0rad)
  Reverse = false
  g0 = 7.85
  h = 1100
  k = 90
  l1 = 1125
  l2 = 300
  mass = 31.5207
  p = 1000
  spec = 0
  type = 6
FEATURE [Part::FeaturePython] handrail_001  # a2plus imported part (geometry in sourceFile) (typed FeaturePython)
  Placement = pos=(0,-0.68,0) rot=(0,0,1;0rad)
  a2p_Version = 0.4.60n
  fixedPosition = true
  localSourceObject = Channel
  objectType = a2pPart
  sourceFile = converted
  subassemblyImport = false
  timeLastImport = 1.7091e+09
  updateColors = true
FEATURE [App::FeaturePython] circularEdge_001_mirror  label="circularEdge_001__handrail_001"  # a2plus constraint (typed FeaturePython)
  Object1 = handrail_001
  Object2 = Corner
  SubElement1 = Edge96
  SubElement2 = Edge44
  Suppressed = false
  Type = circularEdge
  directionConstraint = 0
  lockRotation = false
  offset = 0
FEATURE [Part::Mirroring] Mirror025  label="handrail_001 (mirrored)"
  Base = (0,0,4.5)
  Normal = (0,-1,0)
  Source = -> handrail_001
FEATURE [Part::FeaturePython] BasePlate  # WARN: FeaturePython — macro-defined, semantics opaque (R4)
  B = 150
  D = 20
  H = 150
  b1 = 30
  h1 = 45
  sface = 0
FEATURE [Part::Extrusion] Extrude039  label="Extrude041"
  Base = -> BasePlate
  Dir = (0,0,1)
  DirMode = 2
  FaceMakerClass = Part::FaceMakerBullseye
  LengthFwd = 10
  LengthRev = 0
  Placement = pos=(0,0,20) rot=(0,0,1;0rad)
  Solid = true
  Symmetric = false
FEATURE [Part::FeaturePython] H_Shape  # WARN: FeaturePython — macro-defined, semantics opaque (R4)
  B = 150
  H = 150
  L = 80
  Placement = pos=(0,0,20) rot=(0,0,1;0rad)
  Solid = true
  g0 = 7.85
  mass = 2.52071
  size = 2
  standard = SS_Wide
FEATURE [Part::MultiFuse] Fusion008  label="PostH"
  Placement = pos=(-8074.83,-425.97,-294.128) rot=(0,0,1;1.5708rad)
  Shapes = -> [Extrude039,H_Shape]
FEATURE [Part::Mirroring] Mirror026  label="PostH (mirrored)"
  Base = (-8000,1.2506e-12,1.563e-13)
  Normal = (-4e-16,1,0)
  Source = -> Fusion008
FEATURE [Part::Mirroring] Mirror027  label="PostH (mirrored) (mirrored)"
  Base = (0,-400,0)
  Normal = (1,0,0)
  Source = -> Mirror026
FEATURE [Part::Mirroring] Mirror028  label="PostH (mirrored)001"
  Base = (0,-400,0)
  Normal = (1,0,0)
  Source = -> Fusion008
FEATURE [Sketcher::SketchObject] Sketch044
  ExternalGeometry = -> [Fusion007]
  FullyConstrained = false
  MapMode = 5
  Placement = pos=(0,0,1.92e-13) rot=(0,0,1;0rad)
  Support = -> [Fusion007]
  sketch-geometry (3):
    g0: LineSegment StartX=8150 StartY=-428 StartZ=0 EndX=8150 EndY=-878 EndZ=0
    g1: LineSegment StartX=8150 StartY=-878 StartZ=0 EndX=6692.47 EndY=-878 EndZ=0
    g2: LineSegment StartX=6692.47 StartY=-878 StartZ=0 EndX=6692.47 EndY=-428 EndZ=0
  constraints (8):
    c: Vertical(g0)
    c: Coincident(g0,g1)
    c: Horizontal(g1)
    c: Coincident(g1,g2)
    c: Vertical(g2)
    c: Coincident(g0,g-3)
    c: DistanceY(g0,g0) = 450
    c: PointOnObject(g2,g-3)
FEATURE [Part::FeaturePython] ChannelSteel006  # WARN: FeaturePython — macro-defined, semantics opaque (R4)
  B = 75
  H = 150
  L = 1000
  Placement = pos=(6767.42,-671.206,-150) rot=(0,0,1;3.14159rad)
  Solid = false
  g0 = 7.85
  mass = 0
  size = 3
  standard = SS
  t1 = 6.5
  t2 = 10
FEATURE [Part::Sweep] Sweep002
  Frenet = false
  Sections = -> [ChannelSteel006]
  Solid = true
  Spine = -> Sketch044 [Edge3,Edge2,Edge1]
  Transition = 1
FEATURE [Sketcher::SketchObject] Sketch045
  ExternalGeometry = -> [Sketch044,Extrude038]
  FullyConstrained = true
  MapMode = 5
  Placement = pos=(0,0,9.11e-14) rot=(0,0,1;0rad)
  Support = -> [Sweep002]
  sketch-geometry (4):
    g0: LineSegment StartX=6692.47 StartY=-878 StartZ=0 EndX=8150 EndY=-878 EndZ=0
    g1: LineSegment StartX=8150 StartY=-878 StartZ=0 EndX=8150 EndY=-500 EndZ=0
    g2: LineSegment StartX=8150 StartY=-500 StartZ=0 EndX=6692.47 EndY=-500 EndZ=0
    g3: LineSegment StartX=6692.47 StartY=-500 StartZ=0 EndX=6692.47 EndY=-878 EndZ=0
  constraints (10):
    c: Coincident(g0,g1)
    c: Coincident(g1,g2)
    c: Coincident(g2,g3)
    c: Coincident(g3,g0)
    c: Horizontal(g0)
    c: Horizontal(g2)
    c: Vertical(g1)
    c: Vertical(g3)
    c: Coincident(g1,g-4)
    c: Coincident(g0,g-5)
FEATURE [Part::Extrusion] Extrude040  label="Extrude042"
  Base = -> Sketch045
  Dir = (0,-1e-16,1)
  DirMode = 2
  FaceMakerClass = Part::FaceMakerBullseye
  LengthFwd = 4.5
  LengthRev = 0
  Solid = true
  Symmetric = false
FEATURE [App::Part] Part020  label="bridge001"
  Group = -> [Sketch043,HShapeSteel,HShapeSteel001,ChannelSteel005,AngleSteel007,Mirror021,Mirror023,Compound030,Compound031,Array018,Extrude037,Extrude038,HShapeSteel002,Clone004,Clone005,HShapeSteel003,HShapeSteel004,Loft,Fusion007,Sweep001,Sweep,Fusion004,Fusion005,Fusion003,Fusion006,Fusion002,Sketch041,Sketch042,Mirror024,Mirror022,Mirror002,AngleSteel008,Mirror003,Extrude039,BasePlate,H_Shape,Fusion008,+8 more]
  Origin = -> Origin
FEATURE [Part::FeaturePython] Channel001  # WARN: FeaturePython — macro-defined, semantics opaque (R4)
  Placement = pos=(7421,-850.87,-2.27e-13) rot=(0,0,1;0rad)
  Reverse = false
  g0 = 7.85
  h = 1100
  k = 90
  l1 = 700
  l2 = 200
  mass = 20.0308
  p = 1000
  spec = 0
  type = 6
FEATURE [Part::FeaturePython] Corner001  # WARN: FeaturePython — macro-defined, semantics opaque (R4)
  Placement = pos=(6325,-474.87,-2.27e-13) rot=(0,0,1;0rad)
  Reverse = false
  g0 = 7.85
  h = 1100
  k = -90
  l1 = 396
  l2 = 176
  mass = 4.57145
  p = 1000
  spec = 0
  type = 2
FEATURE [Part::FeaturePython] Compound003_001  # a2plus imported part (geometry in sourceFile) (typed FeaturePython)
  a2p_Version = 0.4.60n
  fixedPosition = true
  localSourceObject = Compound003
  objectType = a2pPart
  sourceFile = converted
  subassemblyImport = false
  timeLastImport = 1.70947e+09
  updateColors = true
FEATURE [App::FeaturePython] circularEdge_002  label="circularEdge_002__Corner001"  # a2plus constraint (typed FeaturePython)
  Object1 = Compound003_001
  Object2 = Corner001
  ParentTreeObject = -> Compound003_001
  SubElement1 = Edge689
  SubElement2 = Edge10
  Suppressed = false
  Type = circularEdge
  directionConstraint = 0
  lockRotation = false
  offset = 0
FEATURE [App::FeaturePython] circularEdge_002_mirror  label="circularEdge_002__Compound003_001"  # a2plus constraint (typed FeaturePython)
  Object1 = Compound003_001
  Object2 = Corner001
  ParentTreeObject = -> Corner001
  SubElement1 = Edge689
  SubElement2 = Edge10
  Suppressed = false
  Type = circularEdge
  directionConstraint = 0
  lockRotation = false
  offset = 0
FEATURE [App::FeaturePython] circularEdge_003  label="circularEdge_003__Channel001"  # a2plus constraint (typed FeaturePython)
  Object1 = Corner001
  Object2 = Channel001
  ParentTreeObject = -> Corner001
  SubElement1 = Edge2
  SubElement2 = Edge93
  Suppressed = false
  Type = circularEdge
  directionConstraint = 0
  lockRotation = false
  offset = 0
FEATURE [App::FeaturePython] circularEdge_003_mirror  label="circularEdge_003__Corner001"  # a2plus constraint (typed FeaturePython)
  Object1 = Corner001
  Object2 = Channel001
  ParentTreeObject = -> Channel001
  SubElement1 = Edge2
  SubElement2 = Edge93
  Suppressed = false
  Type = circularEdge
  directionConstraint = 0
  lockRotation = false
  offset = 0
FEATURE [Part::FeaturePython] StraightLine  # WARN: FeaturePython — macro-defined, semantics opaque (R4)
  Placement = pos=(6325,474.87,-2.27e-13) rot=(0,0,1;0rad)
  Reverse = false
  g0 = 7.85
  h = 1100
  l1 = 1800
  mass = 27.8373
  p = 500
  spec = 0
  type = 0
FEATURE [Part::FeaturePython] Corner  # WARN: FeaturePython — macro-defined, semantics opaque (R4)
  Placement = pos=(-1125,824.87,-1.14e-13) rot=(0,0,-1;1.5708rad)
  Reverse = false
  g0 = 7.85
  h = 1100
  k = -90
  l1 = 350
  l2 = 6700
  mass = 95.3604
  p = 500
  spec = 0
  type = 2
FEATURE [Part::FeaturePython] handrail_001__mirrored__001  label="handrail_001 (mirrored)_001"  # a2plus imported part (geometry in sourceFile) (typed FeaturePython)
  a2p_Version = 0.4.60n
  fixedPosition = true
  localSourceObject = Mirror006
  objectType = a2pPart
  sourceFile = converted
  subassemblyImport = false
  timeLastImport = 1.70947e+09
  updateColors = true
FEATURE [App::FeaturePython] circularEdge_001  label="circularEdge_001__Corner"  # a2plus constraint (typed FeaturePython)
  Object1 = handrail_001__mirrored__001
  Object2 = Corner
  ParentTreeObject = -> handrail_001__mirrored__001
  SubElement1 = Edge107
  SubElement2 = Edge17
  Suppressed = false
  Type = circularEdge
  directionConstraint = 0
  lockRotation = false
  offset = 0
FEATURE [App::FeaturePython] circularEdge_001_mirror002  label="circularEdge_001__handrail_001 (mirrored)_001"  # a2plus constraint (typed FeaturePython)
  Object1 = handrail_001__mirrored__001
  Object2 = Corner
  ParentTreeObject = -> Corner
  SubElement1 = Edge107
  SubElement2 = Edge17
  Suppressed = false
  Type = circularEdge
  directionConstraint = 0
  lockRotation = false
  offset = 0
FEATURE [Part::Mirroring] Mirror029  label="Corner (mirrored)"
  Base = (0,0,0)
  Normal = (0,1,0)
  Source = -> Corner
FEATURE [App::Part] Part021  label="handrail001"
  Group = -> [Channel,handrail_001,circularEdge_001_mirror,Mirror025,Channel001,Corner001,Compound003_001,StraightLine,Corner,circularEdge_003,circularEdge_002_mirror,circularEdge_003_mirror,handrail_001__mirrored__001,circularEdge_001_mirror002,Mirror029]
  Origin = -> Origin023
FEATURE [Part::FeaturePython] b_reducerCover1_001_  label="reducerCover1_001"  # a2plus imported part (geometry in sourceFile) (typed FeaturePython)
  Placement = pos=(2.69,0.62,-5683.46) rot=(0,0,1;0rad)
  a2p_Version = 0.4.60n
  fixedPosition = false
  objectType = a2pPart
  sourceFile = .\reducerCover.step
  subassemblyImport = false
  timeLastImport = 1.70943e+09
  updateColors = true
FEATURE [App::Part] Part022  label="bridge"
  Group = -> [Part021,Part020,Spreadsheet006,b_reducerCover1_001_]
  Origin = -> Origin024
  Placement = pos=(0,0,5690) rot=(0,0,1;0rad)
FEATURE [Part::FeaturePython] SquarePipe  # WARN: FeaturePython — macro-defined, semantics opaque (R4)
  A = 125
  B = 125
  L = 5950
  Placement = pos=(0,0,0) rot=(0,-1,0;1.5708rad)
  Solid = true
  g0 = 7.85
  mass = 109.091
  size = 39
  standard = SS
  t = 1
  expr: L = Spreadsheet007.L0
FEATURE [Sketcher::SketchObject] Sketch046
  ExternalGeometry = -> [SquarePipe]
  FullyConstrained = true
  MapMode = 5
  Placement = pos=(-5950,6.606e-13,1.3212e-12) rot=(0,-1,0;1.5708rad)
  Support = -> [SquarePipe]
  sketch-geometry (4):
    g0: LineSegment StartX=-62.5 StartY=-62.5 StartZ=0 EndX=62.5 EndY=-62.5 EndZ=0
    g1: LineSegment StartX=62.5 StartY=-62.5 StartZ=0 EndX=62.5 EndY=62.5 EndZ=0
    g2: LineSegment StartX=62.5 StartY=62.5 StartZ=0 EndX=-62.5 EndY=62.5 EndZ=0
    g3: LineSegment StartX=-62.5 StartY=62.5 StartZ=0 EndX=-62.5 EndY=-62.5 EndZ=0
  constraints (11):
    c: Coincident(g0,g1)
    c: Coincident(g1,g2)
    c: Coincident(g2,g3)
    c: Coincident(g3,g0)
    c: Horizontal(g0)
    c: Horizontal(g2)
    c: Vertical(g3)
    c: DistanceX(g2,g2) = 125
    c: Equal(g1,g0)
    c: PointOnObject(g-4,g2)
    c: Tangent(g-3,g1) = -1.5708
FEATURE [Part::Extrusion] Extrude041  label="Extrude043"
  Base = -> Sketch046
  Dir = (-1,1e-16,2e-16)
  DirMode = 2
  FaceMakerClass = Part::FaceMakerBullseye
  LengthFwd = 6
  LengthRev = 0
  Solid = true
  Symmetric = false
FEATURE [Part::FeaturePython] Clone006  label="Extrude044"  # Draft clone (typed FeaturePython)
  AttacherType = Attacher::AttachEngine3D
  Fuse = false
  Objects = -> [Extrude041]
  Placement = pos=(5956,0,0) rot=(0,0,1;0rad)
  Scale = (1,1,1)
  expr: .Placement.Base.x = Spreadsheet007.L0 + 6
FEATURE [Spreadsheet::Sheet] Spreadsheet007
  cells = A1='tankDia   D0; B1(D0)=15500; A2='L; B2(L0)=5950; A3='bradeWidth W0; B3(W0)==D0 / 4 + 300; A4='brade      n0; B4(n0)=5; A5='brade     w1; B5(w1)=890
FEATURE [Sketcher::SketchObject] Sketch047  label="skimmerBrade"
  ExternalGeometry = -> [Clone006]
  FullyConstrained = true
  Placement = pos=(0,0,0) rot=(1,0,0;1.5708rad)
  sketch-geometry (7):
    g0: LineSegment StartX=6 StartY=62.5 StartZ=0 EndX=36 EndY=62.5 EndZ=0
    g1: LineSegment StartX=36 StartY=62.5 StartZ=0 EndX=100.694 EndY=26.1551 EndZ=0
    g2: ArcOfCircle CenterX=86 CenterY=0 CenterZ=0 NormalX=0 NormalY=0 NormalZ=1 AngleXU=0 Radius=30 StartAngle=5.22424 EndAngle=7.34213
    g3: LineSegment StartX=100.694 StartY=-26.1551 StartZ=0 EndX=36 EndY=-62.5 EndZ=0
    g4: LineSegment StartX=36 StartY=-62.5 StartZ=0 EndX=6 EndY=-62.5 EndZ=0
    g5: LineSegment StartX=6 StartY=-62.5 StartZ=0 EndX=6 EndY=62.5 EndZ=0
    g6: Circle CenterX=86 CenterY=0 CenterZ=0 NormalX=0 NormalY=0 NormalZ=1 AngleXU=0 Radius=13
  constraints (17):
    c: Horizontal(g0)
    c: Coincident(g0,g1)
    c: Tangent(g1,g2) = 1.5708
    c: Coincident(g3,g4)
    c: Coincident(g4,g5)
    c: Coincident(g5,g0)
    c: PointOnObject(g6,g-1)
    c: Coincident(g0,g-3)
    c: Coincident(g4,g-3)
    c: Horizontal(g4)
    c: DistanceX(g0,g0) = 30
    c: Equal(g0,g4)
    c: Coincident(g2,g6)
    c: DistanceX(g4,g2) = 80
    c: Diameter(g6) = 26
    c: Radius(g2) = 30
    c: Tangent(g2,g3) = 1.5708
FEATURE [Part::Extrusion] Extrude042  label="Extrude045"
  Base = -> Sketch047
  Dir = (0,-1,2e-16)
  DirMode = 2
  FaceMakerClass = Part::FaceMakerBullseye
  LengthFwd = 10
  LengthRev = 0
  Solid = true
  Symmetric = true
FEATURE [Sketcher::SketchObject] Sketch048
  FullyConstrained = false
  Placement = pos=(0,0,0) rot=(1,0,0;1.5708rad)
  sketch-geometry (7):
    g0: ArcOfCircle CenterX=81.7032 CenterY=0 CenterZ=0 NormalX=0 NormalY=0 NormalZ=1 AngleXU=0 Radius=30 StartAngle=2.05435 EndAngle=4.1734
    g1: LineSegment StartX=67.7553 StartY=26.5604 StartZ=0 EndX=131.703 EndY=60.1419 EndZ=0
    g2: LineSegment StartX=131.703 StartY=60.1419 StartZ=0 EndX=161.703 EndY=60.1419 EndZ=0
    g3: LineSegment StartX=161.703 StartY=60.1419 StartZ=0 EndX=161.703 EndY=-64.8581 EndZ=0
    g4: LineSegment StartX=161.703 StartY=-64.8581 StartZ=0 EndX=131.703 EndY=-64.8581 EndZ=0
    g5: LineSegment StartX=131.703 StartY=-64.8581 StartZ=0 EndX=66.3053 EndY=-25.7469 EndZ=0
    g6: Circle CenterX=81.7032 CenterY=0 CenterZ=0 NormalX=0 NormalY=0 NormalZ=1 AngleXU=0 Radius=13
  constraints (17):
    c: PointOnObject(g0,g-1)
    c: Coincident(g1,g2)
    c: Horizontal(g2)
    c: Coincident(g2,g3)
    c: Coincident(g3,g4)
    c: Coincident(g4,g5)
    c: Tangent(g0,g5) = 1.5708
    c: Tangent(g0,g1) = 1.5708
    c: Vertical(g3)
    c: Distance(g0,g3) = 80
    c: Horizontal(g4)
    c: DistanceX(g2,g2) = 30
    c: Equal(g2,g4)
    c: Radius(g0) = 30
    c: Coincident(g6,g0)
    c: Diameter(g6) = 26
    c: DistanceY(g3,g3) = 125
FEATURE [Part::Extrusion] Extrude043  label="Extrude046"
  Base = -> Sketch048
  Dir = (0,-1,2e-16)
  DirMode = 2
  FaceMakerClass = Part::FaceMakerBullseye
  LengthFwd = 6
  LengthRev = 0
  Placement = pos=(0,9,0) rot=(0,0,1;0rad)
  Solid = true
  Symmetric = true
FEATURE [Sketcher::SketchObject] Sketch049
  ExternalGeometry = -> [Extrude043]
  FullyConstrained = false
  MapMode = 5
  Placement = pos=(161.703,9,0) rot=(0.57735,0.57735,0.57735;2.0944rad)
  Support = -> [Extrude043]
  sketch-geometry (4):
    g0: LineSegment StartX=-59 StartY=-64.8581 StartZ=0 EndX=41 EndY=-64.8581 EndZ=0
    g1: LineSegment StartX=41 StartY=-64.8581 StartZ=0 EndX=41 EndY=60.1419 EndZ=0
    g2: LineSegment StartX=41 StartY=60.1419 StartZ=0 EndX=-59 EndY=60.1419 EndZ=0
    g3: LineSegment StartX=-59 StartY=60.1419 StartZ=0 EndX=-59 EndY=-64.8581 EndZ=0
  constraints (8):
    c: Coincident(g0,g3)
    c: Coincident(g2,g3)
    c: Coincident(g0,g1)
    c: Coincident(g1,g2)
    c: DistanceY(g1,g1) = 125
    c: Horizontal(g2)
    c: Horizontal(g0)
    c: PointOnObject(g-3,g2)
FEATURE [Part::Extrusion] Extrude044  label="Extrude047"
  Base = -> Sketch049
  Dir = (1,0,0)
  DirMode = 2
  FaceMakerClass = Part::FaceMakerBullseye
  LengthFwd = 10
  LengthRev = 0
  Solid = true
  Symmetric = false
FEATURE [Part::Feature] Part__Feature011  label="CNROK75-U_b"
  shape: bbox 47.01 x 65.51 x 70.01 mm, 58 faces (baked)
FEATURE [Part::Feature] Part__Feature012  label="CNROK75-U_w"
  shape: bbox 41.3 x 78.6 x 78.6 mm, 86 faces (baked)
FEATURE [App::Part] CNROK75_U  label="CNROK75-U"
  Group = -> [Part__Feature011,Part__Feature012]
  Origin = -> Origin028
  Placement = pos=(-5931,2.9e-14,-118.52) rot=(1,0,0;1.5708rad)
FEATURE [Part::FeaturePython] Clone007  label="Extrude048"  # Draft clone (typed FeaturePython)
  AttacherType = Attacher::AttachEngine3D
  Fuse = false
  Objects = -> [Extrude043]
  Placement = pos=(0,-9,0) rot=(0,0,1;0rad)
  Scale = (1,1,1)
FEATURE [App::Part] Part024  label="gusset002"
  Group = -> [Sketch048,Sketch049,Extrude043,Extrude044,Clone007]
  Origin = -> Origin026
  Placement = pos=(4,0,0) rot=(0,0,1;0rad)
FEATURE [App::FeaturePython] axisCoincident_001_mirror  label="axisCoincident_001__gusset001"  # a2plus constraint (typed FeaturePython)
  Object1 = Compound001
  Object2 = Compound_001
  SubElement1 = Edge54
  SubElement2 = Edge93
  Suppressed = false
  Type = axial
  directionConstraint = 0
  lockRotation = false
FEATURE [Part::Feature] Part__Feature002  label="HNS3L_1"
  shape: bbox 64 x 7.5 x 21.75 mm, 15 faces (baked)
FEATURE [Part::Feature] Part__Feature003  label="HNS3L_2"
  shape: bbox 64 x 7.5 x 21.75 mm, 12 faces (baked)
FEATURE [App::Part] HNS3L
  Group = -> [Part__Feature002,Part__Feature003]
  Origin = -> Origin029
  Placement = pos=(-395,-8,115) rot=(1,0,0;3.14159rad)
  expr: .Placement.Base.x = -Spreadsheet007.w1 / 2 + 50
FEATURE [Sketcher::SketchObject] Sketch050
  FullyConstrained = true
  Placement = pos=(0,0,0) rot=(1,0,0;1.5708rad)
  expr: Constraints[10] = Spreadsheet007.w1
  sketch-geometry (5):
    g0: LineSegment StartX=-445 StartY=-107.5 StartZ=0 EndX=-445 EndY=107.5 EndZ=0
    g1: LineSegment StartX=-445 StartY=107.5 StartZ=0 EndX=445 EndY=107.5 EndZ=0
    g2: LineSegment StartX=445 StartY=107.5 StartZ=0 EndX=445 EndY=-107.5 EndZ=0
    g3: LineSegment StartX=445 StartY=-107.5 StartZ=0 EndX=-445 EndY=-107.5 EndZ=0
    g4: GeomPoint X=0 Y=0 Z=0
  constraints (12):
    c: Coincident(g0,g1)
    c: Coincident(g1,g2)
    c: Coincident(g2,g3)
    c: Coincident(g3,g0)
    c: Horizontal(g1)
    c: Horizontal(g3)
    c: Vertical(g0)
    c: Vertical(g2)
    c: Symmetric(g1,g0,g4)
    c: Coincident(g4,g-1)
    c: Distance(g1) = 890
    c: DistanceY(g2,g2) = 215
FEATURE [Part::Extrusion] Extrude045  label="Extrude049"
  Base = -> Sketch050
  Dir = (0,-1,2e-16)
  DirMode = 2
  FaceMakerClass = Part::FaceMakerBullseye
  LengthFwd = 5
  LengthRev = 0
  Placement = pos=(0,-4.5,-12) rot=(0,0,1;0rad)
  Solid = true
  Symmetric = false
FEATURE [Part::FeaturePython] Clone008  label="HNS3L001"  # Draft clone (typed FeaturePython)
  AttacherType = Attacher::AttachEngine3D
  Fuse = false
  Objects = -> [HNS3L]
  Placement = pos=(331,-8,115) rot=(1,0,0;3.14159rad)
  Scale = (1,1,1)
  expr: .Placement.Base.x = Spreadsheet007.w1 / 2 - 114
FEATURE [Sketcher::SketchObject] Sketch051
  FullyConstrained = true
  Placement = pos=(0,0,0) rot=(1,0,0;1.5708rad)
  expr: Constraints[11] = Spreadsheet007.w1
  sketch-geometry (5):
    g0: LineSegment StartX=-445 StartY=-37.5 StartZ=0 EndX=-445 EndY=37.5 EndZ=0
    g1: LineSegment StartX=-445 StartY=37.5 StartZ=0 EndX=445 EndY=37.5 EndZ=0
    g2: LineSegment StartX=445 StartY=37.5 StartZ=0 EndX=445 EndY=-37.5 EndZ=0
    g3: LineSegment StartX=445 StartY=-37.5 StartZ=0 EndX=-445 EndY=-37.5 EndZ=0
    g4: GeomPoint X=0 Y=0 Z=0
  constraints (12):
    c: Coincident(g0,g1)
    c: Coincident(g1,g2)
    c: Coincident(g2,g3)
    c: Coincident(g3,g0)
    c: Horizontal(g1)
    c: Horizontal(g3)
    c: Vertical(g0)
    c: Vertical(g2)
    c: Symmetric(g1,g0,g4)
    c: Coincident(g4,g-1)
    c: DistanceY(g2,g2) = 75
    c: DistanceX(g3,g3) = 890
FEATURE [Part::Extrusion] Extrude046  label="Extrude050"
  Base = -> Sketch051
  Dir = (0,-1,2e-16)
  DirMode = 2
  FaceMakerClass = Part::FaceMakerBullseye
  LengthFwd = 3
  LengthRev = 0
  Placement = pos=(0,-9.5,70) rot=(0,0,1;0rad)
  Solid = true
  Symmetric = false
FEATURE [Sketcher::SketchObject] Sketch052
  ExternalGeometry = -> [Extrude045,Extrude046]
  FullyConstrained = true
  MapMode = 5
  Placement = pos=(-445,-4.5,-12) rot=(0.57735,-0.57735,-0.57735;2.0944rad)
  Support = -> [Extrude045]
  sketch-geometry (4):
    g0: LineSegment StartX=2.4e-14 StartY=107.5 StartZ=0 EndX=-3 EndY=107.5 EndZ=0
    g1: LineSegment StartX=-3 StartY=107.5 StartZ=0 EndX=-3 EndY=44.5 EndZ=0
    g2: LineSegment StartX=-3 StartY=44.5 StartZ=0 EndX=2.4e-14 EndY=44.5 EndZ=0
    g3: LineSegment StartX=2.4e-14 StartY=44.5 StartZ=0 EndX=2.4e-14 EndY=107.5 EndZ=0
  constraints (11):
    c: Coincident(g0,g1)
    c: Coincident(g1,g2)
    c: Coincident(g2,g3)
    c: Coincident(g3,g0)
    c: Horizontal(g0)
    c: Horizontal(g2)
    c: Vertical(g1)
    c: Vertical(g3)
    c: DistanceX(g0,g0) = 3
    c: Coincident(g0,g-3)
    c: Horizontal(g1,g-4)
FEATURE [Part::Extrusion] Extrude047  label="Extrude051"
  Base = -> Sketch052
  Dir = (-1,0,0)
  DirMode = 2
  FaceMakerClass = Part::FaceMakerBullseye
  LengthFwd = 890
  LengthRev = 0
  Reversed = true
  Solid = true
  Symmetric = false
  expr: LengthFwd = Spreadsheet007.w1
FEATURE [Sketcher::SketchObject] Sketch053
  FullyConstrained = false
  MapMode = 5
  Placement = pos=(-445,-4.5,-12) rot=(0.57735,-0.57735,-0.57735;2.0944rad)
  Support = -> [Extrude045]
  sketch-geometry (8):
    g0: LineSegment StartX=-104.645 StartY=156.908 StartZ=0 EndX=-4.64507 EndY=156.908 EndZ=0
    g1: LineSegment StartX=3.35493 StartY=148.908 StartZ=0 EndX=3.35493 EndY=130.908 EndZ=0
    g2: LineSegment StartX=3.35493 StartY=130.908 StartZ=0 EndX=0.354931 EndY=130.908 EndZ=0
    g3: LineSegment StartX=0.354931 StartY=130.908 StartZ=0 EndX=0.354931 EndY=148.908 EndZ=0
    g4: LineSegment StartX=-4.64507 StartY=153.908 StartZ=0 EndX=-104.645 EndY=153.908 EndZ=0
    g5: LineSegment StartX=-104.645 StartY=153.908 StartZ=0 EndX=-104.645 EndY=156.908 EndZ=0
    g6: ArcOfCircle CenterX=-4.64507 CenterY=148.908 CenterZ=0 NormalX=0 NormalY=0 NormalZ=1 AngleXU=0 Radius=5 StartAngle=3.3e-15 EndAngle=1.5708
    g7: ArcOfCircle CenterX=-4.64507 CenterY=148.908 CenterZ=0 NormalX=0 NormalY=0 NormalZ=1 AngleXU=0 Radius=8 StartAngle=-1.8e-15 EndAngle=1.5708
  constraints (19):
    c: Horizontal(g0)
    c: Vertical(g1)
    c: Coincident(g1,g2)
    c: Horizontal(g2)
    c: Coincident(g2,g3)
    c: Vertical(g3)
    c: Horizontal(g4)
    c: Coincident(g4,g5)
    c: Coincident(g5,g0)
    c: Vertical(g5)
    c: DistanceX(g2,g2) = 3
    c: Tangent(g3,g6) = -1.5708
    c: Tangent(g4,g6) = -1.5708
    c: Tangent(g1,g7) = 1.5708
    c: Tangent(g0,g7) = 1.5708
    c: Coincident(g6,g7)
    c: DistanceX(g4,g4) = 100
    c: DistanceY(g3,g3) = 18
    c: Radius(g6) = 5
FEATURE [Part::Extrusion] Extrude048  label="Extrude052"
  Base = -> Sketch053
  Dir = (-1,0,0)
  DirMode = 2
  FaceMakerClass = Part::FaceMakerBullseye
  LengthFwd = 80
  LengthRev = 0
  Placement = pos=(34,0,0) rot=(0,0,1;0rad)
  Reversed = true
  Solid = true
  Symmetric = false
FEATURE [Part::FeaturePython] Clone009  label="Extrude053"  # Draft clone (typed FeaturePython)
  AttacherType = Attacher::AttachEngine3D
  Fuse = false
  Objects = -> [Extrude048]
  Placement = pos=(760,0,0) rot=(0,0,1;0rad)
  Scale = (1,1,1)
  expr: .Placement.Base.x = Spreadsheet007.w1 - (50 + 46 + 34)
FEATURE [App::Part] Part026  label="brade001"
  Group = -> [Sketch050,Extrude045,Clone008,HNS3L,Sketch051,Extrude046,Sketch052,Extrude047,Sketch053,Extrude048,Clone009]
  Origin = -> Origin030
  Placement = pos=(-5437.87,-100,-207.547) rot=(0,0,1;0rad)
FEATURE [Part::FeaturePython] Array019  label="brade002"  # Draft array (typed FeaturePython)
  AlwaysSyncPlacement = false
  Angle = 360
  ArrayType = 0
  Axis = (0,0,1)
  Base = -> Part026
  Center = (0,0,0)
  Count = 6
  ExpandArray = false
  Fuse = false
  IntervalAxis = (0,0,0)
  IntervalX = (890,0,0)
  IntervalY = (0,100,0)
  IntervalZ = (0,0,100)
  NumberCircles = 3
  NumberPolar = 5
  NumberX = 6
  NumberY = 1
  NumberZ = 1
  PlacementList = 6 placements: arithmetic series from (-5437.87,-100,-207.547) step (890,0,0) to (-987.869,-100,-207.547)
  RadialDistance = 50
  ScaleList = (6) [(1,1,1),(1,1,1),(1,1,1),(1,1,1),(1,1,1),(1,1,1)]
  Symmetry = 1
  TangentialDistance = 25
  expr: .IntervalX.x = Spreadsheet007.w1
FEATURE [Part::FeaturePython] ChannelSteel007  # WARN: FeaturePython — macro-defined, semantics opaque (R4)
  B = 75
  H = 150
  L = 1000
  Placement = pos=(176,0,-75) rot=(0,0,1;0rad)
  Solid = false
  g0 = 7.85
  mass = 0
  size = 3
  standard = SS
  t1 = 6.5
  t2 = 10
FEATURE [Part::Extrusion] Extrude049  label="Extrude054"
  Base = -> ChannelSteel007
  Dir = (0,1,0)
  DirMode = 2
  FaceMakerClass = Part::FaceMakerBullseye
  LengthFwd = 1620
  LengthRev = 0
  Solid = false
  Symmetric = true
FEATURE [Sketcher::SketchObject] Sketch054
  FullyConstrained = true
  MapMode = 5
  Placement = pos=(0,0,62.5) rot=(0,0,1;0rad)
  sketch-geometry (6):
    g0: LineSegment StartX=-2985 StartY=62.5 StartZ=0 EndX=-2985 EndY=112.5 EndZ=0
    g1: ArcOfCircle CenterX=-3000 CenterY=112.5 CenterZ=0 NormalX=0 NormalY=0 NormalZ=1 AngleXU=0 Radius=15 StartAngle=0 EndAngle=1.98689
    g2: LineSegment StartX=-3006.06 StartY=126.22 StartZ=0 EndX=-3105 EndY=82.5 EndZ=0
    g3: LineSegment StartX=-3105 StartY=82.5 StartZ=0 EndX=-3105 EndY=62.5 EndZ=0
    g4: LineSegment StartX=-3105 StartY=62.5 StartZ=0 EndX=-2985 EndY=62.5 EndZ=0
    g5: Circle CenterX=-3000 CenterY=112.5 CenterZ=0 NormalX=0 NormalY=0 NormalZ=1 AngleXU=0 Radius=7.5
  constraints (16):
    c: Tangent(g0,g1) = -1.5708
    c: Coincident(g2,g3)
    c: Vertical(g3)
    c: Coincident(g3,g4)
    c: Coincident(g4,g0)
    c: Coincident(g5,g1)
    c: Diameter(g5) = 15
    c: Radius(g1) = 15
    c: Vertical(g0)
    c: Tangent(g1,g2) = -1.5708
    c: Horizontal(g4)
    c: DistanceY(g3,g3) = 20
    c: DistanceX(g4,g4) = 120
    c: DistanceY(g0,g1) = 50
    c: DistanceY(g-1,g0) = 62.5
    c: DistanceX(g-2,g1) = -3000
FEATURE [Part::Extrusion] Extrude050  label="Extrude055"
  Base = -> Sketch054
  Dir = (0,0,1)
  DirMode = 2
  FaceMakerClass = Part::FaceMakerBullseye
  LengthFwd = 6
  LengthRev = 0
  Placement = pos=(0,0,-62.5) rot=(0,0,1;0rad)
  Solid = true
  Symmetric = true
FEATURE [Part::Mirroring] Mirror030  label="Extrude020 (mirrored)"
  Base = (-3100,0,0)
  Normal = (0,-1,0)
  Source = -> Extrude050
FEATURE [App::Part] Part023  label="hontai"
  Group = -> [Sketch047,Clone006,SquarePipe,Sketch046,Extrude041,Extrude042,Sketch054,Extrude050,Mirror030]
  Origin = -> Origin025
FEATURE [Part::Compound] Compound032  label="hontai001"
  Links = -> [Part023]
FEATURE [Sketcher::SketchObject] Sketch055
  ExternalGeometry = -> [Extrude049]
  FullyConstrained = false
  MapMode = 5
  Placement = pos=(0,0,75) rot=(0,0,1;0rad)
  Support = -> [Extrude049]
  sketch-geometry (7):
    g0: LineSegment StartX=176 StartY=810 StartZ=0 EndX=156 EndY=810 EndZ=0
    g1: LineSegment StartX=156 StartY=810 StartZ=0 EndX=118.097 EndY=782.842 EndZ=0
    g2: ArcOfCircle CenterX=126 CenterY=771.812 CenterZ=0 NormalX=0 NormalY=0 NormalZ=1 AngleXU=0 Radius=13.569 StartAngle=2.19251 EndAngle=4.2132
    g3: LineSegment StartX=119.504 StartY=759.899 StartZ=0 EndX=156 EndY=740 EndZ=0
    g4: LineSegment StartX=156 StartY=740 StartZ=0 EndX=176 EndY=740 EndZ=0
    g5: LineSegment StartX=176 StartY=740 StartZ=0 EndX=176 EndY=810 EndZ=0
    g6: Circle CenterX=126 CenterY=771.812 CenterZ=0 NormalX=0 NormalY=0 NormalZ=1 AngleXU=0 Radius=7.5
  constraints (16):
    c: Horizontal(g0)
    c: Coincident(g0,g1)
    c: Tangent(g1,g2) = -1.5708
    c: Coincident(g3,g4)
    c: Horizontal(g4)
    c: Coincident(g4,g5)
    c: Coincident(g5,g0)
    c: Vertical(g5)
    c: Coincident(g6,g2)
    c: Diameter(g6) = 15
    c: Coincident(g0,g-3)
    c: DistanceY(g5,g5) = 70
    c: Tangent(g2,g3) = -1.5708
    c: Vertical(g0,g3)
    c: DistanceX(g0,g0) = 20
    c: Distance(g2,g5) = 50
FEATURE [Part::Extrusion] Extrude051  label="Extrude056"
  Base = -> Sketch055
  Dir = (0,0,1)
  DirMode = 2
  FaceMakerClass = Part::FaceMakerBullseye
  LengthFwd = 6
  LengthRev = 0
  Placement = pos=(0,0,-75) rot=(0,0,1;0rad)
  Solid = true
  Symmetric = true
FEATURE [Part::Mirroring] Mirror031  label="Extrude021 (mirrored)"
  Base = (1000,0,0)
  Normal = (0,-1,0)
  Source = -> Extrude051
FEATURE [Spreadsheet::Sheet] Spreadsheet008  label="Spreadsheet002"
  cells = A2='rodDia dia; B2(dia)=12; C2='thickness; D2(t0)=6; A3='length L0; B3(L0)=3195; C3='l1; D3(l1)==L0 - (dia * 5 + 500); B4='l; C4='l1; D4='a; E4='b; F4='c; G4='e; H4='f; I4='g; J4='h; K4='i; L4='r; A5='forkEndR; B5=80; D5=25; E5=10; F5=14; G5=16; H5=13; I5=40; J5=5; K5=13; L5=15; A6='turnBackle; B6=100; C6=20; D6=30; E6=16; F6=22; A7='forkEndL; B7=60; D7=25; E7=10; F7=13; G7=16; H7=13; I7=20; L7=15; A8=1; B8=2; C8=3; D8=4; E8=5; F8=6; G8=7; H8=8; I8=9; J8=10; K8=11; L8=12; A9='turnBackle; A10='d; B10='l; C10='l1; D10='a; E10='b; F10='c; G10='t0; A11=10; B11=75; C11=15; D11=24; E11=13; F11=17; G11=6; A12=12; B12=100; C12=20; D12=30; E12=16; F12=22; G12=6; A13=16; B13=125; C13=24; D13=36; E13=20; F13=27; G13=9; A14=20; B14=150; C14=28; D14=42; E14=23; F14=33; G14=9; A15=22; B15=175; C15=33; D15=48; E15=27; F15=37; G15=9; A16=24; B16=200; C16=38; D16=54; E16=30; F16=42; G16=12; A17=30; B17=250; C17=47; D17=66; E17=37; F17=52; G17=12; A18='forkEnd_L; A19='d; B19='l; C19='a; D19='b; E19='c; F19='e; G19='f; H19='g; I19='r; A20=10; B20=50; C20=20; D20=7; E20=10; F20=12; G20=10; H20=15; I20=12; A21=12; B21=60; C21=25; D21=10; E21=13; F21=16; G21=13; H21=20; I21=15; A22=16; B22=75; C22=30; D22=13; E22=16; F22=20; G22=16; H22=25; I22=19; A23=20; B23=90; C23=40; D23=16; E23=20; F23=24; G23=20; H23=30; I23=23; A24=22; B24=100; C24=45; D24=20; E24=23; F24=28; G24=23; H24=35; I24=27; A25=24; B25=115; C25=50; D25=23; E25=26; F25=32; G25=26; H25=40; I25=30; A26=30; B26=140; C26=65; D26=30; E26=33; F26=40; G26=33; H26=50; I26=38; A27='forkEnd_R; A28='d; B28='l; C28='a; D28='b; E28='c; F28='r; G28='e; H28='f; I28='g; J28='h; K28='i; A29=10; +76 more cells
FEATURE [Sketcher::SketchObject] Sketch056
  FullyConstrained = true
  Placement = pos=(0,0,0) rot=(1,0,0;1.5708rad)
  expr: Constraints[11] = Spreadsheet008.I5 + Spreadsheet008.dia * 2
  expr: Constraints[1] = Spreadsheet008.F5 / 2
  expr: Constraints[3] = Spreadsheet008.L5
  sketch-geometry (5):
    g0: Circle CenterX=0 CenterY=0 CenterZ=0 NormalX=0 NormalY=0 NormalZ=1 AngleXU=0 Radius=7
    g1: ArcOfCircle CenterX=0 CenterY=0 CenterZ=0 NormalX=0 NormalY=0 NormalZ=1 AngleXU=0 Radius=15 StartAngle=4.71239 EndAngle=7.85398
    g2: LineSegment StartX=-4.87e-14 StartY=15 StartZ=0 EndX=-64 EndY=15 EndZ=0
    g3: LineSegment StartX=-64 StartY=15 StartZ=0 EndX=-64 EndY=-15 EndZ=0
    g4: LineSegment StartX=-64 StartY=-15 StartZ=0 EndX=0 EndY=-15 EndZ=0
  constraints (12):
    c: Coincident(g0,g-1)
    c: Radius(g0) = 7
    c: Coincident(g1,g0)
    c: Radius(g1) = 15
    c: Horizontal(g2)
    c: Coincident(g2,g3)
    c: Vertical(g3)
    c: Coincident(g3,g4)
    c: Horizontal(g4)
    c: Tangent(g1,g2) = -1.5708
    c: Tangent(g1,g4) = -1.5708
    c: Distance(g2) = 64
FEATURE [Part::Cylinder] Cylinder006  label="円柱003"
  Angle = 360
  AttacherType = Attacher::AttachEngine3D
  FirstAngle = 0
  Height = 500
  Placement = pos=(-24,0,0) rot=(0,-1,0;1.5708rad)
  Radius = 6
  SecondAngle = 0
  expr: .Placement.Base.x = -Spreadsheet008.dia * 2
  expr: Radius = Spreadsheet008.dia / 2
FEATURE [Sketcher::SketchObject] Sketch057
  FullyConstrained = true
  Placement = pos=(0,0,0) rot=(1,0,0;1.5708rad)
  expr: Constraints[10] = Spreadsheet008.C6
  expr: Constraints[11] = Spreadsheet008.B6
  expr: Constraints[12] = Spreadsheet008.D6 / 2
  expr: Constraints[13] = Spreadsheet008.F6 / 2
  expr: Constraints[14] = Spreadsheet008.B6 / 2
  expr: Constraints[17] = Spreadsheet008.C6
  sketch-geometry (6):
    g0: LineSegment StartX=-50 StartY=0 StartZ=0 EndX=-50 EndY=11 EndZ=0
    g1: LineSegment StartX=-50 StartY=11 StartZ=0 EndX=-30 EndY=15 EndZ=0
    g2: LineSegment StartX=-30 StartY=15 StartZ=0 EndX=30 EndY=15 EndZ=0
    g3: LineSegment StartX=30 StartY=15 StartZ=0 EndX=50 EndY=11 EndZ=0
    g4: LineSegment StartX=50 StartY=11 StartZ=0 EndX=50 EndY=0 EndZ=0
    g5: LineSegment StartX=50 StartY=0 StartZ=0 EndX=-50 EndY=0 EndZ=0
  constraints (18):
    c: PointOnObject(g0,g-1)
    c: Vertical(g0)
    c: Coincident(g0,g1)
    c: Coincident(g1,g2)
    c: Horizontal(g2)
    c: Coincident(g2,g3)
    c: Coincident(g3,g4)
    c: PointOnObject(g4,g-1)
    c: Vertical(g4)
    c: Coincident(g4,g5)
    c: DistanceX(g2,g3) = 20
    c: DistanceX(g0,g3) = 100
    c: Distance(g1,g5) = 15
    c: Distance(g4) = 11
    c: DistanceX(g-1,g4) = 50
    c: Horizontal(g0,g3)
    c: Coincident(g5,g0)
    c: DistanceX(g0,g1) = 20
FEATURE [Part::Revolution] Revolve006
  Angle = 360
  Axis = (-1,0,0)
  AxisLink = -> Sketch057 [Edge6]
  Base = (-50,0,0)
  FaceMakerClass = Part::FaceMakerBullseye
  Solid = true
  Source = -> Sketch057
  Symmetric = false
FEATURE [Sketcher::SketchObject] Sketch058
  FullyConstrained = false
  Placement = pos=(0,0,0) rot=(0.57735,0.57735,0.57735;2.0944rad)
  expr: Constraints[16] = Spreadsheet008.F6
  expr: Constraints[17] = Spreadsheet008.F6 / 2
  sketch-geometry (8):
    g0: LineSegment StartX=-11 StartY=39.685 StartZ=0 EndX=-26 EndY=39.685 EndZ=0
    g1: LineSegment StartX=-26 StartY=39.685 StartZ=0 EndX=-26 EndY=-39.3666 EndZ=0
    g2: LineSegment StartX=-26 StartY=-39.3666 StartZ=0 EndX=-11 EndY=-39.3666 EndZ=0
    g3: LineSegment StartX=-11 StartY=-39.3666 StartZ=0 EndX=-11 EndY=39.685 EndZ=0
    g4: LineSegment StartX=11 StartY=39.685 StartZ=0 EndX=26 EndY=39.685 EndZ=0
    g5: LineSegment StartX=26 StartY=39.685 StartZ=0 EndX=26 EndY=-40.315 EndZ=0
    g6: LineSegment StartX=26 StartY=-40.315 StartZ=0 EndX=11 EndY=-40.315 EndZ=0
    g7: LineSegment StartX=11 StartY=-40.315 StartZ=0 EndX=11 EndY=39.685 EndZ=0
  constraints (22):
    c: Coincident(g0,g1)
    c: Coincident(g1,g2)
    c: Coincident(g2,g3)
    c: Coincident(g3,g0)
    c: Horizontal(g0)
    c: Horizontal(g2)
    c: Vertical(g1)
    c: Vertical(g3)
    c: Coincident(g4,g5)
    c: Coincident(g5,g6)
    c: Coincident(g6,g7)
    c: Coincident(g7,g4)
    c: Horizontal(g4)
    c: Horizontal(g6)
    c: Vertical(g5)
    c: Vertical(g7)
    c: DistanceX(g0,g4) = 22
    c: Distance(g-1,g7) = 11
    c: Distance(g5) = 80
    c: Distance(g4) = 15
    c: Distance(g0) = 15
    c: Horizontal(g0,g4)
FEATURE [Part::Extrusion] Extrude052  label="Extrude057"
  Base = -> Sketch058
  Dir = (1,0,0)
  DirMode = 2
  FaceMakerClass = Part::FaceMakerBullseye
  LengthFwd = 300
  LengthRev = 0
  Solid = true
  Symmetric = true
FEATURE [Part::Cut] Cut018  label="Cut037"
  Base = -> Revolve006
  Tool = -> Extrude052
FEATURE [Sketcher::SketchObject] Sketch059
  FullyConstrained = true
  Placement = pos=(0,0,0) rot=(1,0,0;1.5708rad)
  expr: Constraints[17] = Spreadsheet008.E6
  expr: Constraints[18] = Spreadsheet008.B6 - 2 * Spreadsheet008.C6
  expr: Constraints[19] = (Spreadsheet008.B6 - 2 * Spreadsheet008.C6) / 2
  expr: Constraints[20] = Spreadsheet008.E6 / 2
  sketch-geometry (9):
    g0: LineSegment StartX=30 StartY=3 StartZ=0 EndX=30 EndY=-3 EndZ=0
    g1: LineSegment StartX=25 StartY=-8 StartZ=0 EndX=-25 EndY=-8 EndZ=0
    g2: LineSegment StartX=-30 StartY=-3 StartZ=0 EndX=-30 EndY=3 EndZ=0
    g3: LineSegment StartX=-25 StartY=8 StartZ=0 EndX=25 EndY=8 EndZ=0
    g4: GeomPoint X=0 Y=0 Z=0
    g5: ArcOfCircle CenterX=-25 CenterY=3 CenterZ=0 NormalX=0 NormalY=0 NormalZ=1 AngleXU=0 Radius=5 StartAngle=1.5708 EndAngle=3.14159
    g6: ArcOfCircle CenterX=-25 CenterY=-3 CenterZ=0 NormalX=0 NormalY=0 NormalZ=1 AngleXU=0 Radius=5 StartAngle=3.14159 EndAngle=4.71239
    g7: ArcOfCircle CenterX=25 CenterY=-3 CenterZ=0 NormalX=0 NormalY=0 NormalZ=1 AngleXU=0 Radius=5 StartAngle=4.71239 EndAngle=6.28319
    g8: ArcOfCircle CenterX=25 CenterY=3 CenterZ=0 NormalX=0 NormalY=0 NormalZ=1 AngleXU=0 Radius=5 StartAngle=-4.09e-14 EndAngle=1.5708
  constraints (21):
    c: Horizontal(g1)
    c: Horizontal(g3)
    c: Vertical(g0)
    c: Vertical(g2)
    c: Coincident(g4,g-1)
    c: Tangent(g3,g5) = 1.5708
    c: Tangent(g2,g5) = 1.5708
    c: Tangent(g1,g6) = 1.5708
    c: Tangent(g2,g6) = 1.5708
    c: Tangent(g1,g7) = 1.5708
    c: Tangent(g0,g7) = 1.5708
    c: Tangent(g0,g8) = 1.5708
    c: Tangent(g3,g8) = 1.5708
    c: Radius(g8) = 5
    c: Equal(g8,g7)
    c: Equal(g7,g6)
    c: Equal(g6,g5)
    c: DistanceY(g1,g3) = 16
    c: DistanceX(g2,g0) = 60
    c: Distance(g4,g2) = 30
    c: Distance(g4,g1) = 8
FEATURE [Part::Extrusion] Extrude053  label="Extrude058"
  Base = -> Sketch059
  Dir = (0,-1,2e-16)
  DirMode = 2
  FaceMakerClass = Part::FaceMakerBullseye
  LengthFwd = 60
  LengthRev = 0
  Solid = true
  Symmetric = true
FEATURE [Part::Cut] Cut019
  Base = -> Cut018
  Tool = -> Extrude053
FEATURE [Sketcher::SketchObject] Sketch060
  FullyConstrained = true
  Placement = pos=(0,0,0) rot=(0.57735,0.57735,0.57735;2.0944rad)
  expr: Constraints[1] = Spreadsheet008.dia / 2
  sketch-geometry (1):
    g0: Circle CenterX=0 CenterY=0 CenterZ=0 NormalX=0 NormalY=0 NormalZ=1 AngleXU=0 Radius=6
  constraints (2):
    c: Coincident(g0,g-1)
    c: Radius(g0) = 6
FEATURE [Part::Extrusion] Extrude054  label="Extrude059"
  Base = -> Sketch060
  Dir = (1,0,0)
  DirMode = 2
  FaceMakerClass = Part::FaceMakerBullseye
  LengthFwd = 300
  LengthRev = 0
  Solid = true
  Symmetric = true
FEATURE [Part::Cut] Cut020  label="turnBackle003"
  Base = -> Cut019
  Placement = pos=(-530,0,0) rot=(0,0,1;0rad)
  Tool = -> Extrude054
  expr: .Placement.Base.x = -(Spreadsheet008.dia * 2.5 + 500)
FEATURE [Part::Cylinder] Cylinder007  label="rod005"
  Angle = 360
  AttacherType = Attacher::AttachEngine3D
  FirstAngle = 0
  Height = 2635
  Placement = pos=(-536,0,-1.37e-13) rot=(0,-1,0;1.5708rad)
  Radius = 6
  SecondAngle = 0
  expr: .Placement.Base.x = -(Spreadsheet008.dia * 3 + 500)
  expr: Height = Spreadsheet008.l1
  expr: Radius = Spreadsheet008.dia / 2
FEATURE [Part::Extrusion] Extrude055  label="Extrude060"
  Base = -> Sketch056
  Dir = (0,-1,2e-16)
  DirMode = 2
  FaceMakerClass = Part::FaceMakerBullseye
  LengthFwd = 6
  LengthRev = 0
  Placement = pos=(0,9,0) rot=(0,0,1;0rad)
  Solid = true
  Symmetric = true
  expr: .Placement.Base.y = Spreadsheet008.dia / 2 + Spreadsheet008.t0 / 2
  expr: LengthFwd = Spreadsheet008.t0
FEATURE [Part::FeaturePython] Clone010  label="Extrude061"  # Draft clone (typed FeaturePython)
  AttacherType = Attacher::AttachEngine3D
  Fuse = false
  Objects = -> [Extrude055]
  Placement = pos=(-3195,9,0) rot=(0,1,0;3.14159rad)
  Scale = (1,1,1)
  expr: .Placement.Base.x = -Spreadsheet008.L0
  expr: .Placement.Base.y = Spreadsheet008.t0 / 2 + Spreadsheet008.dia / 2
FEATURE [App::Part] Part027  label="TurnBackleB"
  Group = -> [Spreadsheet008,Sketch056,Cylinder006,Extrude055,Revolve006,Sketch058,Cut019,Cut018,Extrude052,Extrude053,Extrude054,Sketch059,Sketch057,Sketch060,Cut020,Cylinder007,Clone010]
  Origin = -> Origin031
  Placement = pos=(-1778.27,238.926,0) rot=(1,0,0;4.71239rad)
FEATURE [Part::Compound] Compound033  label="trunBackle"
  Links = -> [Part027]
  Placement = pos=(-4690.78,487.977,0) rot=(0,0,1;2.9339rad)
FEATURE [Part::Mirroring] Mirror032  label="trunBackle (mirrored)"
  Base = (1000,0,0)
  Normal = (0,-1,0)
  Source = -> Compound033
FEATURE [App::Part] Part025  label="skimmerBrade001"
  Group = -> [Part024,Part023,CNROK75_U,Compound032,Spreadsheet007,Part026,Array019,axisCoincident_001_mirror,ChannelSteel007,Extrude049,Sketch055,Extrude051,Mirror031,Part027,Compound033,Mirror032]
  Origin = -> Origin027
  Placement = pos=(-1076.83,0,5228.17) rot=(0,0,1;0rad)
FEATURE [App::Part] Part001  label="movingPart"
  Group = -> [Part002,centerCage002_001,Part003,b_trunBackle_001_,Compound020,Clone,b_brade_001_,b_RakeArm_001_,Array014,Compound022,axisCoincident_002,axisCoincident_003,Compound023,Array015,Part025]
  Origin = -> Origin006
